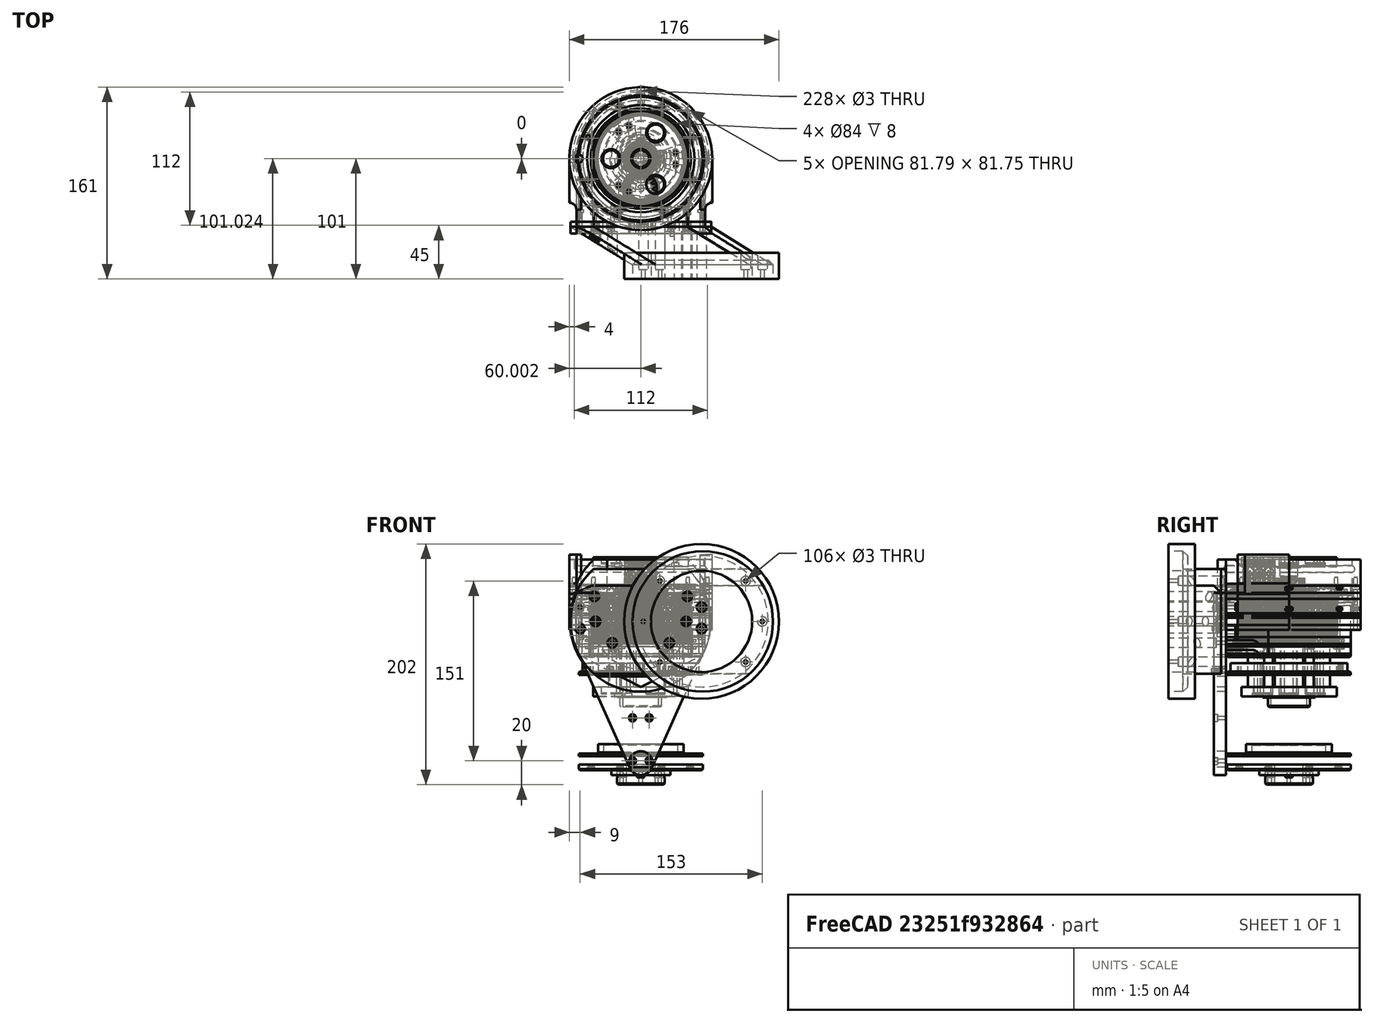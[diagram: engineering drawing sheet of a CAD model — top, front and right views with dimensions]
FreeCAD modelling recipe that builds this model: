
FCSTD DOCUMENT  (FreeCAD 0.19R24276 (Git))
Label: J-max-deep_053
License: All rights reserved
LicenseURL: http://en.wikipedia.org/wiki/All_rights_reserved
objects: Part::Cylinder×715, Part::Cut×269, Part::Compound×252, Part::Box×221, Part::FeaturePython×74, Part::Fillet×14, Part::Chamfer×11, Mesh::Feature×8, Part::Common×7, Part::Torus×4, Part::Wedge×4, Sketcher::SketchObject×3, Part::Extrusion×2, PartDesign::Pad×1, PartDesign::Body×1
note: 1579 computed .brp shape members not serialized (recipe doc carries the construction recipe); baked Part::Feature solids carry a one-line shape summary decoded from their .brp

FEATURE [Part::Cylinder] Cylinder862  label="Válec862"
  Angle = 360
  AttacherType = Attacher::AttachEngine3D
  Height = 20
  Placement = pos=(-51,-40,7) rot=(1,0,0;1.5708rad)
  Radius = 1.5
FEATURE [Part::Cylinder] Cylinder863  label="Válec863"
  Angle = 360
  AttacherType = Attacher::AttachEngine3D
  Height = 40
  Placement = pos=(-59,-17,0) rot=(0,0,1;0rad)
  Radius = 10
FEATURE [Part::Cylinder] Cylinder864  label="Válec864"
  Angle = 360
  AttacherType = Attacher::AttachEngine3D
  Height = 10
  Placement = pos=(0,0,20) rot=(0,0,1;0rad)
  Radius = 52
FEATURE [Part::Cylinder] Cylinder865  label="Válec865"
  Angle = 360
  AttacherType = Attacher::AttachEngine3D
  Height = 20
  Placement = pos=(51,-40,7) rot=(1,0,0;1.5708rad)
  Radius = 1.5
FEATURE [Part::Cylinder] Cylinder866  label="Válec866"
  Angle = 360
  AttacherType = Attacher::AttachEngine3D
  Height = 20
  Placement = pos=(56,0,2) rot=(0,0,1;1.5708rad)
  Radius = 1.5
FEATURE [Part::Box] Box134  label="Krychle134"
  AttacherType = Attacher::AttachEngine3D
  Height = 10
  Length = 108
  Placement = pos=(-54,-53,20) rot=(0,0,1;0rad)
  Width = 36
FEATURE [Part::Cylinder] Cylinder867  label="Válec867"
  Angle = 360
  AttacherType = Attacher::AttachEngine3D
  Height = 10
  Placement = pos=(0,0,20) rot=(0,0,1;0rad)
  Radius = 52
FEATURE [Part::Box] Box132  label="Krychle132"
  AttacherType = Attacher::AttachEngine3D
  Height = 6
  Length = 6
  Placement = pos=(-23,-47,-8) rot=(0,0,1;0rad)
  Width = 2
FEATURE [Part::Box] Box133  label="Krychle133"
  AttacherType = Attacher::AttachEngine3D
  Height = 6
  Length = 6
  Placement = pos=(-54,-45,4) rot=(0,0,1;0rad)
  Width = 2
FEATURE [Part::Box] Box131  label="Krychle131"
  AttacherType = Attacher::AttachEngine3D
  Height = 6
  Length = 6
  Placement = pos=(17,-47,-8) rot=(0,0,1;0rad)
  Width = 2
FEATURE [Part::Cylinder] Cylinder868  label="Válec868"
  Angle = 360
  AttacherType = Attacher::AttachEngine3D
  Height = 20
  Placement = pos=(-20,-40,-5) rot=(1,0,0;1.5708rad)
  Radius = 1.5
FEATURE [Part::Cylinder] Cylinder869  label="Válec869"
  Angle = 360
  AttacherType = Attacher::AttachEngine3D
  Height = 20
  Placement = pos=(39.598,39.598,2) rot=(0,0,1;2.35619rad)
  Radius = 1.5
FEATURE [Part::Cylinder] Cylinder870  label="Válec870"
  Angle = 360
  AttacherType = Attacher::AttachEngine3D
  Height = 20
  Placement = pos=(20,-40,-5) rot=(1,0,0;1.5708rad)
  Radius = 1.5
FEATURE [Part::Compound] Compound261
  Links = -> [Cylinder868,Cylinder870,Cylinder865,Cylinder862]
FEATURE [Part::Cylinder] Cylinder871  label="Válec871"
  Angle = 360
  AttacherType = Attacher::AttachEngine3D
  Height = 20
  Placement = pos=(-39.6,-39.6,-10) rot=(0,0,-1;0.785398rad)
  Radius = 4
FEATURE [Part::Cylinder] Cylinder872  label="Válec872"
  Angle = 360
  AttacherType = Attacher::AttachEngine3D
  Height = 20
  Placement = pos=(39.6,-39.6,-10) rot=(0,0,1;0.785398rad)
  Radius = 4
FEATURE [Part::Compound] Compound259
  Links = -> [Cylinder871,Cylinder872]
FEATURE [Part::Box] Box130  label="Krychle130"
  AttacherType = Attacher::AttachEngine3D
  Height = 6
  Length = 6
  Placement = pos=(48,-45,4) rot=(0,0,1;0rad)
  Width = 2
FEATURE [Part::Compound] Compound258
  Links = -> [Box132,Box131,Box130,Box133]
FEATURE [Part::Cylinder] Cylinder873  label="Válec873"
  Angle = 360
  AttacherType = Attacher::AttachEngine3D
  Height = 20
  Placement = pos=(-39.598,-39.598,2) rot=(0,0,-1;0.785398rad)
  Radius = 1.5
FEATURE [Part::FeaturePython] Tube087  # WARN: FeaturePython — macro-defined, semantics opaque (R4)
  AttacherType = Attacher::AttachEngine3D
  Height = 8
  InnerRadius = 42
  OuterRadius = 52
  Placement = pos=(0,0,-8) rot=(0,0,1;0rad)
FEATURE [Part::FeaturePython] wormgear045  # WARN: FeaturePython — macro-defined, semantics opaque (R4)
  AttacherType = Attacher::AttachEngine3D
  Placement = pos=(0,0,0) rot=(0,0,1;0.083427rad)
  beta = 34.422
  clearance = 0.25
  diameter = 78.8
  head = 0
  height = 20
  module = 1.2
  pressure_angle = 20
  reverse_pitch = false
  teeth = 45
  version = 0.0.3
FEATURE [Part::FeaturePython] wormgear046  # WARN: FeaturePython — macro-defined, semantics opaque (R4)
  AttacherType = Attacher::AttachEngine3D
  beta = 34.422
  clearance = 0.25
  diameter = 78.8
  head = 0
  height = 20
  module = 1.2
  pressure_angle = 20
  reverse_pitch = true
  teeth = 45
  version = 0.0.3
FEATURE [Part::Cut] Cut152
  Base = -> Box134
  Placement = pos=(0,0,-10) rot=(0,0,1;0rad)
  Tool = -> Cylinder867
FEATURE [Part::Cylinder] Cylinder372  label="Válec372"
  Angle = 360
  AttacherType = Attacher::AttachEngine3D
  Height = 20
  Placement = pos=(-1.2e-14,56,2) rot=(0,0,1;3.14159rad)
  Radius = 1.5
FEATURE [Part::Cylinder] Cylinder874  label="Válec874"
  Angle = 360
  AttacherType = Attacher::AttachEngine3D
  Height = 20
  Placement = pos=(0,-56,2) rot=(0,0,1;0rad)
  Radius = 1.5
FEATURE [Part::Cylinder] Cylinder875  label="Válec875"
  Angle = 360
  AttacherType = Attacher::AttachEngine3D
  Height = 20
  Placement = pos=(39.598,-39.598,2) rot=(0,0,1;0.785398rad)
  Radius = 1.5
FEATURE [Part::Cylinder] Cylinder377  label="Válec377"
  Angle = 360
  AttacherType = Attacher::AttachEngine3D
  Height = 20
  Placement = pos=(-39.598,39.598,2) rot=(0,0,1;3.92699rad)
  Radius = 1.5
FEATURE [Part::Cylinder] Cylinder876  label="Válec876"
  Angle = 360
  AttacherType = Attacher::AttachEngine3D
  Height = 20
  Placement = pos=(-56,-1.3e-14,2) rot=(0,0,-1;1.5708rad)
  Radius = 1.5
FEATURE [Part::Compound] Compound262
  Links = -> [Cylinder874,Cylinder875,Cylinder866,Cylinder869,Cylinder372,Cylinder377,Cylinder876,Cylinder873]
FEATURE [Part::Cut] Cut151
  Base = -> Cut152
  Tool = -> Compound262
FEATURE [Part::Box] Box398  label="Krychle398"
  AttacherType = Attacher::AttachEngine3D
  Height = 6
  Length = 6
  Placement = pos=(-54,-45,4) rot=(0,0,1;0rad)
  Width = 2
FEATURE [Part::Cylinder] Cylinder877  label="Válec877"
  Angle = 360
  AttacherType = Attacher::AttachEngine3D
  Height = 20
  Placement = pos=(-39.6,-39.6,-10) rot=(0,0,-1;0.785398rad)
  Radius = 4
FEATURE [Part::Cylinder] Cylinder878  label="Válec878"
  Angle = 360
  AttacherType = Attacher::AttachEngine3D
  Height = 40
  Placement = pos=(59,-17,0) rot=(0,0,1;0rad)
  Radius = 10
FEATURE [Part::Box] Box399  label="Krychle399"
  AttacherType = Attacher::AttachEngine3D
  Height = 6
  Length = 6
  Placement = pos=(21,-47,-8) rot=(0,0,1;0rad)
  Width = 2
FEATURE [Part::Box] Box400  label="Krychle400"
  AttacherType = Attacher::AttachEngine3D
  Height = 10
  Length = 10
  Placement = pos=(50,-43,10) rot=(0,0,1;0rad)
  Width = 43
FEATURE [Part::Box] Box401  label="Krychle401"
  AttacherType = Attacher::AttachEngine3D
  Height = 6
  Length = 6
  Placement = pos=(48,-45,4) rot=(0,0,1;0rad)
  Width = 2
FEATURE [Part::Box] Box402  label="Krychle402"
  AttacherType = Attacher::AttachEngine3D
  Height = 6
  Length = 6
  Placement = pos=(-27,-47,-8) rot=(0,0,1;0rad)
  Width = 2
FEATURE [Part::Compound] Compound772
  Links = -> [Box402,Box399,Box401,Box398]
FEATURE [Part::Box] Box403  label="Krychle403"
  AttacherType = Attacher::AttachEngine3D
  Height = 8
  Length = 108
  Placement = pos=(-54,-53,20) rot=(0,0,1;0rad)
  Width = 36
FEATURE [Part::Cylinder] Cylinder879  label="Válec879"
  Angle = 360
  AttacherType = Attacher::AttachEngine3D
  Height = 8
  Placement = pos=(0,0,20) rot=(0,0,1;0rad)
  Radius = 52
FEATURE [Part::Cut] Cut400
  Base = -> Box403
  Placement = pos=(0,0,-20) rot=(0,0,1;0rad)
  Tool = -> Cylinder879
FEATURE [Part::Cylinder] Cylinder880  label="Válec880"
  Angle = 360
  AttacherType = Attacher::AttachEngine3D
  Height = 40
  Placement = pos=(-59,-17,0) rot=(0,0,1;0rad)
  Radius = 10
FEATURE [Part::Compound] Compound774
  Links = -> [Cylinder878,Cylinder880]
FEATURE [Part::Cylinder] Cylinder881  label="Válec881"
  Angle = 360
  AttacherType = Attacher::AttachEngine3D
  Height = 20
  Placement = pos=(-51,-40,7) rot=(1,0,0;1.5708rad)
  Radius = 1.5
FEATURE [Part::Cylinder] Cylinder882  label="Válec882"
  Angle = 360
  AttacherType = Attacher::AttachEngine3D
  Height = 20
  Placement = pos=(39.6,-39.6,-10) rot=(0,0,1;0.785398rad)
  Radius = 4
FEATURE [Part::Compound] Compound775
  Links = -> [Cylinder877,Cylinder882]
FEATURE [Part::Cylinder] Cylinder883  label="Válec883"
  Angle = 360
  AttacherType = Attacher::AttachEngine3D
  Height = 20
  Placement = pos=(24,-40,-5) rot=(1,0,0;1.5708rad)
  Radius = 1.5
FEATURE [Part::Cylinder] Cylinder884  label="Válec884"
  Angle = 360
  AttacherType = Attacher::AttachEngine3D
  Height = 20
  Placement = pos=(51,-40,7) rot=(1,0,0;1.5708rad)
  Radius = 1.5
FEATURE [Part::Cylinder] Cylinder885  label="Válec885"
  Angle = 360
  AttacherType = Attacher::AttachEngine3D
  Height = 20
  Placement = pos=(-24,-40,-5) rot=(1,0,0;1.5708rad)
  Radius = 1.5
FEATURE [Part::Compound] Compound773
  Links = -> [Cylinder885,Cylinder883,Cylinder884,Cylinder881]
FEATURE [Part::Cylinder] Cylinder886  label="Válec886"
  Angle = 360
  AttacherType = Attacher::AttachEngine3D
  Height = 20
  Placement = pos=(39.598,39.598,2) rot=(0,0,1;2.35619rad)
  Radius = 1.5
FEATURE [Part::Cylinder] Cylinder887  label="Válec887"
  Angle = 360
  AttacherType = Attacher::AttachEngine3D
  Height = 20
  Placement = pos=(0,-56,2) rot=(0,0,1;0rad)
  Radius = 1.5
FEATURE [Part::Box] Box404  label="Krychle404"
  AttacherType = Attacher::AttachEngine3D
  Height = 2
  Length = 6
  Placement = pos=(-41,-3,-4) rot=(0,0,1;1.5708rad)
  Width = 8
FEATURE [Part::Cylinder] Cylinder888  label="Válec888"
  Angle = 360
  AttacherType = Attacher::AttachEngine3D
  Height = 20
  Placement = pos=(24,-40,-5) rot=(1,0,0;1.5708rad)
  Radius = 1.5
FEATURE [Part::Cylinder] Cylinder889  label="Válec889"
  Angle = 360
  AttacherType = Attacher::AttachEngine3D
  Height = 10
  Placement = pos=(60,-43,10) rot=(0,0,1;0rad)
  Radius = 6
FEATURE [Part::Cylinder] Cylinder890  label="Válec890"
  Angle = 360
  AttacherType = Attacher::AttachEngine3D
  Height = 20
  Placement = pos=(-39.598,-39.598,2) rot=(0,0,-1;0.785398rad)
  Radius = 1.5
FEATURE [Part::Box] Box405  label="Krychle405"
  AttacherType = Attacher::AttachEngine3D
  Height = 10
  Length = 10
  Placement = pos=(-60,-43,10) rot=(0,0,1;0rad)
  Width = 43
FEATURE [Part::Compound] Compound778
  Links = -> [Box405,Box400]
FEATURE [Part::Cylinder] Cylinder891  label="Válec891"
  Angle = 360
  AttacherType = Attacher::AttachEngine3D
  Height = 20
  Placement = pos=(-39.598,39.598,2) rot=(0,0,1;3.92699rad)
  Radius = 1.5
FEATURE [Part::Cylinder] Cylinder892  label="Válec892"
  Angle = 360
  AttacherType = Attacher::AttachEngine3D
  Height = 20
  Placement = pos=(56,0,2) rot=(0,0,1;1.5708rad)
  Radius = 1.5
FEATURE [Part::Cylinder] Cylinder893  label="Válec893"
  Angle = 360
  AttacherType = Attacher::AttachEngine3D
  Height = 20
  Placement = pos=(-1.2e-14,56,2) rot=(0,0,1;3.14159rad)
  Radius = 1.5
FEATURE [Part::Cylinder] Cylinder894  label="Válec894"
  Angle = 360
  AttacherType = Attacher::AttachEngine3D
  Height = 20
  Placement = pos=(-56,-1.3e-14,2) rot=(0,0,-1;1.5708rad)
  Radius = 1.5
FEATURE [Part::Cylinder] Cylinder895  label="Válec895"
  Angle = 360
  AttacherType = Attacher::AttachEngine3D
  Height = 10
  Placement = pos=(-60,-43,10) rot=(0,0,1;0rad)
  Radius = 6
FEATURE [Part::Compound] Compound777
  Links = -> [Cylinder889,Cylinder895]
FEATURE [Part::Cylinder] Cylinder896  label="Válec896"
  Angle = 360
  AttacherType = Attacher::AttachEngine3D
  Height = 20
  Placement = pos=(-51,-40,7) rot=(1,0,0;1.5708rad)
  Radius = 1.5
FEATURE [Part::Cylinder] Cylinder897  label="Válec897"
  Angle = 360
  AttacherType = Attacher::AttachEngine3D
  Height = 20
  Placement = pos=(51,-40,7) rot=(1,0,0;1.5708rad)
  Radius = 1.5
FEATURE [Part::Box] Box406  label="Krychle406"
  AttacherType = Attacher::AttachEngine3D
  Height = 6
  Length = 6
  Placement = pos=(48,-45,4) rot=(0,0,1;0rad)
  Width = 2
FEATURE [Part::Cylinder] Cylinder898  label="Válec898"
  Angle = 360
  AttacherType = Attacher::AttachEngine3D
  Height = 20
  Placement = pos=(0,45,-18) rot=(0,0,1;0rad)
  Radius = 1.5
FEATURE [Part::Cylinder] Cylinder899  label="Válec899"
  Angle = 360
  AttacherType = Attacher::AttachEngine3D
  Height = 20
  Placement = pos=(39.598,-39.598,2) rot=(0,0,1;0.785398rad)
  Radius = 1.5
FEATURE [Part::Compound] Compound776
  Links = -> [Cylinder887,Cylinder899,Cylinder892,Cylinder886,Cylinder893,Cylinder891,Cylinder894,Cylinder890]
FEATURE [Part::Cylinder] Cylinder900  label="Válec900"
  Angle = 360
  AttacherType = Attacher::AttachEngine3D
  Height = 20
  Placement = pos=(-24,-40,-5) rot=(1,0,0;1.5708rad)
  Radius = 1.5
FEATURE [Part::Compound] Compound255
  Links = -> [Cylinder900,Cylinder888,Cylinder897,Cylinder896]
FEATURE [Part::Box] Box407  label="Krychle407"
  AttacherType = Attacher::AttachEngine3D
  Height = 2
  Length = 6
  Placement = pos=(3,-41,-4) rot=(0,0,1;3.14159rad)
  Width = 8
FEATURE [Part::Cylinder] Cylinder901  label="Válec901"
  Angle = 360
  AttacherType = Attacher::AttachEngine3D
  Height = 20
  Placement = pos=(1.4e-14,-45,-18) rot=(0,0,1;3.14159rad)
  Radius = 1.5
FEATURE [Part::Box] Box408  label="Krychle408"
  AttacherType = Attacher::AttachEngine3D
  Height = 2
  Length = 6
  Placement = pos=(-31.1127,26.8701,-4) rot=(0,0,1;0.785398rad)
  Width = 8
FEATURE [Part::Box] Box409  label="Krychle409"
  AttacherType = Attacher::AttachEngine3D
  Height = 6
  Length = 6
  Placement = pos=(21,-47,-8) rot=(0,0,1;0rad)
  Width = 2
FEATURE [Part::Box] Box410  label="Krychle410"
  AttacherType = Attacher::AttachEngine3D
  Height = 6
  Length = 6
  Placement = pos=(-27,-47,-8) rot=(0,0,1;0rad)
  Width = 2
FEATURE [Part::Box] Box411  label="Krychle411"
  AttacherType = Attacher::AttachEngine3D
  Height = 6
  Length = 6
  Placement = pos=(-54,-45,4) rot=(0,0,1;0rad)
  Width = 2
FEATURE [Part::Compound] Compound257
  Links = -> [Box410,Box409,Box406,Box411]
FEATURE [Part::Box] Box412  label="Krychle412"
  AttacherType = Attacher::AttachEngine3D
  Height = 2
  Length = 6
  Placement = pos=(31.1127,-26.8701,-4) rot=(0,0,1;3.92699rad)
  Width = 8
FEATURE [Part::Cylinder] Cylinder902  label="Válec902"
  Angle = 360
  AttacherType = Attacher::AttachEngine3D
  Height = 20
  Placement = pos=(-31.8198,-31.8198,-18) rot=(0,0,1;2.35619rad)
  Radius = 1.5
FEATURE [Part::Cylinder] Cylinder903  label="Válec903"
  Angle = 360
  AttacherType = Attacher::AttachEngine3D
  Height = 20
  Placement = pos=(31.8198,-31.8198,-18) rot=(0,0,1;3.92699rad)
  Radius = 1.5
FEATURE [Part::Cylinder] Cylinder904  label="Válec904"
  Angle = 360
  AttacherType = Attacher::AttachEngine3D
  Height = 20
  Placement = pos=(-31.8198,31.8198,-18) rot=(0,0,1;0.785398rad)
  Radius = 1.5
FEATURE [Part::Cylinder] Cylinder905  label="Válec905"
  Angle = 360
  AttacherType = Attacher::AttachEngine3D
  Height = 20
  Placement = pos=(45,1.9e-14,-18) rot=(0,0,-1;1.5708rad)
  Radius = 1.5
FEATURE [Part::Box] Box413  label="Krychle413"
  AttacherType = Attacher::AttachEngine3D
  Height = 2
  Length = 6
  Placement = pos=(-3,41,-4) rot=(0,0,1;0rad)
  Width = 8
FEATURE [Part::Box] Box414  label="Krychle414"
  AttacherType = Attacher::AttachEngine3D
  Height = 2
  Length = 6
  Placement = pos=(26.8701,31.1127,-4) rot=(0,0,-1;0.785398rad)
  Width = 8
FEATURE [Part::Cylinder] Cylinder906  label="Válec906"
  Angle = 360
  AttacherType = Attacher::AttachEngine3D
  Height = 20
  Placement = pos=(31.8198,31.8198,-18) rot=(0,0,-1;0.785398rad)
  Radius = 1.5
FEATURE [Part::Box] Box415  label="Krychle415"
  AttacherType = Attacher::AttachEngine3D
  Height = 2
  Length = 6
  Placement = pos=(-26.8701,-31.1127,-4) rot=(0,0,1;2.35619rad)
  Width = 8
FEATURE [Part::Cylinder] Cylinder907  label="Válec907"
  Angle = 360
  AttacherType = Attacher::AttachEngine3D
  Height = 20
  Placement = pos=(-45,-6e-15,-18) rot=(0,0,1;1.5708rad)
  Radius = 1.5
FEATURE [Part::Compound] Compound256
  Links = -> [Cylinder898,Cylinder904,Cylinder907,Cylinder902,Cylinder901,Cylinder903,Cylinder905,Cylinder906]
  Placement = pos=(0,0,0) rot=(0,0,1;0.392699rad)
FEATURE [Part::Box] Box128  label="Krychle128"
  AttacherType = Attacher::AttachEngine3D
  Height = 2
  Length = 6
  Placement = pos=(41,3,-4) rot=(0,0,-1;1.5708rad)
  Width = 8
FEATURE [Part::Compound] Compound780
  Links = -> [Box413,Box408,Box404,Box415,Box407,Box412,Box128,Box414]
  Placement = pos=(0,0,0) rot=(0,0,1;0.392699rad)
FEATURE [Part::Box] Box129  label="Krychle129"
  AttacherType = Attacher::AttachEngine3D
  Height = 10
  Length = 108
  Placement = pos=(-54,-53,20) rot=(0,0,1;0rad)
  Width = 36
FEATURE [Part::Cylinder] Cylinder908  label="Válec908"
  Angle = 360
  AttacherType = Attacher::AttachEngine3D
  Height = 40
  Placement = pos=(59,-17,0) rot=(0,0,1;0rad)
  Radius = 10
FEATURE [Part::Compound] Compound260
  Links = -> [Cylinder908,Cylinder863]
FEATURE [Part::Cylinder] Cylinder909  label="Válec909"
  Angle = 360
  AttacherType = Attacher::AttachEngine3D
  Height = 20
  Placement = pos=(31.8198,31.8198,-18) rot=(0,0,-1;0.785398rad)
  Radius = 1.5
FEATURE [Part::Cylinder] Cylinder910  label="Válec910"
  Angle = 360
  AttacherType = Attacher::AttachEngine3D
  Height = 20
  Placement = pos=(39.598,-39.598,2) rot=(0,0,1;0.785398rad)
  Radius = 1.5
FEATURE [Part::Cylinder] Cylinder911  label="Válec911"
  Angle = 360
  AttacherType = Attacher::AttachEngine3D
  Height = 20
  Placement = pos=(0,45,-18) rot=(0,0,1;0rad)
  Radius = 1.5
FEATURE [Part::Cylinder] Cylinder912  label="Válec912"
  Angle = 360
  AttacherType = Attacher::AttachEngine3D
  Height = 20
  Placement = pos=(1.4e-14,-45,-18) rot=(0,0,1;3.14159rad)
  Radius = 1.5
FEATURE [Part::Cylinder] Cylinder913  label="Válec913"
  Angle = 360
  AttacherType = Attacher::AttachEngine3D
  Height = 20
  Placement = pos=(31.8198,-31.8198,-18) rot=(0,0,1;3.92699rad)
  Radius = 1.5
FEATURE [Part::Cylinder] Cylinder914  label="Válec914"
  Angle = 360
  AttacherType = Attacher::AttachEngine3D
  Height = 20
  Placement = pos=(-31.8198,-31.8198,-18) rot=(0,0,1;2.35619rad)
  Radius = 1.5
FEATURE [Part::Cylinder] Cylinder915  label="Válec915"
  Angle = 360
  AttacherType = Attacher::AttachEngine3D
  Height = 20
  Placement = pos=(-31.8198,31.8198,-18) rot=(0,0,1;0.785398rad)
  Radius = 1.5
FEATURE [Part::Cylinder] Cylinder916  label="Válec916"
  Angle = 360
  AttacherType = Attacher::AttachEngine3D
  Height = 20
  Placement = pos=(-45,-6e-15,-18) rot=(0,0,1;1.5708rad)
  Radius = 1.5
FEATURE [Part::Cylinder] Cylinder917  label="Válec917"
  Angle = 360
  AttacherType = Attacher::AttachEngine3D
  Height = 20
  Placement = pos=(45,1.9e-14,-18) rot=(0,0,-1;1.5708rad)
  Radius = 1.5
FEATURE [Part::Compound] Compound771
  Links = -> [Cylinder911,Cylinder915,Cylinder916,Cylinder914,Cylinder912,Cylinder913,Cylinder917,Cylinder909]
  Placement = pos=(0,0,4) rot=(0,0,1;0.392699rad)
FEATURE [Part::Cylinder] Cylinder918  label="Válec918"
  Angle = 360
  AttacherType = Attacher::AttachEngine3D
  Height = 20
  Placement = pos=(-56,-1.3e-14,2) rot=(0,0,-1;1.5708rad)
  Radius = 1.5
FEATURE [Part::Cut] Cut403
  Base = -> Cut400
  Placement = pos=(0,0,-8) rot=(0,0,1;0rad)
  Tool = -> Compound774
FEATURE [Part::Cut] Cut401
  Base = -> Cut403
  Tool = -> Compound775
FEATURE [Part::Cut] Cut402
  Base = -> Cut401
  Tool = -> Compound772
FEATURE [Part::Cut] Cut399
  Base = -> Cut402
  Tool = -> Compound773
FEATURE [Part::Fillet] Fillet014
  Base = -> Cut399
  Edges = 2 edges r=12: [Edge2,Edge38]
FEATURE [Part::Cut] Cut405
  Base = -> Compound778
  Tool = -> Compound776
FEATURE [Part::Cut] Cut406
  Base = -> Cut405
  Tool = -> Compound777
FEATURE [Part::Fillet] Fillet015
  Base = -> Cut406
  Edges = 2 edges r=4: [Edge4,Edge43]
FEATURE [Part::Cut] Cut147
  Base = -> Box129
  Placement = pos=(0,0,-20) rot=(0,0,1;0rad)
  Tool = -> Cylinder864
FEATURE [Part::Cut] Cut407
  Base = -> Tube087
  Tool = -> Compound257
FEATURE [Part::Cut] Cut144
  Base = -> Cut407
  Tool = -> Compound255
FEATURE [Part::Cut] Cut404
  Base = -> Cut144
  Tool = -> Compound780
FEATURE [Part::Cut] Cut145
  Base = -> Cut404
  Tool = -> Compound256
FEATURE [Part::Cut] Cut146
  Base = -> Cut147
  Tool = -> Compound260
FEATURE [Part::Cut] Cut149
  Base = -> Cut146
  Tool = -> Compound259
FEATURE [Part::Cut] Cut148
  Base = -> Cut149
  Tool = -> Compound258
FEATURE [Part::Cut] Cut150
  Base = -> Cut148
  Tool = -> Compound261
FEATURE [Part::Fillet] Fillet013
  Base = -> Cut150
  Edges = 2 edges r=12: [Edge6,Edge42]
FEATURE [Part::Cylinder] Cylinder919  label="Válec919"
  Angle = 360
  AttacherType = Attacher::AttachEngine3D
  Height = 20
  Placement = pos=(-39.598,-39.598,2) rot=(0,0,-1;0.785398rad)
  Radius = 1.5
FEATURE [Part::Cylinder] Cylinder920  label="Válec920"
  Angle = 360
  AttacherType = Attacher::AttachEngine3D
  Height = 20
  Placement = pos=(39.6,-39.6,-10) rot=(0,0,1;0.785398rad)
  Radius = 4
FEATURE [Part::Cylinder] Cylinder921  label="Válec921"
  Angle = 360
  AttacherType = Attacher::AttachEngine3D
  Height = 20
  Placement = pos=(-39.598,39.598,2) rot=(0,0,1;3.92699rad)
  Radius = 1.5
FEATURE [Part::Cylinder] Cylinder922  label="Válec922"
  Angle = 360
  AttacherType = Attacher::AttachEngine3D
  Height = 20
  Placement = pos=(-39.6,-39.6,-10) rot=(0,0,-1;0.785398rad)
  Radius = 4
FEATURE [Part::Compound] Compound768
  Links = -> [Cylinder922,Cylinder920]
FEATURE [Part::Cylinder] Cylinder923  label="Válec923"
  Angle = 360
  AttacherType = Attacher::AttachEngine3D
  Height = 20
  Placement = pos=(-1.2e-14,56,2) rot=(0,0,1;3.14159rad)
  Radius = 1.5
FEATURE [Part::Cylinder] Cylinder924  label="Válec924"
  Angle = 360
  AttacherType = Attacher::AttachEngine3D
  Height = 20
  Placement = pos=(56,0,2) rot=(0,0,1;1.5708rad)
  Radius = 1.5
FEATURE [Part::Cylinder] Cylinder925  label="Válec925"
  Angle = 360
  AttacherType = Attacher::AttachEngine3D
  Height = 10
  Radius = 52
FEATURE [Part::Cut] Cut396
  Base = -> Cylinder925
  Tool = -> wormgear045
FEATURE [Part::Cylinder] Cylinder926  label="Válec926"
  Angle = 360
  AttacherType = Attacher::AttachEngine3D
  Height = 10
  Radius = 60
FEATURE [Part::Cut] Cut397
  Base = -> Cylinder926
  Placement = pos=(0,0,10) rot=(0,0,1;0.034907rad)
  Tool = -> wormgear046
FEATURE [Part::Compound] Compound770
  Links = -> [Cut397,Cut396]
FEATURE [Part::Cylinder] Cylinder927  label="Válec927"
  Angle = 360
  AttacherType = Attacher::AttachEngine3D
  Height = 20
  Placement = pos=(0,-56,2) rot=(0,0,1;0rad)
  Radius = 1.5
FEATURE [Part::Cylinder] Cylinder928  label="Válec928"
  Angle = 360
  AttacherType = Attacher::AttachEngine3D
  Height = 20
  Placement = pos=(39.598,39.598,2) rot=(0,0,1;2.35619rad)
  Radius = 1.5
FEATURE [Part::Compound] Compound769
  Links = -> [Cylinder927,Cylinder910,Cylinder924,Cylinder928,Cylinder923,Cylinder921,Cylinder918,Cylinder919]
FEATURE [Part::Cut] Cut394
  Base = -> Compound770
  Tool = -> Compound769
FEATURE [Part::Cut] Cut395
  Base = -> Cut394
  Tool = -> Compound768
FEATURE [Part::Cut] Cut398
  Base = -> Cut395
  Tool = -> Compound771
FEATURE [Part::Compound] Compound779  label="J-max_monoblok"
  Links = -> [Fillet014,Fillet013,Cut151,Cut145,Fillet015,Cut398]
FEATURE [Part::FeaturePython] wormgear052  # WARN: FeaturePython — macro-defined, semantics opaque (R4)
  AttacherType = Attacher::AttachEngine3D
  Placement = pos=(0,0,0) rot=(0,0,1;0.083427rad)
  beta = 40.5833
  clearance = 0.25
  diameter = 78.8
  head = 0
  height = 20
  module = 1.5
  pressure_angle = 20
  reverse_pitch = false
  teeth = 45
  version = 0.0.3
FEATURE [Part::FeaturePython] wormgear053  # WARN: FeaturePython — macro-defined, semantics opaque (R4)
  AttacherType = Attacher::AttachEngine3D
  Placement = pos=(0,0,0) rot=(0,0,1;0.10376rad)
  beta = 40.5833
  clearance = 0.25
  diameter = 78.8
  head = 0
  height = 20
  module = 1.5
  pressure_angle = 20
  reverse_pitch = true
  teeth = 45
  version = 0.0.3
FEATURE [Part::Cylinder] Cylinder990  label="Válec990"
  Angle = 360
  AttacherType = Attacher::AttachEngine3D
  Height = 50
  Placement = pos=(31.8198,31.8198,-18) rot=(0,0,-1;0.785398rad)
  Radius = 1.5
FEATURE [Part::Cylinder] Cylinder991  label="Válec991"
  Angle = 360
  AttacherType = Attacher::AttachEngine3D
  Height = 50
  Placement = pos=(39.598,-39.598,2) rot=(0,0,1;0.785398rad)
  Radius = 1.5
FEATURE [Part::Cylinder] Cylinder992  label="Válec992"
  Angle = 360
  AttacherType = Attacher::AttachEngine3D
  Height = 50
  Placement = pos=(0,45,-18) rot=(0,0,1;0rad)
  Radius = 1.5
FEATURE [Part::Cylinder] Cylinder993  label="Válec993"
  Angle = 360
  AttacherType = Attacher::AttachEngine3D
  Height = 50
  Placement = pos=(1.4e-14,-45,-18) rot=(0,0,1;3.14159rad)
  Radius = 1.5
FEATURE [Part::Cylinder] Cylinder994  label="Válec994"
  Angle = 360
  AttacherType = Attacher::AttachEngine3D
  Height = 50
  Placement = pos=(31.8198,-31.8198,-18) rot=(0,0,1;3.92699rad)
  Radius = 1.5
FEATURE [Part::Cylinder] Cylinder995  label="Válec995"
  Angle = 360
  AttacherType = Attacher::AttachEngine3D
  Height = 50
  Placement = pos=(-31.8198,-31.8198,-18) rot=(0,0,1;2.35619rad)
  Radius = 1.5
FEATURE [Part::Cylinder] Cylinder996  label="Válec996"
  Angle = 360
  AttacherType = Attacher::AttachEngine3D
  Height = 50
  Placement = pos=(-31.8198,31.8198,-18) rot=(0,0,1;0.785398rad)
  Radius = 1.5
FEATURE [Part::Cylinder] Cylinder997  label="Válec997"
  Angle = 360
  AttacherType = Attacher::AttachEngine3D
  Height = 50
  Placement = pos=(-45,-6e-15,-18) rot=(0,0,1;1.5708rad)
  Radius = 1.5
FEATURE [Part::Cylinder] Cylinder998  label="Válec998"
  Angle = 360
  AttacherType = Attacher::AttachEngine3D
  Height = 50
  Placement = pos=(45,1.9e-14,-18) rot=(0,0,-1;1.5708rad)
  Radius = 1.5
FEATURE [Part::Compound] Compound816
  Links = -> [Cylinder992,Cylinder996,Cylinder997,Cylinder995,Cylinder993,Cylinder994,Cylinder998,Cylinder990]
  Placement = pos=(0,0,4) rot=(0,0,1;0.392699rad)
FEATURE [Part::Cylinder] Cylinder999  label="Válec999"
  Angle = 360
  AttacherType = Attacher::AttachEngine3D
  Height = 50
  Placement = pos=(-56,-1.3e-14,2) rot=(0,0,-1;1.5708rad)
  Radius = 1.5
FEATURE [Part::Cylinder] Cylinder1000  label="Válec1000"
  Angle = 360
  AttacherType = Attacher::AttachEngine3D
  Height = 50
  Placement = pos=(-39.598,-39.598,2) rot=(0,0,-1;0.785398rad)
  Radius = 1.5
FEATURE [Part::Cylinder] Cylinder1001  label="Válec1001"
  Angle = 360
  AttacherType = Attacher::AttachEngine3D
  Height = 20
  Placement = pos=(39.6,-39.6,-10) rot=(0,0,1;0.785398rad)
  Radius = 4
FEATURE [Part::Cylinder] Cylinder1002  label="Válec1002"
  Angle = 360
  AttacherType = Attacher::AttachEngine3D
  Height = 50
  Placement = pos=(-39.598,39.598,2) rot=(0,0,1;3.92699rad)
  Radius = 1.5
FEATURE [Part::Cylinder] Cylinder1003  label="Válec1003"
  Angle = 360
  AttacherType = Attacher::AttachEngine3D
  Height = 20
  Placement = pos=(-39.6,-39.6,-10) rot=(0,0,-1;0.785398rad)
  Radius = 4
FEATURE [Part::Compound] Compound813
  Links = -> [Cylinder1003,Cylinder1001]
FEATURE [Part::Cylinder] Cylinder1004  label="Válec1004"
  Angle = 360
  AttacherType = Attacher::AttachEngine3D
  Height = 50
  Placement = pos=(-1.2e-14,56,2) rot=(0,0,1;3.14159rad)
  Radius = 1.5
FEATURE [Part::Cylinder] Cylinder1005  label="Válec1005"
  Angle = 360
  AttacherType = Attacher::AttachEngine3D
  Height = 50
  Placement = pos=(56,0,2) rot=(0,0,1;1.5708rad)
  Radius = 1.5
FEATURE [Part::Cylinder] Cylinder1006  label="Válec1006"
  Angle = 360
  AttacherType = Attacher::AttachEngine3D
  Height = 16
  Radius = 52
FEATURE [Part::Cut] Cut418
  Base = -> Cylinder1006
  Tool = -> wormgear052
FEATURE [Part::Cylinder] Cylinder1007  label="Válec1007"
  Angle = 360
  AttacherType = Attacher::AttachEngine3D
  Height = 16
  Radius = 60
FEATURE [Part::Cut] Cut422
  Base = -> Cylinder1007
  Placement = pos=(0,0,16) rot=(0,0,1;0.034907rad)
  Tool = -> wormgear053
FEATURE [Part::Compound] Compound815
  Links = -> [Cut422,Cut418]
FEATURE [Part::Cylinder] Cylinder1008  label="Válec1008"
  Angle = 360
  AttacherType = Attacher::AttachEngine3D
  Height = 50
  Placement = pos=(0,-56,2) rot=(0,0,1;0rad)
  Radius = 1.5
FEATURE [Part::Cylinder] Cylinder1009  label="Válec1009"
  Angle = 360
  AttacherType = Attacher::AttachEngine3D
  Height = 50
  Placement = pos=(39.598,39.598,2) rot=(0,0,1;2.35619rad)
  Radius = 1.5
FEATURE [Part::Compound] Compound814
  Links = -> [Cylinder1008,Cylinder991,Cylinder1005,Cylinder1009,Cylinder1004,Cylinder1002,Cylinder999,Cylinder1000]
FEATURE [Part::Cut] Cut421
  Base = -> Compound815
  Tool = -> Compound814
FEATURE [Part::Cut] Cut419
  Base = -> Cut421
  Tool = -> Compound813
FEATURE [Part::Cut] Cut420
  Base = -> Cut419
  Tool = -> Compound816
FEATURE [Part::Box] Box416  label="Krychle416"
  AttacherType = Attacher::AttachEngine3D
  Height = 16
  Length = 108
  Placement = pos=(-54,-53,20) rot=(0,0,1;0rad)
  Width = 36
FEATURE [Part::Cylinder] Cylinder1011  label="Válec1011"
  Angle = 360
  AttacherType = Attacher::AttachEngine3D
  Height = 16
  Placement = pos=(0,0,20) rot=(0,0,1;0rad)
  Radius = 52
FEATURE [Part::Cylinder] Cylinder1012  label="Válec1012"
  Angle = 360
  AttacherType = Attacher::AttachEngine3D
  Height = 50
  Placement = pos=(39.598,39.598,2) rot=(0,0,1;2.35619rad)
  Radius = 1.5
FEATURE [Part::Cylinder] Cylinder1013  label="Válec1013"
  Angle = 360
  AttacherType = Attacher::AttachEngine3D
  Height = 50
  Placement = pos=(-39.598,-39.598,2) rot=(0,0,-1;0.785398rad)
  Radius = 1.5
FEATURE [Part::Cylinder] Cylinder1014  label="Válec1014"
  Angle = 360
  AttacherType = Attacher::AttachEngine3D
  Height = 50
  Placement = pos=(-1.2e-14,56,2) rot=(0,0,1;3.14159rad)
  Radius = 1.5
FEATURE [Part::Cylinder] Cylinder1015  label="Válec1015"
  Angle = 360
  AttacherType = Attacher::AttachEngine3D
  Height = 50
  Placement = pos=(0,-56,2) rot=(0,0,1;0rad)
  Radius = 1.5
FEATURE [Part::Cylinder] Cylinder1016  label="Válec1016"
  Angle = 360
  AttacherType = Attacher::AttachEngine3D
  Height = 50
  Placement = pos=(39.598,-39.598,2) rot=(0,0,1;0.785398rad)
  Radius = 1.5
FEATURE [Part::Cylinder] Cylinder1017  label="Válec1017"
  Angle = 360
  AttacherType = Attacher::AttachEngine3D
  Height = 50
  Placement = pos=(-39.598,39.598,2) rot=(0,0,1;3.92699rad)
  Radius = 1.5
FEATURE [Part::Cylinder] Cylinder1018  label="Válec1018"
  Angle = 360
  AttacherType = Attacher::AttachEngine3D
  Height = 50
  Placement = pos=(-56,-1.3e-14,2) rot=(0,0,-1;1.5708rad)
  Radius = 1.5
FEATURE [Part::Cut] Cut424
  Base = -> Box416
  Placement = pos=(0,0,-10) rot=(0,0,1;0rad)
  Tool = -> Cylinder1011
FEATURE [Part::Compound] Compound817
  Links = -> [Cylinder1015,Cylinder1016,Cylinder1012,Cylinder1014,Cylinder1017,Cylinder1018,Cylinder1013]
FEATURE [Part::Cut] Cut423
  Base = -> Cut424
  Placement = pos=(0,0,6) rot=(0,0,1;0rad)
  Tool = -> Compound817
FEATURE [Part::Box] Box417  label="Krychle417"
  AttacherType = Attacher::AttachEngine3D
  Height = 2
  Length = 6
  Placement = pos=(-41,-3,-4) rot=(0,0,1;1.5708rad)
  Width = 8
FEATURE [Part::Cylinder] Cylinder1019  label="Válec1019"
  Angle = 360
  AttacherType = Attacher::AttachEngine3D
  Height = 20
  Placement = pos=(24,-40,-5) rot=(1,0,0;1.5708rad)
  Radius = 1.5
FEATURE [Part::FeaturePython] Tube088  # WARN: FeaturePython — macro-defined, semantics opaque (R4)
  AttacherType = Attacher::AttachEngine3D
  Height = 8
  InnerRadius = 42
  OuterRadius = 52
  Placement = pos=(0,0,-8) rot=(0,0,1;0rad)
FEATURE [Part::Cylinder] Cylinder1020  label="Válec1020"
  Angle = 360
  AttacherType = Attacher::AttachEngine3D
  Height = 20
  Placement = pos=(-51,-40,7) rot=(1,0,0;1.5708rad)
  Radius = 1.5
FEATURE [Part::Cylinder] Cylinder1021  label="Válec1021"
  Angle = 360
  AttacherType = Attacher::AttachEngine3D
  Height = 20
  Placement = pos=(51,-40,7) rot=(1,0,0;1.5708rad)
  Radius = 1.5
FEATURE [Part::Box] Box418  label="Krychle418"
  AttacherType = Attacher::AttachEngine3D
  Height = 6
  Length = 6
  Placement = pos=(48,-45,4) rot=(0,0,1;0rad)
  Width = 2
FEATURE [Part::Cylinder] Cylinder1022  label="Válec1022"
  Angle = 360
  AttacherType = Attacher::AttachEngine3D
  Height = 20
  Placement = pos=(0,45,-18) rot=(0,0,1;0rad)
  Radius = 1.5
FEATURE [Part::Cylinder] Cylinder1023  label="Válec1023"
  Angle = 360
  AttacherType = Attacher::AttachEngine3D
  Height = 20
  Placement = pos=(-24,-40,-5) rot=(1,0,0;1.5708rad)
  Radius = 1.5
FEATURE [Part::Compound] Compound818
  Links = -> [Cylinder1023,Cylinder1019,Cylinder1021,Cylinder1020]
FEATURE [Part::Box] Box419  label="Krychle419"
  AttacherType = Attacher::AttachEngine3D
  Height = 2
  Length = 6
  Placement = pos=(3,-41,-4) rot=(0,0,1;3.14159rad)
  Width = 8
FEATURE [Part::Cylinder] Cylinder1024  label="Válec1024"
  Angle = 360
  AttacherType = Attacher::AttachEngine3D
  Height = 20
  Placement = pos=(1.4e-14,-45,-18) rot=(0,0,1;3.14159rad)
  Radius = 1.5
FEATURE [Part::Box] Box420  label="Krychle420"
  AttacherType = Attacher::AttachEngine3D
  Height = 2
  Length = 6
  Placement = pos=(-31.1127,26.8701,-4) rot=(0,0,1;0.785398rad)
  Width = 8
FEATURE [Part::Box] Box421  label="Krychle421"
  AttacherType = Attacher::AttachEngine3D
  Height = 6
  Length = 6
  Placement = pos=(21,-47,-8) rot=(0,0,1;0rad)
  Width = 2
FEATURE [Part::Box] Box422  label="Krychle422"
  AttacherType = Attacher::AttachEngine3D
  Height = 6
  Length = 6
  Placement = pos=(-27,-47,-8) rot=(0,0,1;0rad)
  Width = 2
FEATURE [Part::Box] Box423  label="Krychle423"
  AttacherType = Attacher::AttachEngine3D
  Height = 6
  Length = 6
  Placement = pos=(-54,-45,4) rot=(0,0,1;0rad)
  Width = 2
FEATURE [Part::Compound] Compound820
  Links = -> [Box422,Box421,Box418,Box423]
FEATURE [Part::Box] Box424  label="Krychle424"
  AttacherType = Attacher::AttachEngine3D
  Height = 2
  Length = 6
  Placement = pos=(31.1127,-26.8701,-4) rot=(0,0,1;3.92699rad)
  Width = 8
FEATURE [Part::Cylinder] Cylinder1025  label="Válec1025"
  Angle = 360
  AttacherType = Attacher::AttachEngine3D
  Height = 20
  Placement = pos=(-31.8198,-31.8198,-18) rot=(0,0,1;2.35619rad)
  Radius = 1.5
FEATURE [Part::Cylinder] Cylinder1026  label="Válec1026"
  Angle = 360
  AttacherType = Attacher::AttachEngine3D
  Height = 20
  Placement = pos=(31.8198,-31.8198,-18) rot=(0,0,1;3.92699rad)
  Radius = 1.5
FEATURE [Part::Cylinder] Cylinder1027  label="Válec1027"
  Angle = 360
  AttacherType = Attacher::AttachEngine3D
  Height = 20
  Placement = pos=(-31.8198,31.8198,-18) rot=(0,0,1;0.785398rad)
  Radius = 1.5
FEATURE [Part::Cylinder] Cylinder1028  label="Válec1028"
  Angle = 360
  AttacherType = Attacher::AttachEngine3D
  Height = 20
  Placement = pos=(45,1.9e-14,-18) rot=(0,0,-1;1.5708rad)
  Radius = 1.5
FEATURE [Part::Box] Box425  label="Krychle425"
  AttacherType = Attacher::AttachEngine3D
  Height = 2
  Length = 6
  Placement = pos=(-3,41,-4) rot=(0,0,1;0rad)
  Width = 8
FEATURE [Part::Box] Box426  label="Krychle426"
  AttacherType = Attacher::AttachEngine3D
  Height = 2
  Length = 6
  Placement = pos=(26.8701,31.1127,-4) rot=(0,0,-1;0.785398rad)
  Width = 8
FEATURE [Part::Cylinder] Cylinder1029  label="Válec1029"
  Angle = 360
  AttacherType = Attacher::AttachEngine3D
  Height = 20
  Placement = pos=(31.8198,31.8198,-18) rot=(0,0,-1;0.785398rad)
  Radius = 1.5
FEATURE [Part::Box] Box427  label="Krychle427"
  AttacherType = Attacher::AttachEngine3D
  Height = 2
  Length = 6
  Placement = pos=(-26.8701,-31.1127,-4) rot=(0,0,1;2.35619rad)
  Width = 8
FEATURE [Part::Cylinder] Cylinder1030  label="Válec1030"
  Angle = 360
  AttacherType = Attacher::AttachEngine3D
  Height = 20
  Placement = pos=(-45,-6e-15,-18) rot=(0,0,1;1.5708rad)
  Radius = 1.5
FEATURE [Part::Compound] Compound819
  Links = -> [Cylinder1022,Cylinder1027,Cylinder1030,Cylinder1025,Cylinder1024,Cylinder1026,Cylinder1028,Cylinder1029]
  Placement = pos=(0,0,0) rot=(0,0,1;0.392699rad)
FEATURE [Part::Box] Box428  label="Krychle428"
  AttacherType = Attacher::AttachEngine3D
  Height = 2
  Length = 6
  Placement = pos=(41,3,-4) rot=(0,0,-1;1.5708rad)
  Width = 8
FEATURE [Part::Compound] Compound821
  Links = -> [Box425,Box420,Box417,Box427,Box419,Box424,Box428,Box426]
  Placement = pos=(0,0,0) rot=(0,0,1;0.392699rad)
FEATURE [Part::Cut] Cut426
  Base = -> Tube088
  Tool = -> Compound820
FEATURE [Part::Cut] Cut427
  Base = -> Cut426
  Tool = -> Compound818
FEATURE [Part::Cut] Cut425
  Base = -> Cut427
  Tool = -> Compound821
FEATURE [Part::Cut] Cut428
  Base = -> Cut425
  Tool = -> Compound819
FEATURE [Part::Cylinder] Cylinder1031  label="Válec1031"
  Angle = 360
  AttacherType = Attacher::AttachEngine3D
  Height = 20
  Placement = pos=(-51,-40,7) rot=(1,0,0;1.5708rad)
  Radius = 1.5
FEATURE [Part::Cylinder] Cylinder1032  label="Válec1032"
  Angle = 360
  AttacherType = Attacher::AttachEngine3D
  Height = 40
  Placement = pos=(-59,-17,0) rot=(0,0,1;0rad)
  Radius = 10
FEATURE [Part::Cylinder] Cylinder1033  label="Válec1033"
  Angle = 360
  AttacherType = Attacher::AttachEngine3D
  Height = 20
  Placement = pos=(0,0,20) rot=(0,0,1;0rad)
  Radius = 52
FEATURE [Part::Cylinder] Cylinder1034  label="Válec1034"
  Angle = 360
  AttacherType = Attacher::AttachEngine3D
  Height = 20
  Placement = pos=(51,-40,7) rot=(1,0,0;1.5708rad)
  Radius = 1.5
FEATURE [Part::Box] Box429  label="Krychle429"
  AttacherType = Attacher::AttachEngine3D
  Height = 6
  Length = 6
  Placement = pos=(-23,-47,-8) rot=(0,0,1;0rad)
  Width = 2
FEATURE [Part::Box] Box430  label="Krychle430"
  AttacherType = Attacher::AttachEngine3D
  Height = 6
  Length = 6
  Placement = pos=(-54,-45,4) rot=(0,0,1;0rad)
  Width = 2
FEATURE [Part::Box] Box431  label="Krychle431"
  AttacherType = Attacher::AttachEngine3D
  Height = 6
  Length = 6
  Placement = pos=(17,-47,-8) rot=(0,0,1;0rad)
  Width = 2
FEATURE [Part::Cylinder] Cylinder1035  label="Válec1035"
  Angle = 360
  AttacherType = Attacher::AttachEngine3D
  Height = 20
  Placement = pos=(-20,-40,-5) rot=(1,0,0;1.5708rad)
  Radius = 1.5
FEATURE [Part::Cylinder] Cylinder1036  label="Válec1036"
  Angle = 360
  AttacherType = Attacher::AttachEngine3D
  Height = 20
  Placement = pos=(20,-40,-5) rot=(1,0,0;1.5708rad)
  Radius = 1.5
FEATURE [Part::Cylinder] Cylinder1037  label="Válec1037"
  Angle = 360
  AttacherType = Attacher::AttachEngine3D
  Height = 20
  Placement = pos=(-39.6,-39.6,-10) rot=(0,0,-1;0.785398rad)
  Radius = 4
FEATURE [Part::Cylinder] Cylinder1038  label="Válec1038"
  Angle = 360
  AttacherType = Attacher::AttachEngine3D
  Height = 20
  Placement = pos=(39.6,-39.6,-10) rot=(0,0,1;0.785398rad)
  Radius = 4
FEATURE [Part::Box] Box432  label="Krychle432"
  AttacherType = Attacher::AttachEngine3D
  Height = 6
  Length = 6
  Placement = pos=(48,-45,4) rot=(0,0,1;0rad)
  Width = 2
FEATURE [Part::Compound] Compound822
  Links = -> [Cylinder1037,Cylinder1038]
FEATURE [Part::Compound] Compound823
  Links = -> [Cylinder1035,Cylinder1036,Cylinder1034,Cylinder1031]
FEATURE [Part::Compound] Compound824
  Links = -> [Box429,Box431,Box432,Box430]
FEATURE [Part::Box] Box433  label="Krychle433"
  AttacherType = Attacher::AttachEngine3D
  Height = 16
  Length = 108
  Placement = pos=(-54,-53,20) rot=(0,0,1;0rad)
  Width = 36
FEATURE [Part::Cylinder] Cylinder1039  label="Válec1039"
  Angle = 360
  AttacherType = Attacher::AttachEngine3D
  Height = 40
  Placement = pos=(59,-17,0) rot=(0,0,1;0rad)
  Radius = 10
FEATURE [Part::Compound] Compound825
  Links = -> [Cylinder1039,Cylinder1032]
FEATURE [Part::Cut] Cut432
  Base = -> Box433
  Placement = pos=(0,0,-20) rot=(0,0,1;0rad)
  Tool = -> Cylinder1033
FEATURE [Part::Cut] Cut433
  Base = -> Cut432
  Tool = -> Compound825
FEATURE [Part::Cut] Cut431
  Base = -> Cut433
  Tool = -> Compound822
FEATURE [Part::Cut] Cut430
  Base = -> Cut431
  Tool = -> Compound824
FEATURE [Part::Cut] Cut429
  Base = -> Cut430
  Tool = -> Compound823
FEATURE [Part::Box] Box434  label="Krychle434"
  AttacherType = Attacher::AttachEngine3D
  Height = 6
  Length = 6
  Placement = pos=(-54,-45,4) rot=(0,0,1;0rad)
  Width = 2
FEATURE [Part::Cylinder] Cylinder1040  label="Válec1040"
  Angle = 360
  AttacherType = Attacher::AttachEngine3D
  Height = 20
  Placement = pos=(-39.6,-39.6,-10) rot=(0,0,-1;0.785398rad)
  Radius = 4
FEATURE [Part::Cylinder] Cylinder1041  label="Válec1041"
  Angle = 360
  AttacherType = Attacher::AttachEngine3D
  Height = 40
  Placement = pos=(59,-17,0) rot=(0,0,1;0rad)
  Radius = 10
FEATURE [Part::Box] Box435  label="Krychle435"
  AttacherType = Attacher::AttachEngine3D
  Height = 6
  Length = 6
  Placement = pos=(21,-47,-8) rot=(0,0,1;0rad)
  Width = 2
FEATURE [Part::Box] Box436  label="Krychle436"
  AttacherType = Attacher::AttachEngine3D
  Height = 6
  Length = 6
  Placement = pos=(48,-45,4) rot=(0,0,1;0rad)
  Width = 2
FEATURE [Part::Box] Box437  label="Krychle437"
  AttacherType = Attacher::AttachEngine3D
  Height = 6
  Length = 6
  Placement = pos=(-27,-47,-8) rot=(0,0,1;0rad)
  Width = 2
FEATURE [Part::Box] Box438  label="Krychle438"
  AttacherType = Attacher::AttachEngine3D
  Height = 8
  Length = 108
  Placement = pos=(-54,-53,20) rot=(0,0,1;0rad)
  Width = 36
FEATURE [Part::Cylinder] Cylinder1042  label="Válec1042"
  Angle = 360
  AttacherType = Attacher::AttachEngine3D
  Height = 8
  Placement = pos=(0,0,20) rot=(0,0,1;0rad)
  Radius = 52
FEATURE [Part::Cylinder] Cylinder1043  label="Válec1043"
  Angle = 360
  AttacherType = Attacher::AttachEngine3D
  Height = 40
  Placement = pos=(-59,-17,0) rot=(0,0,1;0rad)
  Radius = 10
FEATURE [Part::Cylinder] Cylinder1044  label="Válec1044"
  Angle = 360
  AttacherType = Attacher::AttachEngine3D
  Height = 20
  Placement = pos=(-51,-40,7) rot=(1,0,0;1.5708rad)
  Radius = 1.5
FEATURE [Part::Cylinder] Cylinder1045  label="Válec1045"
  Angle = 360
  AttacherType = Attacher::AttachEngine3D
  Height = 20
  Placement = pos=(39.6,-39.6,-10) rot=(0,0,1;0.785398rad)
  Radius = 4
FEATURE [Part::Cylinder] Cylinder1046  label="Válec1046"
  Angle = 360
  AttacherType = Attacher::AttachEngine3D
  Height = 20
  Placement = pos=(24,-40,-5) rot=(1,0,0;1.5708rad)
  Radius = 1.5
FEATURE [Part::Cylinder] Cylinder1047  label="Válec1047"
  Angle = 360
  AttacherType = Attacher::AttachEngine3D
  Height = 20
  Placement = pos=(51,-40,7) rot=(1,0,0;1.5708rad)
  Radius = 1.5
FEATURE [Part::Cylinder] Cylinder1048  label="Válec1048"
  Angle = 360
  AttacherType = Attacher::AttachEngine3D
  Height = 20
  Placement = pos=(-24,-40,-5) rot=(1,0,0;1.5708rad)
  Radius = 1.5
FEATURE [Part::Cut] Cut435
  Base = -> Box438
  Placement = pos=(0,0,-20) rot=(0,0,1;0rad)
  Tool = -> Cylinder1042
FEATURE [Part::Compound] Compound826
  Links = -> [Box437,Box435,Box436,Box434]
FEATURE [Part::Compound] Compound827
  Links = -> [Cylinder1048,Cylinder1046,Cylinder1047,Cylinder1044]
FEATURE [Part::Compound] Compound828
  Links = -> [Cylinder1041,Cylinder1043]
FEATURE [Part::Compound] Compound829
  Links = -> [Cylinder1040,Cylinder1045]
FEATURE [Part::Cut] Cut438
  Base = -> Cut435
  Placement = pos=(0,0,-8) rot=(0,0,1;0rad)
  Tool = -> Compound828
FEATURE [Part::Cut] Cut436
  Base = -> Cut438
  Tool = -> Compound829
FEATURE [Part::Cut] Cut437
  Base = -> Cut436
  Tool = -> Compound826
FEATURE [Part::Cut] Cut434
  Base = -> Cut437
  Tool = -> Compound827
FEATURE [Part::Fillet] Fillet016
  Base = -> Cut434
  Edges = 2 edges r=12: [Edge2,Edge38]
FEATURE [Part::Fillet] Fillet
  Base = -> Cut429
  Edges = 2 edges r=12: [Edge3,Edge36]
FEATURE [Part::Cylinder] Cylinder1049  label="Válec1049"
  Angle = 360
  AttacherType = Attacher::AttachEngine3D
  Height = 50
  Placement = pos=(-39.598,39.598,2) rot=(0,0,1;3.92699rad)
  Radius = 1.5
FEATURE [Part::Box] Box439  label="Krychle439"
  AttacherType = Attacher::AttachEngine3D
  Height = 16
  Length = 10
  Placement = pos=(50,-43,10) rot=(0,0,1;0rad)
  Width = 43
FEATURE [Part::Cylinder] Cylinder1050  label="Válec1050"
  Angle = 360
  AttacherType = Attacher::AttachEngine3D
  Height = 50
  Placement = pos=(39.598,39.598,2) rot=(0,0,1;2.35619rad)
  Radius = 1.5
FEATURE [Part::Cylinder] Cylinder1051  label="Válec1051"
  Angle = 360
  AttacherType = Attacher::AttachEngine3D
  Height = 50
  Placement = pos=(0,-56,2) rot=(0,0,1;0rad)
  Radius = 1.5
FEATURE [Part::Cylinder] Cylinder1052  label="Válec1052"
  Angle = 360
  AttacherType = Attacher::AttachEngine3D
  Height = 16
  Placement = pos=(60,-43,10) rot=(0,0,1;0rad)
  Radius = 6
FEATURE [Part::Cylinder] Cylinder1053  label="Válec1053"
  Angle = 360
  AttacherType = Attacher::AttachEngine3D
  Height = 50
  Placement = pos=(-39.598,-39.598,2) rot=(0,0,-1;0.785398rad)
  Radius = 1.5
FEATURE [Part::Box] Box440  label="Krychle440"
  AttacherType = Attacher::AttachEngine3D
  Height = 16
  Length = 10
  Placement = pos=(-60,-43,10) rot=(0,0,1;0rad)
  Width = 43
FEATURE [Part::Compound] Compound832
  Links = -> [Box440,Box439]
FEATURE [Part::Cylinder] Cylinder1054  label="Válec1054"
  Angle = 360
  AttacherType = Attacher::AttachEngine3D
  Height = 50
  Placement = pos=(56,0,2) rot=(0,0,1;1.5708rad)
  Radius = 1.5
FEATURE [Part::Cylinder] Cylinder1055  label="Válec1055"
  Angle = 360
  AttacherType = Attacher::AttachEngine3D
  Height = 50
  Placement = pos=(-1.2e-14,56,2) rot=(0,0,1;3.14159rad)
  Radius = 1.5
FEATURE [Part::Cylinder] Cylinder1056  label="Válec1056"
  Angle = 360
  AttacherType = Attacher::AttachEngine3D
  Height = 50
  Placement = pos=(-56,-1.3e-14,2) rot=(0,0,-1;1.5708rad)
  Radius = 1.5
FEATURE [Part::Cylinder] Cylinder1057  label="Válec1057"
  Angle = 360
  AttacherType = Attacher::AttachEngine3D
  Height = 16
  Placement = pos=(-60,-43,10) rot=(0,0,1;0rad)
  Radius = 6
FEATURE [Part::Compound] Compound831
  Links = -> [Cylinder1052,Cylinder1057]
FEATURE [Part::Cylinder] Cylinder1058  label="Válec1058"
  Angle = 360
  AttacherType = Attacher::AttachEngine3D
  Height = 50
  Placement = pos=(39.598,-39.598,2) rot=(0,0,1;0.785398rad)
  Radius = 1.5
FEATURE [Part::Compound] Compound830
  Links = -> [Cylinder1051,Cylinder1058,Cylinder1054,Cylinder1050,Cylinder1055,Cylinder1049,Cylinder1056,Cylinder1053]
FEATURE [Part::Cut] Cut439
  Base = -> Compound832
  Tool = -> Compound830
FEATURE [Part::Cut] Cut440
  Base = -> Cut439
  Tool = -> Compound831
FEATURE [Part::Fillet] Fillet017
  Base = -> Cut440
  Edges = 2 edges r=8: [Edge4,Edge43]
  Placement = pos=(0,0,6) rot=(0,0,1;0rad)
FEATURE [Part::Torus] Torus002  label="Anuloid002"
  Angle1 = -180
  Angle2 = 180
  Angle3 = 360
  AttacherType = Attacher::AttachEngine3D
  Placement = pos=(0,0,29) rot=(0,0,1;0rad)
  Radius1 = 51.9
  Radius2 = 3.1
FEATURE [Part::FeaturePython] Tube009  # WARN: FeaturePython — macro-defined, semantics opaque (R4)
  AttacherType = Attacher::AttachEngine3D
  Height = 17
  InnerRadius = 53
  OuterRadius = 60
  Placement = pos=(0,0,20) rot=(0,0,1;0rad)
FEATURE [Part::Cylinder] Cylinder119  label="Válec119"
  Angle = 360
  AttacherType = Attacher::AttachEngine3D
  Height = 10
  Placement = pos=(-47,0,30) rot=(0,0,1;0rad)
  Radius = 3.5
FEATURE [Part::Cut] Cut054
  Base = -> Tube009
  Tool = -> Torus002
FEATURE [Part::Cut] Cut055
  Base = -> Cut054
  Tool = -> Cylinder119
FEATURE [Part::Cylinder] Cylinder187  label="Válec187"
  Angle = 360
  AttacherType = Attacher::AttachEngine3D
  Height = 20
  Placement = pos=(-52.3,0,29) rot=(0,0,1;0rad)
  Radius = 3.5
FEATURE [Part::Cut] Cut084  label="J-max_lozo-harmo1"
  Base = -> Cut055
  Tool = -> Cylinder187
FEATURE [Part::Cylinder] Cylinder196  label="Válec196"
  Angle = 360
  AttacherType = Attacher::AttachEngine3D
  Height = 20
  Placement = pos=(0,-56,2) rot=(0,0,1;0rad)
  Radius = 1.5
FEATURE [Part::Cylinder] Cylinder197  label="Válec197"
  Angle = 360
  AttacherType = Attacher::AttachEngine3D
  Height = 20
  Placement = pos=(39.598,-39.598,2) rot=(0,0,1;0.785398rad)
  Radius = 1.5
FEATURE [Part::Cylinder] Cylinder198  label="Válec198"
  Angle = 360
  AttacherType = Attacher::AttachEngine3D
  Height = 20
  Placement = pos=(56,0,2) rot=(0,0,1;1.5708rad)
  Radius = 1.5
FEATURE [Part::Cylinder] Cylinder199  label="Válec199"
  Angle = 360
  AttacherType = Attacher::AttachEngine3D
  Height = 20
  Placement = pos=(39.598,39.598,2) rot=(0,0,1;2.35619rad)
  Radius = 1.5
FEATURE [Part::Cylinder] Cylinder200  label="Válec200"
  Angle = 360
  AttacherType = Attacher::AttachEngine3D
  Height = 20
  Placement = pos=(-1.2e-14,56,2) rot=(0,0,1;3.14159rad)
  Radius = 1.5
FEATURE [Part::Cylinder] Cylinder201  label="Válec201"
  Angle = 360
  AttacherType = Attacher::AttachEngine3D
  Height = 20
  Placement = pos=(-39.598,39.598,2) rot=(0,0,1;3.92699rad)
  Radius = 1.5
FEATURE [Part::Cylinder] Cylinder202  label="Válec202"
  Angle = 360
  AttacherType = Attacher::AttachEngine3D
  Height = 20
  Placement = pos=(-56,-1.3e-14,2) rot=(0,0,-1;1.5708rad)
  Radius = 1.5
FEATURE [Part::Cylinder] Cylinder203  label="Válec203"
  Angle = 360
  AttacherType = Attacher::AttachEngine3D
  Height = 20
  Placement = pos=(-39.598,-39.598,2) rot=(0,0,-1;0.785398rad)
  Radius = 1.5
FEATURE [Part::Compound] Compound186
  Links = -> [Cylinder196,Cylinder197,Cylinder198,Cylinder199,Cylinder200,Cylinder201,Cylinder202,Cylinder203]
  Placement = pos=(0,0,5) rot=(0,0,1;0rad)
FEATURE [Part::Cut] Cut087
  Base = -> Cut084
  Tool = -> Compound186
FEATURE [Part::Box] Box077  label="Krychle077"
  AttacherType = Attacher::AttachEngine3D
  Height = 2
  Length = 6
  Placement = pos=(-3,-60,23) rot=(0,0,1;0rad)
  Width = 8
FEATURE [Part::Box] Box078  label="Krychle078"
  AttacherType = Attacher::AttachEngine3D
  Height = 2
  Length = 6
  Placement = pos=(40.3051,-44.5477,23) rot=(0,0,1;0.785398rad)
  Width = 8
FEATURE [Part::Box] Box079  label="Krychle079"
  AttacherType = Attacher::AttachEngine3D
  Height = 2
  Length = 6
  Placement = pos=(60,-3,23) rot=(0,0,1;1.5708rad)
  Width = 8
FEATURE [Part::Box] Box080  label="Krychle080"
  AttacherType = Attacher::AttachEngine3D
  Height = 2
  Length = 6
  Placement = pos=(44.5477,40.3051,23) rot=(0,0,1;2.35619rad)
  Width = 8
FEATURE [Part::Box] Box081  label="Krychle081"
  AttacherType = Attacher::AttachEngine3D
  Height = 2
  Length = 6
  Placement = pos=(3,60,23) rot=(0,0,1;3.14159rad)
  Width = 8
FEATURE [Part::Box] Box082  label="Krychle082"
  AttacherType = Attacher::AttachEngine3D
  Height = 2
  Length = 6
  Placement = pos=(-40.3051,44.5477,23) rot=(0,0,1;3.92699rad)
  Width = 8
FEATURE [Part::Box] Box083  label="Krychle083"
  AttacherType = Attacher::AttachEngine3D
  Height = 2
  Length = 6
  Placement = pos=(-60,3,23) rot=(0,0,-1;1.5708rad)
  Width = 8
FEATURE [Part::Box] Box084  label="Krychle084"
  AttacherType = Attacher::AttachEngine3D
  Height = 2
  Length = 6
  Placement = pos=(-44.5477,-40.3051,23) rot=(0,0,-1;0.785398rad)
  Width = 8
FEATURE [Part::Compound] Compound187
  Links = -> [Box077,Box078,Box079,Box080,Box081,Box082,Box083,Box084]
FEATURE [Part::Cut] Cut088  label="J-max_lozo-harmo2"
  Base = -> Cut087
  Tool = -> Compound187
FEATURE [Part::Cylinder] Cylinder204  label="Válec204"
  Angle = 360
  AttacherType = Attacher::AttachEngine3D
  Height = 17
  Placement = pos=(0,0,20) rot=(0,0,1;0rad)
  Radius = 60
FEATURE [Part::Box] Box085  label="Krychle085"
  AttacherType = Attacher::AttachEngine3D
  Height = 17
  Length = 108
  Placement = pos=(-54,-53,20) rot=(0,0,1;0rad)
  Width = 46
FEATURE [Part::Box] Box086  label="Krychle086"
  AttacherType = Attacher::AttachEngine3D
  Height = 6
  Length = 6
  Placement = pos=(48,-45,22) rot=(0,0,1;0rad)
  Width = 2
FEATURE [Part::Box] Box087  label="Krychle087"
  AttacherType = Attacher::AttachEngine3D
  Height = 6
  Length = 6
  Placement = pos=(-54,-45,22) rot=(0,0,1;0rad)
  Width = 2
FEATURE [Part::Compound] Compound189
  Links = -> [Box086,Box087]
FEATURE [Part::Cut] Cut089
  Base = -> Box085
  Tool = -> Cylinder204
FEATURE [Part::Cut] Cut090
  Base = -> Cut089
  Tool = -> Compound189
FEATURE [Part::Cylinder] Cylinder205  label="Válec205"
  Angle = 360
  AttacherType = Attacher::AttachEngine3D
  Height = 20
  Placement = pos=(-51,-40,25) rot=(1,0,0;1.5708rad)
  Radius = 1.5
FEATURE [Part::Cylinder] Cylinder206  label="Válec206"
  Angle = 360
  AttacherType = Attacher::AttachEngine3D
  Height = 20
  Placement = pos=(51,-40,25) rot=(1,0,0;1.5708rad)
  Radius = 1.5
FEATURE [Part::Compound] Compound190
  Links = -> [Cylinder205,Cylinder206]
  Placement = pos=(0,2,0) rot=(0,0,1;0rad)
FEATURE [Part::Cut] Cut091
  Base = -> Cut090
  Tool = -> Compound190
FEATURE [Part::Box] Box088  label="Krychle088"
  AttacherType = Attacher::AttachEngine3D
  Height = 6
  Length = 6
  Placement = pos=(36,-45,31) rot=(0,0,1;0rad)
  Width = 2
FEATURE [Part::Box] Box089  label="Krychle089"
  AttacherType = Attacher::AttachEngine3D
  Height = 6
  Length = 6
  Placement = pos=(-42,-45,31) rot=(0,0,1;0rad)
  Width = 2
FEATURE [Part::Compound] Compound191
  Links = -> [Box088,Box089]
FEATURE [Part::Box] Box090  label="Krychle090"
  AttacherType = Attacher::AttachEngine3D
  Height = 6
  Length = 6
  Placement = pos=(36,-45,31) rot=(0,0,1;0rad)
  Width = 2
FEATURE [Part::Box] Box091  label="Krychle091"
  AttacherType = Attacher::AttachEngine3D
  Height = 6
  Length = 6
  Placement = pos=(-42,-45,31) rot=(0,0,1;0rad)
  Width = 2
FEATURE [Part::Compound] Compound192
  Links = -> [Box090,Box091]
FEATURE [Part::Cylinder] Cylinder207  label="Válec207"
  Angle = 360
  AttacherType = Attacher::AttachEngine3D
  Height = 20
  Placement = pos=(-39,-40,34) rot=(1,0,0;1.5708rad)
  Radius = 1.5
FEATURE [Part::Cylinder] Cylinder208  label="Válec208"
  Angle = 360
  AttacherType = Attacher::AttachEngine3D
  Height = 20
  Placement = pos=(39,-40,34) rot=(1,0,0;1.5708rad)
  Radius = 1.5
FEATURE [Part::Cylinder] Cylinder209  label="Válec209"
  Angle = 360
  AttacherType = Attacher::AttachEngine3D
  Height = 20
  Placement = pos=(-39,-40,34) rot=(1,0,0;1.5708rad)
  Radius = 1.5
FEATURE [Part::Cylinder] Cylinder210  label="Válec210"
  Angle = 360
  AttacherType = Attacher::AttachEngine3D
  Height = 20
  Placement = pos=(39,-40,34) rot=(1,0,0;1.5708rad)
  Radius = 1.5
FEATURE [Part::Compound] Compound193
  Links = -> [Cylinder207,Cylinder208]
FEATURE [Part::Cut] Cut092
  Base = -> Cut088
  Tool = -> Compound193
FEATURE [Part::Cut] Cut093
  Base = -> Cut092
  Tool = -> Compound191
FEATURE [Part::Compound] Compound194
  Links = -> [Cylinder209,Cylinder210]
FEATURE [Part::Cut] Cut094
  Base = -> Cut091
  Tool = -> Compound192
FEATURE [Part::Cut] Cut095
  Base = -> Cut094
  Tool = -> Compound194
FEATURE [Part::Compound] Compound195  label="J-max_lozo-harmo4"
  Links = -> [Cut093,Cut095]
FEATURE [Part::Box] Box110  label="Krychle110"
  AttacherType = Attacher::AttachEngine3D
  Height = 2
  Length = 6
  Placement = pos=(3,62,23) rot=(0,0,1;3.14159rad)
  Width = 10
FEATURE [Part::Box] Box111  label="Krychle111"
  AttacherType = Attacher::AttachEngine3D
  Height = 2
  Length = 6
  Placement = pos=(-41.7193,45.9619,23) rot=(0,0,1;3.92699rad)
  Width = 10
FEATURE [Part::Box] Box112  label="Krychle112"
  AttacherType = Attacher::AttachEngine3D
  Height = 2
  Length = 6
  Placement = pos=(-62,3,23) rot=(0,0,-1;1.5708rad)
  Width = 10
FEATURE [Part::Box] Box113  label="Krychle113"
  AttacherType = Attacher::AttachEngine3D
  Height = 2
  Length = 6
  Placement = pos=(-45.9619,-41.7193,23) rot=(0,0,-1;0.785398rad)
  Width = 10
FEATURE [Part::Box] Box114  label="Krychle114"
  AttacherType = Attacher::AttachEngine3D
  Height = 2
  Length = 6
  Placement = pos=(-3,-62,23) rot=(0,0,1;0rad)
  Width = 10
FEATURE [Part::Box] Box115  label="Krychle115"
  AttacherType = Attacher::AttachEngine3D
  Height = 2
  Length = 6
  Placement = pos=(41.7193,-45.9619,23) rot=(0,0,1;0.785398rad)
  Width = 10
FEATURE [Part::Box] Box116  label="Krychle116"
  AttacherType = Attacher::AttachEngine3D
  Height = 2
  Length = 6
  Placement = pos=(62,-3,23) rot=(0,0,1;1.5708rad)
  Width = 10
FEATURE [Part::Box] Box117  label="Krychle117"
  AttacherType = Attacher::AttachEngine3D
  Height = 2
  Length = 6
  Placement = pos=(45.9619,41.7193,23) rot=(0,0,1;2.35619rad)
  Width = 10
FEATURE [Part::Cylinder] Cylinder310  label="Válec310"
  Angle = 360
  AttacherType = Attacher::AttachEngine3D
  Height = 33
  Placement = pos=(60,-43,10) rot=(0,0,1;0rad)
  Radius = 6
FEATURE [Part::Box] Box118  label="Krychle118"
  AttacherType = Attacher::AttachEngine3D
  Height = 33
  Length = 10
  Placement = pos=(50,-43,10) rot=(0,0,1;0rad)
  Width = 43
FEATURE [Part::Box] Box119  label="Krychle119"
  AttacherType = Attacher::AttachEngine3D
  Height = 33
  Length = 10
  Placement = pos=(-60,-43,10) rot=(0,0,1;0rad)
  Width = 43
FEATURE [Part::Cylinder] Cylinder311  label="Válec311"
  Angle = 360
  AttacherType = Attacher::AttachEngine3D
  Height = 50
  Placement = pos=(39.598,39.598,2) rot=(0,0,1;2.35619rad)
  Radius = 1.5
FEATURE [Part::Cylinder] Cylinder312  label="Válec312"
  Angle = 360
  AttacherType = Attacher::AttachEngine3D
  Height = 33
  Placement = pos=(-60,-43,10) rot=(0,0,1;0rad)
  Radius = 6
FEATURE [Part::Cylinder] Cylinder313  label="Válec313"
  Angle = 360
  AttacherType = Attacher::AttachEngine3D
  Height = 50
  Placement = pos=(-39.598,39.598,2) rot=(0,0,1;3.92699rad)
  Radius = 1.5
FEATURE [Part::Cylinder] Cylinder314  label="Válec314"
  Angle = 360
  AttacherType = Attacher::AttachEngine3D
  Height = 50
  Placement = pos=(56,0,2) rot=(0,0,1;1.5708rad)
  Radius = 1.5
FEATURE [Part::Cylinder] Cylinder315  label="Válec315"
  Angle = 360
  AttacherType = Attacher::AttachEngine3D
  Height = 50
  Placement = pos=(-1.2e-14,56,2) rot=(0,0,1;3.14159rad)
  Radius = 1.5
FEATURE [Part::Cylinder] Cylinder316  label="Válec316"
  Angle = 360
  AttacherType = Attacher::AttachEngine3D
  Height = 50
  Placement = pos=(-56,-1.3e-14,2) rot=(0,0,-1;1.5708rad)
  Radius = 1.5
FEATURE [Part::Cylinder] Cylinder317  label="Válec317"
  Angle = 360
  AttacherType = Attacher::AttachEngine3D
  Height = 50
  Placement = pos=(0,-56,2) rot=(0,0,1;0rad)
  Radius = 1.5
FEATURE [Part::Cylinder] Cylinder318  label="Válec318"
  Angle = 360
  AttacherType = Attacher::AttachEngine3D
  Height = 50
  Placement = pos=(39.598,-39.598,2) rot=(0,0,1;0.785398rad)
  Radius = 1.5
FEATURE [Part::Cylinder] Cylinder319  label="Válec319"
  Angle = 360
  AttacherType = Attacher::AttachEngine3D
  Height = 50
  Placement = pos=(-39.598,-39.598,2) rot=(0,0,-1;0.785398rad)
  Radius = 1.5
FEATURE [Part::Cylinder] Cylinder320  label="Válec320"
  Angle = 360
  AttacherType = Attacher::AttachEngine3D
  Height = 33
  Placement = pos=(0,0,20) rot=(0,0,1;0rad)
  Radius = 60
FEATURE [Part::Cylinder] Cylinder321  label="Válec321"
  Angle = 360
  AttacherType = Attacher::AttachEngine3D
  Height = 22
  Placement = pos=(-51,-40,25) rot=(1,0,0;1.5708rad)
  Radius = 1.5
FEATURE [Part::Cylinder] Cylinder322  label="Válec322"
  Angle = 360
  AttacherType = Attacher::AttachEngine3D
  Height = 20
  Placement = pos=(51,-40,25) rot=(1,0,0;1.5708rad)
  Radius = 1.5
FEATURE [Part::Compound] Compound243
  Links = -> [Box110,Box111,Box112,Box113,Box114,Box115,Box116,Box117]
FEATURE [Part::Compound] Compound244
  Links = -> [Box119,Box118]
FEATURE [Part::Compound] Compound245
  Links = -> [Cylinder317,Cylinder318,Cylinder314,Cylinder311,Cylinder315,Cylinder313,Cylinder316,Cylinder319]
FEATURE [Part::Cut] Cut132
  Base = -> Compound244
  Tool = -> Compound245
FEATURE [Part::Compound] Compound246
  Links = -> [Cylinder310,Cylinder312]
FEATURE [Part::Cut] Cut131
  Base = -> Cut132
  Placement = pos=(0,0,10) rot=(0,0,1;0rad)
  Tool = -> Compound246
FEATURE [Part::Compound] Compound247
  Links = -> [Cylinder321,Cylinder322]
  Placement = pos=(0,2,0) rot=(0,0,1;0rad)
FEATURE [Part::Cut] Cut133
  Base = -> Cut131
  Tool = -> Cylinder320
FEATURE [Part::Cut] Cut134
  Base = -> Cut133
  Tool = -> Compound243
FEATURE [Part::Cut] Cut135
  Base = -> Cut134
  Placement = pos=(0,0,16) rot=(0,0,1;0rad)
  Tool = -> Compound247
FEATURE [Sketcher::SketchObject] Sketch001
  FullyConstrained = false
  MapMode = 5
  Support = -> [XY_Plane001]
  sketch-geometry (5):
    g0: LineSegment StartX=-51.8839 StartY=28.0157 StartZ=0 EndX=-9.41248 EndY=122.349 EndZ=0
    g1: LineSegment StartX=-9.41248 StartY=122.349 StartZ=0 EndX=9.41746 EndY=122.349 EndZ=0
    g2: LineSegment StartX=9.41746 StartY=122.349 StartZ=0 EndX=51.7746 EndY=28.1985 EndZ=0
    g3: LineSegment StartX=51.7746 StartY=28.1985 StartZ=0 EndX=0 EndY=55.1408 EndZ=0
    g4: LineSegment StartX=0 StartY=55.1408 StartZ=0 EndX=-51.8839 EndY=28.0157 EndZ=0
  constraints (7):
    c: Coincident(g0,g1)
    c: Horizontal(g1)
    c: Coincident(g1,g2)
    c: Coincident(g2,g3)
    c: PointOnObject(g3,g-2)
    c: Coincident(g3,g4)
    c: Coincident(g4,g0)
FEATURE [PartDesign::Pad] Pad001
  Direction = (1,1,1)
  Length = 10
  Length2 = 100
  Profile = -> Sketch001
  Type = 0
FEATURE [PartDesign::Body] Body001
  Group = -> [Sketch001,Pad001]
  Origin = -> Origin001
  Tip = -> Pad001
FEATURE [Part::FeaturePython] Tube001  # WARN: FeaturePython — macro-defined, semantics opaque (R4)
  AttacherType = Attacher::AttachEngine3D
  Height = 10
  InnerRadius = 40
  OuterRadius = 59
FEATURE [Part::Cylinder] Cylinder534  label="Válec534"
  Angle = 360
  AttacherType = Attacher::AttachEngine3D
  Height = 10
  Placement = pos=(0,106,0) rot=(0,0,1;0rad)
  Radius = 10
FEATURE [Part::Box] Box139  label="Krychle139"
  AttacherType = Attacher::AttachEngine3D
  Height = 32
  Length = 200
  Placement = pos=(-100,-124,0) rot=(0,0,1;0rad)
  Width = 100
FEATURE [Part::Box] Box140  label="Krychle140"
  AttacherType = Attacher::AttachEngine3D
  Height = 10
  Length = 10
  Placement = pos=(32,-24,0) rot=(0,0,1;0rad)
  Width = 52
FEATURE [Part::Cylinder] Cylinder535  label="Válec535"
  Angle = 360
  AttacherType = Attacher::AttachEngine3D
  Height = 100
  Placement = pos=(51,-12,0) rot=(0,0,1;0rad)
  Radius = 1.5
FEATURE [Part::Box] Box141  label="Krychle141"
  AttacherType = Attacher::AttachEngine3D
  Height = 10
  Length = 10
  Placement = pos=(-42,-24,0) rot=(0,0,1;0rad)
  Width = 52
FEATURE [Part::Box] Box142  label="Krychle142"
  AttacherType = Attacher::AttachEngine3D
  Height = 10
  Length = 72
  Placement = pos=(-36,-24,0) rot=(0,0,1;0rad)
  Width = 70
FEATURE [Part::Cylinder] Cylinder538  label="Válec538"
  Angle = 360
  AttacherType = Attacher::AttachEngine3D
  Height = 100
  Placement = pos=(-51,-12,0) rot=(0,0,1;0rad)
  Radius = 1.5
FEATURE [Part::Compound] Compound323
  Links = -> [Cylinder538,Cylinder535]
FEATURE [Part::Cylinder] Cylinder544  label="Válec544"
  Angle = 360
  AttacherType = Attacher::AttachEngine3D
  Height = 50
  Placement = pos=(-51,6,0) rot=(0,0,1;0rad)
  Radius = 1.5
FEATURE [Part::Cylinder] Cylinder549  label="Válec549"
  Angle = 360
  AttacherType = Attacher::AttachEngine3D
  Height = 50
  Placement = pos=(51,6,0) rot=(0,0,1;0rad)
  Radius = 1.5
FEATURE [Part::Cylinder] Cylinder550  label="Válec550"
  Angle = 360
  AttacherType = Attacher::AttachEngine3D
  Height = 50
  Placement = pos=(-24,18,0) rot=(0,0,1;0rad)
  Radius = 1.5
FEATURE [Part::Cylinder] Cylinder556  label="Válec556"
  Angle = 360
  AttacherType = Attacher::AttachEngine3D
  Height = 50
  Placement = pos=(24,18,0) rot=(0,0,1;0rad)
  Radius = 1.5
FEATURE [Part::Compound] Compound324
  Links = -> [Cylinder549,Cylinder544,Cylinder550,Cylinder556]
FEATURE [Part::Cylinder] Cylinder563  label="Válec563"
  Angle = 360
  AttacherType = Attacher::AttachEngine3D
  Height = 4
  Placement = pos=(-7,-34,73) rot=(1,0,0;1.5708rad)
  Radius = 3
FEATURE [Part::Cylinder] Cylinder564  label="Válec564"
  Angle = 360
  AttacherType = Attacher::AttachEngine3D
  Height = 20
  Placement = pos=(7,-34,37) rot=(1,0,0;1.5708rad)
  Radius = 1.5
FEATURE [Part::Cylinder] Cylinder565  label="Válec565"
  Angle = 360
  AttacherType = Attacher::AttachEngine3D
  Height = 20
  Placement = pos=(7,-34,73) rot=(1,0,0;1.5708rad)
  Radius = 1.5
FEATURE [Part::Cylinder] Cylinder566  label="Válec566"
  Angle = 360
  AttacherType = Attacher::AttachEngine3D
  Height = 20
  Placement = pos=(-7,-34,37) rot=(1,0,0;1.5708rad)
  Radius = 1.5
FEATURE [Part::Cylinder] Cylinder567  label="Válec567"
  Angle = 360
  AttacherType = Attacher::AttachEngine3D
  Height = 20
  Placement = pos=(-7,-34,73) rot=(1,0,0;1.5708rad)
  Radius = 1.5
FEATURE [Part::Compound] Compound333
  Links = -> [Cylinder564,Cylinder566,Cylinder565,Cylinder567]
  Placement = pos=(0,141,45) rot=(1,0,0;1.5708rad)
FEATURE [Part::Cut] Cut189
  Base = -> Cylinder534
  Tool = -> Compound333
FEATURE [Part::Cylinder] Cylinder568  label="Válec568"
  Angle = 360
  AttacherType = Attacher::AttachEngine3D
  Height = 4
  Placement = pos=(-7,-34,37) rot=(1,0,0;1.5708rad)
  Radius = 3
FEATURE [Part::Cylinder] Cylinder569  label="Válec569"
  Angle = 360
  AttacherType = Attacher::AttachEngine3D
  Height = 4
  Placement = pos=(7,-34,73) rot=(1,0,0;1.5708rad)
  Radius = 3
FEATURE [Part::Cylinder] Cylinder570  label="Válec570"
  Angle = 360
  AttacherType = Attacher::AttachEngine3D
  Height = 4
  Placement = pos=(7,-34,37) rot=(1,0,0;1.5708rad)
  Radius = 3
FEATURE [Part::Compound] Compound332
  Links = -> [Cylinder570,Cylinder568,Cylinder569,Cylinder563]
  Placement = pos=(0,141,45) rot=(1,0,0;1.5708rad)
FEATURE [Part::Cut] Cut190
  Base = -> Cut189
  Placement = pos=(0,13,0) rot=(0,0,1;0rad)
  Tool = -> Compound332
FEATURE [Part::Cylinder] Cylinder575  label="Válec575"
  Angle = 360
  AttacherType = Attacher::AttachEngine3D
  Height = 4
  Placement = pos=(7,-34,37) rot=(1,0,0;1.5708rad)
  Radius = 3
FEATURE [Part::Cylinder] Cylinder576  label="Válec576"
  Angle = 360
  AttacherType = Attacher::AttachEngine3D
  Height = 20
  Placement = pos=(-7,-34,37) rot=(1,0,0;1.5708rad)
  Radius = 1.5
FEATURE [Part::Cylinder] Cylinder577  label="Válec577"
  Angle = 360
  AttacherType = Attacher::AttachEngine3D
  Height = 20
  Placement = pos=(7,-34,37) rot=(1,0,0;1.5708rad)
  Radius = 1.5
FEATURE [Part::Compound] Compound341
  Links = -> [Box140,Box141]
FEATURE [Part::Cylinder] Cylinder578  label="Válec578"
  Angle = 360
  AttacherType = Attacher::AttachEngine3D
  Height = 20
  Placement = pos=(7,-34,73) rot=(1,0,0;1.5708rad)
  Radius = 1.5
FEATURE [Part::Cylinder] Cylinder579  label="Válec579"
  Angle = 360
  AttacherType = Attacher::AttachEngine3D
  Height = 20
  Placement = pos=(-7,-34,73) rot=(1,0,0;1.5708rad)
  Radius = 1.5
FEATURE [Part::Compound] Compound337
  Links = -> [Cylinder577,Cylinder576,Cylinder578,Cylinder579]
  Placement = pos=(0,154,45) rot=(1,0,0;1.5708rad)
FEATURE [Part::Cylinder] Cylinder580  label="Válec580"
  Angle = 360
  AttacherType = Attacher::AttachEngine3D
  Height = 4
  Placement = pos=(-7,-34,73) rot=(1,0,0;1.5708rad)
  Radius = 3
FEATURE [Part::Cylinder] Cylinder581  label="Válec581"
  Angle = 360
  AttacherType = Attacher::AttachEngine3D
  Height = 4
  Placement = pos=(-7,-34,37) rot=(1,0,0;1.5708rad)
  Radius = 3
FEATURE [Part::Cylinder] Cylinder582  label="Válec582"
  Angle = 360
  AttacherType = Attacher::AttachEngine3D
  Height = 4
  Placement = pos=(7,-34,73) rot=(1,0,0;1.5708rad)
  Radius = 3
FEATURE [Part::Compound] Compound338
  Links = -> [Cylinder575,Cylinder581,Cylinder582,Cylinder580]
  Placement = pos=(0,154,45) rot=(1,0,0;1.5708rad)
FEATURE [Part::Cylinder] Cylinder583  label="Válec583"
  Angle = 360
  AttacherType = Attacher::AttachEngine3D
  Height = 100
  Placement = pos=(39,-21,0) rot=(0,0,1;0rad)
  Radius = 1.5
FEATURE [Part::Cylinder] Cylinder584  label="Válec584"
  Angle = 360
  AttacherType = Attacher::AttachEngine3D
  Height = 100
  Placement = pos=(-39,-21,0) rot=(0,0,1;0rad)
  Radius = 1.5
FEATURE [Part::Compound] Compound339
  Links = -> [Cylinder584,Cylinder583]
FEATURE [Part::Cylinder] Cylinder585  label="Válec585"
  Angle = 360
  AttacherType = Attacher::AttachEngine3D
  Height = 100
  Placement = pos=(-39,-21,0) rot=(0,0,1;0rad)
  Radius = 1.5
FEATURE [Part::Cylinder] Cylinder586  label="Válec586"
  Angle = 360
  AttacherType = Attacher::AttachEngine3D
  Height = 100
  Placement = pos=(39,-21,0) rot=(0,0,1;0rad)
  Radius = 1.5
FEATURE [Part::Compound] Compound340
  Links = -> [Cylinder585,Cylinder586]
FEATURE [Part::Cut] Cut173
  Base = -> Compound341
  Tool = -> Compound340
FEATURE [Part::Box] Box236  label="Krychle236"
  AttacherType = Attacher::AttachEngine3D
  Height = 64
  Length = 6
  Placement = pos=(11,-3,-93) rot=(0,0,1;0rad)
  Width = 6
FEATURE [Part::Box] Box237  label="Krychle237"
  AttacherType = Attacher::AttachEngine3D
  Height = 64
  Length = 6
  Placement = pos=(87,-3,-93) rot=(0,0,1;0rad)
  Width = 6
FEATURE [Part::Compound] Compound627
  Links = -> [Box236,Box237]
  Placement = pos=(-52,0,36) rot=(0,0,1;0rad)
FEATURE [Part::Cylinder] Cylinder1238  label="Válec1238"
  Angle = 360
  AttacherType = Attacher::AttachEngine3D
  Height = 100
  Placement = pos=(90,0,-60) rot=(0,0,1;0rad)
  Radius = 1.5
FEATURE [Part::Compound] Compound628
  Links = -> [Compound339,Compound324,Compound323]
  Placement = pos=(0,0,-10) rot=(0,0,1;0rad)
FEATURE [Part::Cylinder] Cylinder1239  label="Válec1239"
  Angle = 360
  AttacherType = Attacher::AttachEngine3D
  Height = 100
  Placement = pos=(14,0,-60) rot=(0,0,1;0rad)
  Radius = 1.5
FEATURE [Part::Compound] Compound625  label="srouby_troj001"
  Links = -> [Cylinder1238,Cylinder1239]
  Placement = pos=(-52,0,0) rot=(0,0,1;0rad)
FEATURE [Part::Cylinder] Cylinder1232  label="Válec1232"
  Angle = 360
  AttacherType = Attacher::AttachEngine3D
  Height = 32
  Placement = pos=(26,41,-42) rot=(0,0,1;0rad)
  Radius = 1.5
FEATURE [Part::Cylinder] Cylinder1233  label="Válec1233"
  Angle = 360
  AttacherType = Attacher::AttachEngine3D
  Height = 32
  Placement = pos=(78,41,-42) rot=(0,0,1;0rad)
  Radius = 1.5
FEATURE [Part::Compound] Compound620
  Links = -> [Cylinder1232,Cylinder1233]
  Placement = pos=(-52,0,36) rot=(0,0,1;0rad)
FEATURE [Part::Compound] Compound630
  Links = -> [Compound625,Compound620]
FEATURE [Part::Cylinder] Cylinder1242  label="Válec1242"
  Angle = 360
  AttacherType = Attacher::AttachEngine3D
  Height = 3
  Placement = pos=(26,41,-42) rot=(0,0,1;0rad)
  Radius = 3
FEATURE [Part::Cut] Cut191
  Base = -> Tube001
  Tool = -> Box139
FEATURE [Part::Cut] Cut192
  Base = -> Body001
  Tool = -> Compound337
FEATURE [Part::Cut] Cut193
  Base = -> Cut192
  Tool = -> Compound338
FEATURE [Part::Cylinder] Cylinder1243  label="Válec1243"
  Angle = 360
  AttacherType = Attacher::AttachEngine3D
  Height = 3
  Placement = pos=(78,41,-42) rot=(0,0,1;0rad)
  Radius = 3
FEATURE [Part::Compound] Compound633
  Links = -> [Cylinder1242,Cylinder1243]
  Placement = pos=(-52,0,42) rot=(0,0,1;0rad)
FEATURE [Part::Cylinder] Cylinder1244  label="Válec1244"
  Angle = 360
  AttacherType = Attacher::AttachEngine3D
  Height = 3
  Placement = pos=(26,41,-42) rot=(0,0,1;0rad)
  Radius = 3
FEATURE [Part::Cylinder] Cylinder1245  label="Válec1245"
  Angle = 360
  AttacherType = Attacher::AttachEngine3D
  Height = 3
  Placement = pos=(78,41,-42) rot=(0,0,1;0rad)
  Radius = 3
FEATURE [Part::Cylinder] Cylinder1246  label="Válec1246"
  Angle = 360
  AttacherType = Attacher::AttachEngine3D
  Height = 100
  Placement = pos=(51,-12,0) rot=(0,0,1;0rad)
  Radius = 1.5
FEATURE [Part::Compound] Compound634
  Links = -> [Cylinder1244,Cylinder1245]
  Placement = pos=(-52,0,42) rot=(0,0,1;0rad)
FEATURE [Part::Cylinder] Cylinder1247  label="Válec1247"
  Angle = 360
  AttacherType = Attacher::AttachEngine3D
  Height = 100
  Placement = pos=(-51,-12,0) rot=(0,0,1;0rad)
  Radius = 1.5
FEATURE [Part::Compound] Compound636
  Links = -> [Cylinder1247,Cylinder1246]
FEATURE [Part::Cylinder] Cylinder1248  label="Válec1248"
  Angle = 360
  AttacherType = Attacher::AttachEngine3D
  Height = 50
  Placement = pos=(-51,6,0) rot=(0,0,1;0rad)
  Radius = 1.5
FEATURE [Part::Cylinder] Cylinder1249  label="Válec1249"
  Angle = 360
  AttacherType = Attacher::AttachEngine3D
  Height = 50
  Placement = pos=(51,6,0) rot=(0,0,1;0rad)
  Radius = 1.5
FEATURE [Part::Cylinder] Cylinder1250  label="Válec1250"
  Angle = 360
  AttacherType = Attacher::AttachEngine3D
  Height = 50
  Placement = pos=(-24,18,0) rot=(0,0,1;0rad)
  Radius = 1.5
FEATURE [Part::Cylinder] Cylinder1251  label="Válec1251"
  Angle = 360
  AttacherType = Attacher::AttachEngine3D
  Height = 50
  Placement = pos=(24,18,0) rot=(0,0,1;0rad)
  Radius = 1.5
FEATURE [Part::Compound] Compound637
  Links = -> [Cylinder1249,Cylinder1248,Cylinder1250,Cylinder1251]
FEATURE [Part::Cylinder] Cylinder1252  label="Válec1252"
  Angle = 360
  AttacherType = Attacher::AttachEngine3D
  Height = 100
  Placement = pos=(39,-21,0) rot=(0,0,1;0rad)
  Radius = 1.5
FEATURE [Part::Cylinder] Cylinder1253  label="Válec1253"
  Angle = 360
  AttacherType = Attacher::AttachEngine3D
  Height = 100
  Placement = pos=(-39,-21,0) rot=(0,0,1;0rad)
  Radius = 1.5
FEATURE [Part::Compound] Compound638
  Links = -> [Cylinder1253,Cylinder1252]
FEATURE [Part::Compound] Compound635
  Links = -> [Compound638,Compound637,Compound636]
  Placement = pos=(0,0,-10) rot=(0,0,1;0rad)
FEATURE [Part::Cut] Cut194
  Base = -> Cut191
  Tool = -> Compound635
FEATURE [Part::Cylinder] Cylinder1254  label="Válec1254"
  Angle = 360
  AttacherType = Attacher::AttachEngine3D
  Height = 100
  Placement = pos=(90,0,-60) rot=(0,0,1;0rad)
  Radius = 1.5
FEATURE [Part::Cylinder] Cylinder1255  label="Válec1255"
  Angle = 360
  AttacherType = Attacher::AttachEngine3D
  Height = 100
  Placement = pos=(14,0,-60) rot=(0,0,1;0rad)
  Radius = 1.5
FEATURE [Part::Cylinder] Cylinder1256  label="Válec1256"
  Angle = 360
  AttacherType = Attacher::AttachEngine3D
  Height = 32
  Placement = pos=(26,41,-42) rot=(0,0,1;0rad)
  Radius = 1.5
FEATURE [Part::Cylinder] Cylinder1257  label="Válec1257"
  Angle = 360
  AttacherType = Attacher::AttachEngine3D
  Height = 32
  Placement = pos=(78,41,-42) rot=(0,0,1;0rad)
  Radius = 1.5
FEATURE [Part::Cylinder] Cylinder1258  label="Válec1258"
  Angle = 360
  AttacherType = Attacher::AttachEngine3D
  Height = 3
  Placement = pos=(26,41,-42) rot=(0,0,1;0rad)
  Radius = 3
FEATURE [Part::Compound] Compound640  label="srouby_troj002"
  Links = -> [Cylinder1254,Cylinder1255]
  Placement = pos=(-52,0,0) rot=(0,0,1;0rad)
FEATURE [Part::Compound] Compound641
  Links = -> [Cylinder1256,Cylinder1257]
  Placement = pos=(-52,0,36) rot=(0,0,1;0rad)
FEATURE [Part::Compound] Compound639
  Links = -> [Compound640,Compound641]
FEATURE [Part::Cut] Cut195
  Base = -> Cut194
  Tool = -> Compound639
FEATURE [Part::Cut] Cut196
  Base = -> Cut195
  Tool = -> Compound633
FEATURE [Part::Cut] Cut198
  Base = -> Cut196
  Tool = -> Compound627
FEATURE [Part::Cylinder] Cylinder1259  label="Válec1259"
  Angle = 360
  AttacherType = Attacher::AttachEngine3D
  Height = 3
  Placement = pos=(78,41,-42) rot=(0,0,1;0rad)
  Radius = 3
FEATURE [Part::Compound] Compound642
  Links = -> [Cylinder1258,Cylinder1259]
  Placement = pos=(-52,0,42) rot=(0,0,1;0rad)
FEATURE [Part::Cut] Cut197
  Base = -> Cut193
  Tool = -> Compound642
FEATURE [Part::Cylinder] Cylinder1260  label="Válec1260"
  Angle = 360
  AttacherType = Attacher::AttachEngine3D
  Height = 100
  Placement = pos=(90,0,-60) rot=(0,0,1;0rad)
  Radius = 1.5
FEATURE [Part::Cylinder] Cylinder1261  label="Válec1261"
  Angle = 360
  AttacherType = Attacher::AttachEngine3D
  Height = 100
  Placement = pos=(14,0,-60) rot=(0,0,1;0rad)
  Radius = 1.5
FEATURE [Part::Cylinder] Cylinder1262  label="Válec1262"
  Angle = 360
  AttacherType = Attacher::AttachEngine3D
  Height = 32
  Placement = pos=(26,41,-42) rot=(0,0,1;0rad)
  Radius = 1.5
FEATURE [Part::Compound] Compound644  label="srouby_troj003"
  Links = -> [Cylinder1260,Cylinder1261]
  Placement = pos=(-52,0,0) rot=(0,0,1;0rad)
FEATURE [Part::Cylinder] Cylinder1263  label="Válec1263"
  Angle = 360
  AttacherType = Attacher::AttachEngine3D
  Height = 32
  Placement = pos=(78,41,-42) rot=(0,0,1;0rad)
  Radius = 1.5
FEATURE [Part::Compound] Compound645
  Links = -> [Cylinder1262,Cylinder1263]
  Placement = pos=(-52,0,36) rot=(0,0,1;0rad)
FEATURE [Part::Compound] Compound643
  Links = -> [Compound644,Compound645]
FEATURE [Part::Cut] Cut199
  Base = -> Cut173
  Tool = -> Compound643
FEATURE [Part::Box] Box238  label="Krychle238"
  AttacherType = Attacher::AttachEngine3D
  Height = 64
  Length = 6
  Placement = pos=(11,-3,-93) rot=(0,0,1;0rad)
  Width = 6
FEATURE [Part::Box] Box239  label="Krychle239"
  AttacherType = Attacher::AttachEngine3D
  Height = 64
  Length = 6
  Placement = pos=(87,-3,-93) rot=(0,0,1;0rad)
  Width = 6
FEATURE [Part::Compound] Compound646
  Links = -> [Box238,Box239]
  Placement = pos=(-52,0,36) rot=(0,0,1;0rad)
FEATURE [Part::Cut] Cut200
  Base = -> Cut199
  Tool = -> Compound646
FEATURE [Part::Cylinder] Cylinder1264  label="Válec1264"
  Angle = 360
  AttacherType = Attacher::AttachEngine3D
  Height = 100
  Placement = pos=(90,0,-60) rot=(0,0,1;0rad)
  Radius = 1.5
FEATURE [Part::Cut] Cut201
  Base = -> Box142
  Tool = -> Compound628
FEATURE [Part::Cut] Cut202
  Base = -> Cut201
  Tool = -> Compound634
FEATURE [Part::Cut] Cut203
  Base = -> Cut202
  Tool = -> Compound630
FEATURE [Part::Cylinder] Cylinder1265  label="Válec1265"
  Angle = 360
  AttacherType = Attacher::AttachEngine3D
  Height = 100
  Placement = pos=(14,0,-60) rot=(0,0,1;0rad)
  Radius = 1.5
FEATURE [Part::Compound] Compound648  label="srouby_troj004"
  Links = -> [Cylinder1264,Cylinder1265]
  Placement = pos=(-52,0,0) rot=(0,0,1;0rad)
FEATURE [Part::Cylinder] Cylinder1266  label="Válec1266"
  Angle = 360
  AttacherType = Attacher::AttachEngine3D
  Height = 32
  Placement = pos=(26,41,-42) rot=(0,0,1;0rad)
  Radius = 1.5
FEATURE [Part::Cylinder] Cylinder1267  label="Válec1267"
  Angle = 360
  AttacherType = Attacher::AttachEngine3D
  Height = 32
  Placement = pos=(78,41,-42) rot=(0,0,1;0rad)
  Radius = 1.5
FEATURE [Part::Compound] Compound649
  Links = -> [Cylinder1266,Cylinder1267]
  Placement = pos=(-52,0,36) rot=(0,0,1;0rad)
FEATURE [Part::Compound] Compound647
  Links = -> [Compound648,Compound649]
FEATURE [Part::Cut] Cut204
  Base = -> Cut197
  Tool = -> Compound647
FEATURE [Part::Cylinder] Cylinder  label="Válec"
  Angle = 360
  AttacherType = Attacher::AttachEngine3D
  Height = 52
  Placement = pos=(0,13,-53) rot=(1,0,0;1.5708rad)
  Radius = 60.2
FEATURE [Part::Cut] Cut208
  Base = -> Cut203
  Tool = -> Cylinder
FEATURE [Part::Box] Box240  label="Krychle240"
  AttacherType = Attacher::AttachEngine3D
  Height = 64
  Length = 6
  Placement = pos=(11,-3,-93) rot=(0,0,1;0rad)
  Width = 6
FEATURE [Part::Box] Box241  label="Krychle241"
  AttacherType = Attacher::AttachEngine3D
  Height = 64
  Length = 6
  Placement = pos=(87,-3,-93) rot=(0,0,1;0rad)
  Width = 6
FEATURE [Part::Compound] Compound653
  Links = -> [Box240,Box241]
  Placement = pos=(-52,0,36) rot=(0,0,1;0rad)
FEATURE [Part::Cut] Cut209
  Base = -> Cut208
  Tool = -> Compound653
FEATURE [Part::Compound] Compound654  label="Base-part-A_triangle-support"
  Links = -> [Cut209,Cut190,Cut198,Cut200,Cut204]
  Placement = pos=(0,-53,13) rot=(0,0.707107,-0.707107;3.14159rad)
FEATURE [Part::Cylinder] Cylinder1076  label="Válec1076"
  Angle = 360
  AttacherType = Attacher::AttachEngine3D
  Height = 100
  Placement = pos=(103,-12,-60) rot=(0,0,1;0rad)
  Radius = 1.5
FEATURE [Part::Cylinder] Cylinder1077  label="Válec1077"
  Angle = 360
  AttacherType = Attacher::AttachEngine3D
  Height = 100
  Placement = pos=(103,6,-60) rot=(0,0,1;0rad)
  Radius = 1.5
FEATURE [Part::Cylinder] Cylinder1078  label="Válec1078"
  Angle = 360
  AttacherType = Attacher::AttachEngine3D
  Height = 100
  Placement = pos=(76,18,-60) rot=(0,0,1;0rad)
  Radius = 1.5
FEATURE [Part::Cylinder] Cylinder1079  label="Válec1079"
  Angle = 360
  AttacherType = Attacher::AttachEngine3D
  Height = 100
  Placement = pos=(91,-21,-60) rot=(0,0,1;0rad)
  Radius = 1.5
FEATURE [Part::Cylinder] Cylinder1080  label="Válec1080"
  Angle = 360
  AttacherType = Attacher::AttachEngine3D
  Height = 100
  Placement = pos=(13,-21,-60) rot=(0,0,1;0rad)
  Radius = 1.5
FEATURE [Part::Cylinder] Cylinder1081  label="Válec1081"
  Angle = 360
  AttacherType = Attacher::AttachEngine3D
  Height = 100
  Placement = pos=(28,18,-60) rot=(0,0,1;0rad)
  Radius = 1.5
FEATURE [Part::Cylinder] Cylinder1083  label="Válec1083"
  Angle = 360
  AttacherType = Attacher::AttachEngine3D
  Height = 100
  Placement = pos=(1,-12,-60) rot=(0,0,1;0rad)
  Radius = 1.5
FEATURE [Part::Cylinder] Cylinder1084  label="Válec1084"
  Angle = 360
  AttacherType = Attacher::AttachEngine3D
  Height = 100
  Placement = pos=(1,6,-60) rot=(0,0,1;0rad)
  Radius = 1.5
FEATURE [Part::Cylinder] Cylinder1085  label="Válec1085"
  Angle = 360
  AttacherType = Attacher::AttachEngine3D
  Height = 100
  Placement = pos=(-50,0,-60) rot=(0,0,1;0rad)
  Radius = 1.5
FEATURE [Part::Cylinder] Cylinder1086  label="Válec1086"
  Angle = 360
  AttacherType = Attacher::AttachEngine3D
  Height = 100
  Placement = pos=(-36,34,-60) rot=(0,0,1;0rad)
  Radius = 1.5
FEATURE [Part::Cylinder] Cylinder1087  label="Válec1087"
  Angle = 360
  AttacherType = Attacher::AttachEngine3D
  Height = 100
  Placement = pos=(-36,-34,-60) rot=(0,0,1;0rad)
  Radius = 1.5
FEATURE [Part::Cylinder] Cylinder1088  label="Válec1088"
  Angle = 360
  AttacherType = Attacher::AttachEngine3D
  Height = 100
  Placement = pos=(50,0,-60) rot=(0,0,1;0rad)
  Radius = 1.5
FEATURE [Part::Cylinder] Cylinder1089  label="Válec1089"
  Angle = 360
  AttacherType = Attacher::AttachEngine3D
  Height = 100
  Placement = pos=(36,34,-60) rot=(0,0,1;0rad)
  Radius = 1.5
FEATURE [Part::Cylinder] Cylinder1090  label="Válec1090"
  Angle = 360
  AttacherType = Attacher::AttachEngine3D
  Height = 100
  Placement = pos=(36,-34,-60) rot=(0,0,1;0rad)
  Radius = 1.5
FEATURE [Part::Cylinder] Cylinder1091  label="Válec1091"
  Angle = 360
  AttacherType = Attacher::AttachEngine3D
  Height = 16
  Placement = pos=(0,0,2) rot=(0,0,1;0rad)
  Radius = 59
FEATURE [Part::Cylinder] Cylinder1092  label="Válec1092"
  Angle = 360
  AttacherType = Attacher::AttachEngine3D
  Height = 4
  Placement = pos=(52,0,-26) rot=(0,0,1;0rad)
  Radius = 59
FEATURE [Part::Cylinder] Cylinder1101  label="Válec1101"
  Angle = 360
  AttacherType = Attacher::AttachEngine3D
  Height = 100
  Placement = pos=(103,-12,-60) rot=(0,0,1;0rad)
  Radius = 1.5
FEATURE [Part::Cylinder] Cylinder1102  label="Válec1102"
  Angle = 360
  AttacherType = Attacher::AttachEngine3D
  Height = 100
  Placement = pos=(103,6,-60) rot=(0,0,1;0rad)
  Radius = 1.5
FEATURE [Part::Cylinder] Cylinder1103  label="Válec1103"
  Angle = 360
  AttacherType = Attacher::AttachEngine3D
  Height = 100
  Placement = pos=(76,18,-60) rot=(0,0,1;0rad)
  Radius = 1.5
FEATURE [Part::Cylinder] Cylinder1104  label="Válec1104"
  Angle = 360
  AttacherType = Attacher::AttachEngine3D
  Height = 100
  Placement = pos=(91,-21,-60) rot=(0,0,1;0rad)
  Radius = 1.5
FEATURE [Part::Cylinder] Cylinder1105  label="Válec1105"
  Angle = 360
  AttacherType = Attacher::AttachEngine3D
  Height = 100
  Placement = pos=(13,-21,-60) rot=(0,0,1;0rad)
  Radius = 1.5
FEATURE [Part::Cylinder] Cylinder1106  label="Válec1106"
  Angle = 360
  AttacherType = Attacher::AttachEngine3D
  Height = 100
  Placement = pos=(28,18,-60) rot=(0,0,1;0rad)
  Radius = 1.5
FEATURE [Part::Cylinder] Cylinder1107  label="Válec1107"
  Angle = 360
  AttacherType = Attacher::AttachEngine3D
  Height = 100
  Placement = pos=(1,-12,-60) rot=(0,0,1;0rad)
  Radius = 1.5
FEATURE [Part::Cylinder] Cylinder1108  label="Válec1108"
  Angle = 360
  AttacherType = Attacher::AttachEngine3D
  Height = 100
  Placement = pos=(1,6,-60) rot=(0,0,1;0rad)
  Radius = 1.5
FEATURE [Part::Cylinder] Cylinder1109  label="Válec1109"
  Angle = 360
  AttacherType = Attacher::AttachEngine3D
  Height = 20
  Placement = pos=(103,-12,-20) rot=(0,0,1;0rad)
  Radius = 4
FEATURE [Part::Cylinder] Cylinder1110  label="Válec1110"
  Angle = 360
  AttacherType = Attacher::AttachEngine3D
  Height = 20
  Placement = pos=(103,6,-20) rot=(0,0,1;0rad)
  Radius = 4
FEATURE [Part::Cylinder] Cylinder1111  label="Válec1111"
  Angle = 360
  AttacherType = Attacher::AttachEngine3D
  Height = 20
  Placement = pos=(76,18,-18) rot=(0,0,1;0rad)
  Radius = 4
FEATURE [Part::Cylinder] Cylinder1112  label="Válec1112"
  Angle = 360
  AttacherType = Attacher::AttachEngine3D
  Height = 20
  Placement = pos=(91,-21,-18) rot=(0,0,1;0rad)
  Radius = 4
FEATURE [Part::Cylinder] Cylinder1113  label="Válec1113"
  Angle = 360
  AttacherType = Attacher::AttachEngine3D
  Height = 40
  Placement = pos=(13,-21,-18) rot=(0,0,1;0rad)
  Radius = 4
FEATURE [Part::Cylinder] Cylinder1114  label="Válec1114"
  Angle = 360
  AttacherType = Attacher::AttachEngine3D
  Height = 40
  Placement = pos=(28,18,-18) rot=(0,0,1;0rad)
  Radius = 4
FEATURE [Part::Cylinder] Cylinder1115  label="Válec1115"
  Angle = 360
  AttacherType = Attacher::AttachEngine3D
  Height = 40
  Placement = pos=(1,-12,-18) rot=(0,0,1;0rad)
  Radius = 4
FEATURE [Part::Cylinder] Cylinder1116  label="Válec1116"
  Angle = 360
  AttacherType = Attacher::AttachEngine3D
  Height = 40
  Placement = pos=(1,6,-18) rot=(0,0,1;0rad)
  Radius = 4
FEATURE [Part::Cylinder] Cylinder1117  label="Válec1117"
  Angle = 360
  AttacherType = Attacher::AttachEngine3D
  Height = 20
  Placement = pos=(103,-12,-20) rot=(0,0,1;0rad)
  Radius = 4
FEATURE [Part::Cylinder] Cylinder1118  label="Válec1118"
  Angle = 360
  AttacherType = Attacher::AttachEngine3D
  Height = 20
  Placement = pos=(103,6,-20) rot=(0,0,1;0rad)
  Radius = 4
FEATURE [Part::Cylinder] Cylinder1119  label="Válec1119"
  Angle = 360
  AttacherType = Attacher::AttachEngine3D
  Height = 20
  Placement = pos=(76,18,-18) rot=(0,0,1;0rad)
  Radius = 4
FEATURE [Part::Cylinder] Cylinder1120  label="Válec1120"
  Angle = 360
  AttacherType = Attacher::AttachEngine3D
  Height = 20
  Placement = pos=(91,-21,-18) rot=(0,0,1;0rad)
  Radius = 4
FEATURE [Part::Cylinder] Cylinder1121  label="Válec1121"
  Angle = 360
  AttacherType = Attacher::AttachEngine3D
  Height = 40
  Placement = pos=(13,-21,-18) rot=(0,0,1;0rad)
  Radius = 4
FEATURE [Part::Cylinder] Cylinder1122  label="Válec1122"
  Angle = 360
  AttacherType = Attacher::AttachEngine3D
  Height = 40
  Placement = pos=(28,18,-18) rot=(0,0,1;0rad)
  Radius = 4
FEATURE [Part::Cylinder] Cylinder1123  label="Válec1123"
  Angle = 360
  AttacherType = Attacher::AttachEngine3D
  Height = 40
  Placement = pos=(1,-12,-18) rot=(0,0,1;0rad)
  Radius = 4
FEATURE [Part::Cylinder] Cylinder1124  label="Válec1124"
  Angle = 360
  AttacherType = Attacher::AttachEngine3D
  Height = 40
  Placement = pos=(1,6,-18) rot=(0,0,1;0rad)
  Radius = 4
FEATURE [Part::Cylinder] Cylinder1125  label="Válec1125"
  Angle = 360
  AttacherType = Attacher::AttachEngine3D
  Height = 100
  Placement = pos=(36,34,-90) rot=(0,0,1;0rad)
  Radius = 4
FEATURE [Part::Cylinder] Cylinder1126  label="Válec1126"
  Angle = 360
  AttacherType = Attacher::AttachEngine3D
  Height = 100
  Placement = pos=(-50,0,-90) rot=(0,0,1;0rad)
  Radius = 4
FEATURE [Part::Cylinder] Cylinder1127  label="Válec1127"
  Angle = 360
  AttacherType = Attacher::AttachEngine3D
  Height = 100
  Placement = pos=(-36,34,-90) rot=(0,0,1;0rad)
  Radius = 4
FEATURE [Part::Cylinder] Cylinder1128  label="Válec1128"
  Angle = 360
  AttacherType = Attacher::AttachEngine3D
  Height = 100
  Placement = pos=(-36,-34,-90) rot=(0,0,1;0rad)
  Radius = 4
FEATURE [Part::Cylinder] Cylinder1129  label="Válec1129"
  Angle = 360
  AttacherType = Attacher::AttachEngine3D
  Height = 100
  Placement = pos=(50,0,-90) rot=(0,0,1;0rad)
  Radius = 4
FEATURE [Part::Cylinder] Cylinder1130  label="Válec1130"
  Angle = 360
  AttacherType = Attacher::AttachEngine3D
  Height = 100
  Placement = pos=(36,-34,-90) rot=(0,0,1;0rad)
  Radius = 4
FEATURE [Part::Cylinder] Cylinder1131  label="Válec1131"
  Angle = 360
  AttacherType = Attacher::AttachEngine3D
  Height = 100
  Placement = pos=(36,34,-90) rot=(0,0,1;0rad)
  Radius = 4
FEATURE [Part::Cylinder] Cylinder1132  label="Válec1132"
  Angle = 360
  AttacherType = Attacher::AttachEngine3D
  Height = 100
  Placement = pos=(-50,0,-90) rot=(0,0,1;0rad)
  Radius = 4
FEATURE [Part::Cylinder] Cylinder1133  label="Válec1133"
  Angle = 360
  AttacherType = Attacher::AttachEngine3D
  Height = 100
  Placement = pos=(-36,34,-90) rot=(0,0,1;0rad)
  Radius = 4
FEATURE [Part::Cylinder] Cylinder1134  label="Válec1134"
  Angle = 360
  AttacherType = Attacher::AttachEngine3D
  Height = 100
  Placement = pos=(-36,-34,-90) rot=(0,0,1;0rad)
  Radius = 4
FEATURE [Part::Cylinder] Cylinder1135  label="Válec1135"
  Angle = 360
  AttacherType = Attacher::AttachEngine3D
  Height = 100
  Placement = pos=(50,0,-90) rot=(0,0,1;0rad)
  Radius = 4
FEATURE [Part::Cylinder] Cylinder1136  label="Válec1136"
  Angle = 360
  AttacherType = Attacher::AttachEngine3D
  Height = 100
  Placement = pos=(36,-34,-90) rot=(0,0,1;0rad)
  Radius = 4
FEATURE [Part::Cylinder] Cylinder1137  label="Válec1137"
  Angle = 360
  AttacherType = Attacher::AttachEngine3D
  Height = 100
  Placement = pos=(36,34,-90) rot=(0,0,1;0rad)
  Radius = 4
FEATURE [Part::Cylinder] Cylinder1138  label="Válec1138"
  Angle = 360
  AttacherType = Attacher::AttachEngine3D
  Height = 100
  Placement = pos=(-50,0,-90) rot=(0,0,1;0rad)
  Radius = 4
FEATURE [Part::Cylinder] Cylinder1139  label="Válec1139"
  Angle = 360
  AttacherType = Attacher::AttachEngine3D
  Height = 100
  Placement = pos=(-36,34,-90) rot=(0,0,1;0rad)
  Radius = 4
FEATURE [Part::Cylinder] Cylinder1140  label="Válec1140"
  Angle = 360
  AttacherType = Attacher::AttachEngine3D
  Height = 100
  Placement = pos=(-36,-34,-90) rot=(0,0,1;0rad)
  Radius = 4
FEATURE [Part::Cylinder] Cylinder1141  label="Válec1141"
  Angle = 360
  AttacherType = Attacher::AttachEngine3D
  Height = 100
  Placement = pos=(50,0,-90) rot=(0,0,1;0rad)
  Radius = 4
FEATURE [Part::Cylinder] Cylinder1142  label="Válec1142"
  Angle = 360
  AttacherType = Attacher::AttachEngine3D
  Height = 100
  Placement = pos=(36,-34,-90) rot=(0,0,1;0rad)
  Radius = 4
FEATURE [Part::Cylinder] Cylinder1143  label="Válec1143"
  Angle = 360
  AttacherType = Attacher::AttachEngine3D
  Height = 100
  Placement = pos=(36,34,-60) rot=(0,0,1;0rad)
  Radius = 1.5
FEATURE [Part::Cylinder] Cylinder1144  label="Válec1144"
  Angle = 360
  AttacherType = Attacher::AttachEngine3D
  Height = 100
  Placement = pos=(-50,0,-60) rot=(0,0,1;0rad)
  Radius = 1.5
FEATURE [Part::Cylinder] Cylinder1145  label="Válec1145"
  Angle = 360
  AttacherType = Attacher::AttachEngine3D
  Height = 100
  Placement = pos=(-36,34,-60) rot=(0,0,1;0rad)
  Radius = 1.5
FEATURE [Part::Cylinder] Cylinder1146  label="Válec1146"
  Angle = 360
  AttacherType = Attacher::AttachEngine3D
  Height = 100
  Placement = pos=(-36,-34,-60) rot=(0,0,1;0rad)
  Radius = 1.5
FEATURE [Part::Cylinder] Cylinder1147  label="Válec1147"
  Angle = 360
  AttacherType = Attacher::AttachEngine3D
  Height = 100
  Placement = pos=(50,0,-60) rot=(0,0,1;0rad)
  Radius = 1.5
FEATURE [Part::Cylinder] Cylinder1148  label="Válec1148"
  Angle = 360
  AttacherType = Attacher::AttachEngine3D
  Height = 100
  Placement = pos=(36,-34,-60) rot=(0,0,1;0rad)
  Radius = 1.5
FEATURE [Part::Box] Box214  label="Krychle214"
  AttacherType = Attacher::AttachEngine3D
  Height = 100
  Length = 200
  Placement = pos=(-60,-144,-90) rot=(0,0,1;0rad)
  Width = 100
FEATURE [Part::Box] Box233  label="Krychle233"
  AttacherType = Attacher::AttachEngine3D
  Height = 100
  Length = 200
  Placement = pos=(-60,-144,-90) rot=(0,0,1;0rad)
  Width = 100
FEATURE [Part::Box] Box234  label="Krychle234"
  AttacherType = Attacher::AttachEngine3D
  Height = 100
  Length = 200
  Placement = pos=(-76,44,-90) rot=(0,0,1;0rad)
  Width = 100
FEATURE [Part::Box] Box235  label="Krychle235"
  AttacherType = Attacher::AttachEngine3D
  Height = 100
  Length = 200
  Placement = pos=(-60,44,-90) rot=(0,0,1;0rad)
  Width = 100
FEATURE [Part::Cylinder] Cylinder1228  label="Válec1228"
  Angle = 360
  AttacherType = Attacher::AttachEngine3D
  Height = 100
  Placement = pos=(90,0,-60) rot=(0,0,1;0rad)
  Radius = 1.5
FEATURE [Part::Cylinder] Cylinder1229  label="Válec1229"
  Angle = 360
  AttacherType = Attacher::AttachEngine3D
  Height = 100
  Placement = pos=(14,0,-60) rot=(0,0,1;0rad)
  Radius = 1.5
FEATURE [Part::Cylinder] Cylinder1230  label="Válec1230"
  Angle = 360
  AttacherType = Attacher::AttachEngine3D
  Height = 100
  Placement = pos=(90,0,-18) rot=(0,0,1;0rad)
  Radius = 4
FEATURE [Part::Cylinder] Cylinder1231  label="Válec1231"
  Angle = 360
  AttacherType = Attacher::AttachEngine3D
  Height = 100
  Placement = pos=(14,0,-18) rot=(0,0,1;0rad)
  Radius = 4
FEATURE [Part::Box] Box441  label="Krychle441"
  AttacherType = Attacher::AttachEngine3D
  Height = 2
  Length = 6
  Placement = pos=(75,38,-22) rot=(0,0,1;0rad)
  Width = 6
FEATURE [Part::Box] Box442  label="Krychle442"
  AttacherType = Attacher::AttachEngine3D
  Height = 2
  Length = 6
  Placement = pos=(23,38,-22) rot=(0,0,1;0rad)
  Width = 6
FEATURE [Part::Cylinder] Cylinder1268  label="Válec1268"
  Angle = 360
  AttacherType = Attacher::AttachEngine3D
  Height = 32
  Placement = pos=(26,41,-42) rot=(0,0,1;0rad)
  Radius = 1.5
FEATURE [Part::Cylinder] Cylinder1269  label="Válec1269"
  Angle = 360
  AttacherType = Attacher::AttachEngine3D
  Height = 32
  Placement = pos=(78,41,-42) rot=(0,0,1;0rad)
  Radius = 1.5
FEATURE [Part::Cylinder] Cylinder1234  label="Válec1234"
  Angle = 360
  AttacherType = Attacher::AttachEngine3D
  Height = 32
  Placement = pos=(26,41,-46) rot=(0,0,1;0rad)
  Radius = 1.5
FEATURE [Part::Cylinder] Cylinder1235  label="Válec1235"
  Angle = 360
  AttacherType = Attacher::AttachEngine3D
  Height = 32
  Placement = pos=(78,41,-46) rot=(0,0,1;0rad)
  Radius = 1.5
FEATURE [Part::Cylinder] Cylinder1236  label="Válec1236"
  Angle = 360
  AttacherType = Attacher::AttachEngine3D
  Height = 100
  Placement = pos=(90,0,-18) rot=(0,0,1;0rad)
  Radius = 4
FEATURE [Part::Cylinder] Cylinder1237  label="Válec1237"
  Angle = 360
  AttacherType = Attacher::AttachEngine3D
  Height = 100
  Placement = pos=(14,0,-18) rot=(0,0,1;0rad)
  Radius = 4
FEATURE [Part::Cylinder] Cylinder1270  label="Válec1270"
  Angle = 360
  AttacherType = Attacher::AttachEngine3D
  Height = 100
  Placement = pos=(90,0,-60) rot=(0,0,1;0rad)
  Radius = 1.5
FEATURE [Part::Cylinder] Cylinder1271  label="Válec1271"
  Angle = 360
  AttacherType = Attacher::AttachEngine3D
  Height = 100
  Placement = pos=(14,0,-60) rot=(0,0,1;0rad)
  Radius = 1.5
FEATURE [Sketcher::SketchObject] Sketch003
  FullyConstrained = false
  sketch-geometry (1):
    g0: Circle CenterX=-186.411 CenterY=73.9277 CenterZ=0 NormalX=0 NormalY=0 NormalZ=1 AngleXU=0 Radius=59
FEATURE [Part::Extrusion] Extrude001
  Base = -> Sketch003
  Dir = (52,0,32)
  DirMode = 0
  FaceMakerClass = Part::FaceMakerBullseye
  LengthFwd = 61
  LengthRev = 0
  Placement = pos=(-134,74,-22) rot=(0,0,1;3.14159rad)
  Solid = true
  Symmetric = false
FEATURE [Part::Compound] Compound559  label="srouby_monoblok"
  Links = -> [Cylinder1076,Cylinder1077,Cylinder1078,Cylinder1079,Cylinder1080,Cylinder1081,Cylinder1083,Cylinder1084]
FEATURE [Part::Compound] Compound560  label="sbouby_baze"
  Links = -> [Cylinder1085,Cylinder1086,Cylinder1087,Cylinder1088,Cylinder1089,Cylinder1090]
FEATURE [Part::Compound] Compound562  label="srouby_monoblok001"
  Links = -> [Cylinder1101,Cylinder1102,Cylinder1103,Cylinder1104,Cylinder1105,Cylinder1106,Cylinder1107,Cylinder1108]
FEATURE [Part::Compound] Compound563  label="srouby_monoblok_silne001"
  Links = -> [Cylinder1109,Cylinder1110,Cylinder1111,Cylinder1112,Cylinder1113,Cylinder1114,Cylinder1115,Cylinder1116]
FEATURE [Part::Compound] Compound564  label="srouby_monoblok_silne002"
  Links = -> [Cylinder1117,Cylinder1118,Cylinder1119,Cylinder1120,Cylinder1121,Cylinder1122,Cylinder1123,Cylinder1124]
FEATURE [Part::Compound] Compound565  label="sbouby_baze_silne"
  Links = -> [Cylinder1126,Cylinder1127,Cylinder1128,Cylinder1129,Cylinder1125,Cylinder1130]
FEATURE [Part::Compound] Compound566  label="sbouby_baze_silne001"
  Links = -> [Cylinder1132,Cylinder1133,Cylinder1134,Cylinder1135,Cylinder1131,Cylinder1136]
FEATURE [Part::Cut] Cut247
  Base = -> Extrude001
  Tool = -> Compound559
FEATURE [Part::Cut] Cut248
  Base = -> Cut247
  Tool = -> Compound563
FEATURE [Part::Cut] Cut249
  Base = -> Cylinder1091
  Tool = -> Compound564
FEATURE [Part::Cut] Cut250
  Base = -> Cylinder1092
  Tool = -> Compound562
FEATURE [Part::Cut] Cut251
  Base = -> Cut250
  Tool = -> Compound565
FEATURE [Part::Cut] Cut253
  Base = -> Cut249
  Tool = -> Compound566
FEATURE [Part::Cut] Cut255
  Base = -> Cut253
  Tool = -> Compound560
FEATURE [Part::Cut] Cut285
  Base = -> Cut251
  Tool = -> Box233
FEATURE [Part::Cut] Cut287
  Base = -> Cut285
  Tool = -> Box235
FEATURE [Part::Compound] Compound567  label="sbouby_baze_silne002"
  Links = -> [Cylinder1138,Cylinder1139,Cylinder1140,Cylinder1141,Cylinder1137,Cylinder1142]
FEATURE [Part::Cut] Cut252
  Base = -> Cut248
  Tool = -> Compound567
FEATURE [Part::Compound] Compound568  label="sbouby_baze001"
  Links = -> [Cylinder1144,Cylinder1145,Cylinder1146,Cylinder1147,Cylinder1143,Cylinder1148]
FEATURE [Part::Cut] Cut254
  Base = -> Cut252
  Tool = -> Compound568
FEATURE [Part::Cut] Cut256
  Base = -> Cut254
  Tool = -> Box214
FEATURE [Part::Cut] Cut286
  Base = -> Cut256
  Tool = -> Box234
FEATURE [Part::Chamfer] Chamfer036
  Base = -> Cut255
  Edges = 1 edges r=4: [Edge3]
FEATURE [Part::Compound] Compound619
  Links = -> [Box441,Box442]
FEATURE [Part::Cut] Cut289
  Base = -> Cut286
  Tool = -> Compound619
FEATURE [Part::Compound] Compound833
  Links = -> [Cylinder1268,Cylinder1269]
FEATURE [Part::Cut] Cut288
  Base = -> Cut287
  Tool = -> Compound833
FEATURE [Part::Compound] Compound621
  Links = -> [Cylinder1234,Cylinder1235]
FEATURE [Part::Cut] Cut290
  Base = -> Cut289
  Tool = -> Compound621
FEATURE [Part::Compound] Compound622  label="srouby_troj_silne"
  Links = -> [Cylinder1230,Cylinder1231]
FEATURE [Part::Compound] Compound623  label="srouby_troj"
  Links = -> [Cylinder1228,Cylinder1229]
FEATURE [Part::Compound] Compound624  label="srouby_troj_silne001"
  Links = -> [Cylinder1236,Cylinder1237]
FEATURE [Part::Compound] Compound834  label="srouby_troj005"
  Links = -> [Cylinder1270,Cylinder1271]
FEATURE [Part::Cut] Cut291
  Base = -> Cut288
  Tool = -> Compound834
FEATURE [Part::Cut] Cut292
  Base = -> Cut290
  Tool = -> Compound623
FEATURE [Part::Cut] Cut293
  Base = -> Cut292
  Tool = -> Compound622
FEATURE [Part::Cut] Cut294
  Base = -> Chamfer036
  Placement = pos=(0,0,4) rot=(0,0,1;0rad)
  Tool = -> Compound624
FEATURE [Part::Box] Box443  label="Krychle443"
  AttacherType = Attacher::AttachEngine3D
  Height = 13
  Length = 10
  Placement = pos=(-60,-43,10) rot=(0,0,1;0rad)
  Width = 43
FEATURE [Part::Box] Box444  label="Krychle444"
  AttacherType = Attacher::AttachEngine3D
  Height = 13
  Length = 10
  Placement = pos=(50,-43,10) rot=(0,0,1;0rad)
  Width = 43
FEATURE [Part::Cylinder] Cylinder1272  label="Válec1272"
  Angle = 360
  AttacherType = Attacher::AttachEngine3D
  Height = 33
  Placement = pos=(60,-43,10) rot=(0,0,1;0rad)
  Radius = 6
FEATURE [Part::Box] Box445  label="Krychle445"
  AttacherType = Attacher::AttachEngine3D
  Height = 2
  Length = 6
  Placement = pos=(45.9619,41.7193,23) rot=(0,0,1;2.35619rad)
  Width = 10
FEATURE [Part::Box] Box446  label="Krychle446"
  AttacherType = Attacher::AttachEngine3D
  Height = 2
  Length = 6
  Placement = pos=(62,-3,23) rot=(0,0,1;1.5708rad)
  Width = 10
FEATURE [Part::Box] Box447  label="Krychle447"
  AttacherType = Attacher::AttachEngine3D
  Height = 2
  Length = 6
  Placement = pos=(41.7193,-45.9619,23) rot=(0,0,1;0.785398rad)
  Width = 10
FEATURE [Part::Box] Box448  label="Krychle448"
  AttacherType = Attacher::AttachEngine3D
  Height = 2
  Length = 6
  Placement = pos=(-3,-62,23) rot=(0,0,1;0rad)
  Width = 10
FEATURE [Part::Box] Box449  label="Krychle449"
  AttacherType = Attacher::AttachEngine3D
  Height = 2
  Length = 6
  Placement = pos=(-45.9619,-41.7193,23) rot=(0,0,-1;0.785398rad)
  Width = 10
FEATURE [Part::Box] Box450  label="Krychle450"
  AttacherType = Attacher::AttachEngine3D
  Height = 2
  Length = 6
  Placement = pos=(-62,3,23) rot=(0,0,-1;1.5708rad)
  Width = 10
FEATURE [Part::Cylinder] Cylinder1273  label="Válec1273"
  Angle = 360
  AttacherType = Attacher::AttachEngine3D
  Height = 50
  Placement = pos=(39.598,39.598,2) rot=(0,0,1;2.35619rad)
  Radius = 1.5
FEATURE [Part::Cylinder] Cylinder1274  label="Válec1274"
  Angle = 360
  AttacherType = Attacher::AttachEngine3D
  Height = 33
  Placement = pos=(-60,-43,10) rot=(0,0,1;0rad)
  Radius = 6
FEATURE [Part::Cylinder] Cylinder1275  label="Válec1275"
  Angle = 360
  AttacherType = Attacher::AttachEngine3D
  Height = 50
  Placement = pos=(-39.598,39.598,2) rot=(0,0,1;3.92699rad)
  Radius = 1.5
FEATURE [Part::Cylinder] Cylinder1276  label="Válec1276"
  Angle = 360
  AttacherType = Attacher::AttachEngine3D
  Height = 50
  Placement = pos=(56,0,2) rot=(0,0,1;1.5708rad)
  Radius = 1.5
FEATURE [Part::Cylinder] Cylinder1277  label="Válec1277"
  Angle = 360
  AttacherType = Attacher::AttachEngine3D
  Height = 50
  Placement = pos=(-1.2e-14,56,2) rot=(0,0,1;3.14159rad)
  Radius = 1.5
FEATURE [Part::Cylinder] Cylinder1278  label="Válec1278"
  Angle = 360
  AttacherType = Attacher::AttachEngine3D
  Height = 50
  Placement = pos=(-56,-1.3e-14,2) rot=(0,0,-1;1.5708rad)
  Radius = 1.5
FEATURE [Part::Cylinder] Cylinder1279  label="Válec1279"
  Angle = 360
  AttacherType = Attacher::AttachEngine3D
  Height = 50
  Placement = pos=(0,-56,2) rot=(0,0,1;0rad)
  Radius = 1.5
FEATURE [Part::Cylinder] Cylinder1280  label="Válec1280"
  Angle = 360
  AttacherType = Attacher::AttachEngine3D
  Height = 50
  Placement = pos=(39.598,-39.598,2) rot=(0,0,1;0.785398rad)
  Radius = 1.5
FEATURE [Part::Cylinder] Cylinder1281  label="Válec1281"
  Angle = 360
  AttacherType = Attacher::AttachEngine3D
  Height = 50
  Placement = pos=(-39.598,-39.598,2) rot=(0,0,-1;0.785398rad)
  Radius = 1.5
FEATURE [Part::Cylinder] Cylinder1282  label="Válec1282"
  Angle = 360
  AttacherType = Attacher::AttachEngine3D
  Height = 33
  Placement = pos=(0,0,20) rot=(0,0,1;0rad)
  Radius = 60
FEATURE [Part::Cylinder] Cylinder1283  label="Válec1283"
  Angle = 360
  AttacherType = Attacher::AttachEngine3D
  Height = 22
  Placement = pos=(-51,-40,25) rot=(1,0,0;1.5708rad)
  Radius = 1.5
FEATURE [Part::Cylinder] Cylinder1284  label="Válec1284"
  Angle = 360
  AttacherType = Attacher::AttachEngine3D
  Height = 20
  Placement = pos=(51,-40,25) rot=(1,0,0;1.5708rad)
  Radius = 1.5
FEATURE [Part::Box] Box451  label="Krychle451"
  AttacherType = Attacher::AttachEngine3D
  Height = 2
  Length = 6
  Placement = pos=(3,62,23) rot=(0,0,1;3.14159rad)
  Width = 10
FEATURE [Part::Box] Box452  label="Krychle452"
  AttacherType = Attacher::AttachEngine3D
  Height = 2
  Length = 6
  Placement = pos=(-41.7193,45.9619,23) rot=(0,0,1;3.92699rad)
  Width = 10
FEATURE [Part::Box] Box453  label="Krychle453"
  AttacherType = Attacher::AttachEngine3D
  Height = 6
  Length = 6
  Placement = pos=(36,-45,31) rot=(0,0,1;0rad)
  Width = 2
FEATURE [Part::FeaturePython] Tube089  # WARN: FeaturePython — macro-defined, semantics opaque (R4)
  AttacherType = Attacher::AttachEngine3D
  Height = 33
  InnerRadius = 53
  OuterRadius = 60
  Placement = pos=(0,0,20) rot=(0,0,1;0rad)
FEATURE [Part::Box] Box454  label="Krychle454"
  AttacherType = Attacher::AttachEngine3D
  Height = 6
  Length = 6
  Placement = pos=(-42,-45,31) rot=(0,0,1;0rad)
  Width = 2
FEATURE [Part::Cylinder] Cylinder213  label="Válec213"
  Angle = 360
  AttacherType = Attacher::AttachEngine3D
  Height = 20
  Placement = pos=(-39,-40,34) rot=(1,0,0;1.5708rad)
  Radius = 1.5
FEATURE [Part::Cylinder] Cylinder211  label="Válec211"
  Angle = 360
  AttacherType = Attacher::AttachEngine3D
  Height = 20
  Placement = pos=(-39,-40,34) rot=(1,0,0;1.5708rad)
  Radius = 1.5
FEATURE [Part::Box] Box093  label="Krychle093"
  AttacherType = Attacher::AttachEngine3D
  Height = 6
  Length = 6
  Placement = pos=(-42,-45,31) rot=(0,0,1;0rad)
  Width = 2
FEATURE [Part::Cylinder] Cylinder214  label="Válec214"
  Angle = 360
  AttacherType = Attacher::AttachEngine3D
  Height = 20
  Placement = pos=(39,-40,34) rot=(1,0,0;1.5708rad)
  Radius = 1.5
FEATURE [Part::Compound] Compound196
  Links = -> [Cylinder213,Cylinder214]
  Placement = pos=(0,0,-11) rot=(0,0,1;0rad)
FEATURE [Part::Box] Box092  label="Krychle092"
  AttacherType = Attacher::AttachEngine3D
  Height = 6
  Length = 6
  Placement = pos=(36,-45,31) rot=(0,0,1;0rad)
  Width = 2
FEATURE [Part::Compound] Compound197
  Links = -> [Box092,Box093]
  Placement = pos=(0,-2,-11) rot=(0,0,1;0rad)
FEATURE [Part::Cylinder] Cylinder212  label="Válec212"
  Angle = 360
  AttacherType = Attacher::AttachEngine3D
  Height = 20
  Placement = pos=(39,-40,34) rot=(1,0,0;1.5708rad)
  Radius = 1.5
FEATURE [Part::Compound] Compound836
  Links = -> [Cylinder211,Cylinder212]
  Placement = pos=(0,0,-11) rot=(0,0,1;0rad)
FEATURE [Part::Torus] Torus003  label="Anuloid003"
  Angle1 = -180
  Angle2 = 180
  Angle3 = 360
  AttacherType = Attacher::AttachEngine3D
  Placement = pos=(0,0,45) rot=(0,0,1;0rad)
  Radius1 = 51.9
  Radius2 = 3.1
FEATURE [Part::Cut] Cut450
  Base = -> Tube089
  Tool = -> Torus003
FEATURE [Part::Compound] Compound838
  Links = -> [Cylinder1283,Cylinder1284]
  Placement = pos=(0,2,0) rot=(0,0,1;0rad)
FEATURE [Part::Compound] Compound840
  Links = -> [Box453,Box454]
  Placement = pos=(0,-2,-11) rot=(0,0,1;0rad)
FEATURE [Part::Compound] Compound841
  Links = -> [Cylinder1279,Cylinder1280,Cylinder1276,Cylinder1273,Cylinder1277,Cylinder1275,Cylinder1278,Cylinder1281]
FEATURE [Part::Compound] Compound842
  Links = -> [Box451,Box452,Box450,Box449,Box448,Box447,Box446,Box445]
  Placement = pos=(0,0,5) rot=(0,0,1;0rad)
FEATURE [Part::Compound] Compound843
  Links = -> [Cylinder1272,Cylinder1274]
FEATURE [Part::Compound] Compound844
  Links = -> [Box443,Box444]
FEATURE [Part::Cut] Cut441
  Base = -> Compound844
  Tool = -> Compound841
FEATURE [Part::Cut] Cut442
  Base = -> Cut441
  Placement = pos=(0,0,10) rot=(0,0,1;0rad)
  Tool = -> Compound843
FEATURE [Part::Cut] Cut451
  Base = -> Cut442
  Tool = -> Cylinder1282
FEATURE [Part::Cut] Cut452
  Base = -> Cut451
  Tool = -> Compound842
FEATURE [Part::Cut] Cut453
  Base = -> Cut452
  Placement = pos=(0,0,12) rot=(0,0,1;0rad)
  Tool = -> Compound838
FEATURE [Part::Cylinder] Cylinder1285  label="Válec1285"
  Angle = 360
  AttacherType = Attacher::AttachEngine3D
  Height = 10
  Placement = pos=(-47,0,30) rot=(0,0,1;0rad)
  Radius = 3.5
FEATURE [Part::Cut] Cut449
  Base = -> Cut450
  Tool = -> Cylinder1285
FEATURE [Part::Cylinder] Cylinder1286  label="Válec1286"
  Angle = 360
  AttacherType = Attacher::AttachEngine3D
  Height = 20
  Placement = pos=(39.598,-39.598,2) rot=(0,0,1;0.785398rad)
  Radius = 1.5
FEATURE [Part::Cylinder] Cylinder1287  label="Válec1287"
  Angle = 360
  AttacherType = Attacher::AttachEngine3D
  Height = 50
  Placement = pos=(-52,0,45) rot=(0,0,1;0rad)
  Radius = 3.5
FEATURE [Part::Cut] Cut444  label="J-max_lozo-harmo005"
  Base = -> Cut449
  Tool = -> Cylinder1287
FEATURE [Part::Cylinder] Cylinder1288  label="Válec1288"
  Angle = 360
  AttacherType = Attacher::AttachEngine3D
  Height = 20
  Placement = pos=(0,-56,2) rot=(0,0,1;0rad)
  Radius = 1.5
FEATURE [Part::Cylinder] Cylinder1289  label="Válec1289"
  Angle = 360
  AttacherType = Attacher::AttachEngine3D
  Height = 20
  Placement = pos=(56,0,2) rot=(0,0,1;1.5708rad)
  Radius = 1.5
FEATURE [Part::Cylinder] Cylinder1290  label="Válec1290"
  Angle = 360
  AttacherType = Attacher::AttachEngine3D
  Height = 20
  Placement = pos=(39.598,39.598,2) rot=(0,0,1;2.35619rad)
  Radius = 1.5
FEATURE [Part::Cylinder] Cylinder1291  label="Válec1291"
  Angle = 360
  AttacherType = Attacher::AttachEngine3D
  Height = 20
  Placement = pos=(-1.2e-14,56,2) rot=(0,0,1;3.14159rad)
  Radius = 1.5
FEATURE [Part::Cylinder] Cylinder1292  label="Válec1292"
  Angle = 360
  AttacherType = Attacher::AttachEngine3D
  Height = 20
  Placement = pos=(-39.598,39.598,2) rot=(0,0,1;3.92699rad)
  Radius = 1.5
FEATURE [Part::Cylinder] Cylinder1293  label="Válec1293"
  Angle = 360
  AttacherType = Attacher::AttachEngine3D
  Height = 20
  Placement = pos=(-56,-1.3e-14,2) rot=(0,0,-1;1.5708rad)
  Radius = 1.5
FEATURE [Part::Cylinder] Cylinder1294  label="Válec1294"
  Angle = 360
  AttacherType = Attacher::AttachEngine3D
  Height = 20
  Placement = pos=(-39.598,-39.598,2) rot=(0,0,-1;0.785398rad)
  Radius = 1.5
FEATURE [Part::Compound] Compound837
  Links = -> [Cylinder1288,Cylinder1286,Cylinder1289,Cylinder1290,Cylinder1291,Cylinder1292,Cylinder1293,Cylinder1294]
  Placement = pos=(0,0,16) rot=(0,0,1;0rad)
FEATURE [Part::Cut] Cut445
  Base = -> Cut444
  Tool = -> Compound837
FEATURE [Part::Box] Box455  label="Krychle455"
  AttacherType = Attacher::AttachEngine3D
  Height = 2
  Length = 6
  Placement = pos=(-3,-60,23) rot=(0,0,1;0rad)
  Width = 8
FEATURE [Part::Box] Box456  label="Krychle456"
  AttacherType = Attacher::AttachEngine3D
  Height = 2
  Length = 6
  Placement = pos=(40.3051,-44.5477,23) rot=(0,0,1;0.785398rad)
  Width = 8
FEATURE [Part::Box] Box457  label="Krychle457"
  AttacherType = Attacher::AttachEngine3D
  Height = 2
  Length = 6
  Placement = pos=(60,-3,23) rot=(0,0,1;1.5708rad)
  Width = 8
FEATURE [Part::Box] Box458  label="Krychle458"
  AttacherType = Attacher::AttachEngine3D
  Height = 2
  Length = 6
  Placement = pos=(44.5477,40.3051,23) rot=(0,0,1;2.35619rad)
  Width = 8
FEATURE [Part::Box] Box459  label="Krychle459"
  AttacherType = Attacher::AttachEngine3D
  Height = 2
  Length = 6
  Placement = pos=(3,60,23) rot=(0,0,1;3.14159rad)
  Width = 8
FEATURE [Part::Box] Box460  label="Krychle460"
  AttacherType = Attacher::AttachEngine3D
  Height = 2
  Length = 6
  Placement = pos=(-40.3051,44.5477,23) rot=(0,0,1;3.92699rad)
  Width = 8
FEATURE [Part::Box] Box461  label="Krychle461"
  AttacherType = Attacher::AttachEngine3D
  Height = 2
  Length = 6
  Placement = pos=(-60,3,23) rot=(0,0,-1;1.5708rad)
  Width = 8
FEATURE [Part::Box] Box462  label="Krychle462"
  AttacherType = Attacher::AttachEngine3D
  Height = 2
  Length = 6
  Placement = pos=(-44.5477,-40.3051,23) rot=(0,0,-1;0.785398rad)
  Width = 8
FEATURE [Part::Compound] Compound839
  Links = -> [Box455,Box456,Box457,Box458,Box459,Box460,Box461,Box462]
  Placement = pos=(0,0,5) rot=(0,0,1;0rad)
FEATURE [Part::Cut] Cut
  Base = -> Cut445
  Tool = -> Compound839
FEATURE [Part::Cut] Cut448
  Base = -> Cut
  Tool = -> Compound197
FEATURE [Part::Cut] Cut446
  Base = -> Cut448
  Placement = pos=(0,0,12) rot=(0,0,1;0rad)
  Tool = -> Compound196
FEATURE [Part::Cylinder] Cylinder1295  label="Válec1295"
  Angle = 360
  AttacherType = Attacher::AttachEngine3D
  Height = 33
  Placement = pos=(0,0,20) rot=(0,0,1;0rad)
  Radius = 60
FEATURE [Part::Box] Box463  label="Krychle463"
  AttacherType = Attacher::AttachEngine3D
  Height = 33
  Length = 108
  Placement = pos=(-54,-53,20) rot=(0,0,1;0rad)
  Width = 46
FEATURE [Part::Cut] Cut447
  Base = -> Box463
  Tool = -> Cylinder1295
FEATURE [Part::Cut] Cut454
  Base = -> Cut447
  Tool = -> Compound836
FEATURE [Part::Cut] Cut443
  Base = -> Cut454
  Placement = pos=(0,0,12) rot=(0,0,1;0rad)
  Tool = -> Compound840
FEATURE [Part::Compound] Compound845
  Links = -> [Cut291,Cut293,Cut294]
  Placement = pos=(52,-79,13) rot=(0,0.707107,-0.707107;3.14159rad)
FEATURE [Part::Cylinder] Cylinder987  label="Válec987"
  Angle = 360
  AttacherType = Attacher::AttachEngine3D
  Height = 50
  Placement = pos=(0,0,-10) rot=(0,0,1;0rad)
  Radius = 2.65
FEATURE [Part::Cylinder] Cylinder986  label="Válec986"
  Angle = 360
  AttacherType = Attacher::AttachEngine3D
  Height = 100
  Placement = pos=(0,0,-10) rot=(0,0,1;0rad)
  Radius = 2.65
FEATURE [Part::Cylinder] Cylinder988  label="Válec988"
  Angle = 360
  AttacherType = Attacher::AttachEngine3D
  Height = 100
  Placement = pos=(0,0,-10) rot=(0,0,1;0rad)
  Radius = 2.65
FEATURE [Part::Cylinder] Cylinder989  label="Válec989"
  Angle = 360
  AttacherType = Attacher::AttachEngine3D
  Height = 100
  Placement = pos=(0,0,-10) rot=(0,0,1;0rad)
  Radius = 2.65
FEATURE [Part::FeaturePython] wormgear048  # WARN: FeaturePython — macro-defined, semantics opaque (R4)
  AttacherType = Attacher::AttachEngine3D
  Placement = pos=(0,0,32) rot=(0,0,1;0.261799rad)
  beta = 41.1859
  clearance = 0.25
  diameter = 24
  head = 0
  height = 17
  module = 1.5
  pressure_angle = 20
  reverse_pitch = false
  teeth = 14
  version = 0.0.3
FEATURE [Part::FeaturePython] wormgear049  # WARN: FeaturePython — macro-defined, semantics opaque (R4)
  AttacherType = Attacher::AttachEngine3D
  Placement = pos=(0,0,16) rot=(0,0,1;0.490438rad)
  beta = 40.6013
  clearance = 0.2
  diameter = 28
  head = 0
  height = 16
  module = 1.5
  pressure_angle = 25
  reverse_pitch = true
  teeth = 16
  version = 0.0.3
FEATURE [Part::FeaturePython] wormgear051  # WARN: FeaturePython — macro-defined, semantics opaque (R4)
  AttacherType = Attacher::AttachEngine3D
  Placement = pos=(0,0,0) rot=(0,0,1;0.336849rad)
  beta = 40.6013
  clearance = 0.2
  diameter = 28
  head = 0
  height = 16
  module = 1.5
  pressure_angle = 25
  reverse_pitch = false
  teeth = 16
  version = 0.0.3
FEATURE [Part::Cut] Cut417
  Base = -> wormgear051
  Tool = -> Cylinder988
FEATURE [Part::FeaturePython] wormgear050  # WARN: FeaturePython — macro-defined, semantics opaque (R4)
  AttacherType = Attacher::AttachEngine3D
  Placement = pos=(0,0,49) rot=(0,0,1;0.534943rad)
  beta = 41.1859
  clearance = 0.25
  diameter = 24
  head = 0
  height = 16
  module = 1.5
  pressure_angle = 20
  reverse_pitch = true
  teeth = 14
  version = 0.0.3
FEATURE [Part::Cut] Cut416
  Base = -> wormgear050
  Tool = -> Cylinder989
FEATURE [Part::Cut] Cut414
  Base = -> wormgear049
  Tool = -> Cylinder986
FEATURE [Part::Cut] Cut415
  Base = -> wormgear048
  Tool = -> Cylinder987
FEATURE [Part::Compound] Compound812  label="J-max-super-deep_outer-planeo"
  Links = -> [Cut417,Cut416,Cut414,Cut415]
  Placement = pos=(0,-25,0) rot=(0,0,1;0rad)
FEATURE [Part::Cylinder] Cylinder1296  label="Válec1296"
  Angle = 360
  AttacherType = Attacher::AttachEngine3D
  Height = 40
  Placement = pos=(0,-17,21) rot=(1,0,0;1.5708rad)
  Radius = 59
FEATURE [Part::Common] Common
  Base = -> Cut443
  Tool = -> Cylinder1296
FEATURE [Part::Common] Common001
  Base = -> Cut443
  Tool = -> Cylinder1296
FEATURE [Part::Fillet] Fillet018
  Base = -> Cut453
  Edges = 2 edges r=8: [Edge8,Edge61]
FEATURE [Part::Compound] Compound846
  Links = -> [Common,Fillet018,Cut446]
FEATURE [Part::Torus] Torus004  label="Anuloid004"
  Angle1 = -180
  Angle2 = 180
  Angle3 = 360
  AttacherType = Attacher::AttachEngine3D
  Placement = pos=(0,0,34) rot=(0,0,1;0rad)
  Radius1 = 51.9
  Radius2 = 3.1
FEATURE [Part::Box] Box464  label="Krychle464"
  AttacherType = Attacher::AttachEngine3D
  Height = 19
  Length = 10
  Placement = pos=(-60,-43,10) rot=(0,0,1;0rad)
  Width = 43
FEATURE [Part::Box] Box465  label="Krychle465"
  AttacherType = Attacher::AttachEngine3D
  Height = 19
  Length = 10
  Placement = pos=(50,-43,10) rot=(0,0,1;0rad)
  Width = 43
FEATURE [Part::Cylinder] Cylinder1297  label="Válec1297"
  Angle = 360
  AttacherType = Attacher::AttachEngine3D
  Height = 33
  Placement = pos=(60,-43,10) rot=(0,0,1;0rad)
  Radius = 6
FEATURE [Part::Box] Box466  label="Krychle466"
  AttacherType = Attacher::AttachEngine3D
  Height = 2
  Length = 6
  Placement = pos=(45.9619,41.7193,23) rot=(0,0,1;2.35619rad)
  Width = 10
FEATURE [Part::Box] Box467  label="Krychle467"
  AttacherType = Attacher::AttachEngine3D
  Height = 2
  Length = 6
  Placement = pos=(62,-3,23) rot=(0,0,1;1.5708rad)
  Width = 10
FEATURE [Part::Box] Box468  label="Krychle468"
  AttacherType = Attacher::AttachEngine3D
  Height = 2
  Length = 6
  Placement = pos=(41.7193,-45.9619,23) rot=(0,0,1;0.785398rad)
  Width = 10
FEATURE [Part::Box] Box469  label="Krychle469"
  AttacherType = Attacher::AttachEngine3D
  Height = 2
  Length = 6
  Placement = pos=(-3,-62,23) rot=(0,0,1;0rad)
  Width = 10
FEATURE [Part::Box] Box470  label="Krychle470"
  AttacherType = Attacher::AttachEngine3D
  Height = 2
  Length = 6
  Placement = pos=(-45.9619,-41.7193,23) rot=(0,0,-1;0.785398rad)
  Width = 10
FEATURE [Part::Box] Box471  label="Krychle471"
  AttacherType = Attacher::AttachEngine3D
  Height = 2
  Length = 6
  Placement = pos=(-62,3,23) rot=(0,0,-1;1.5708rad)
  Width = 10
FEATURE [Part::Cylinder] Cylinder1298  label="Válec1298"
  Angle = 360
  AttacherType = Attacher::AttachEngine3D
  Height = 50
  Placement = pos=(39.598,39.598,2) rot=(0,0,1;2.35619rad)
  Radius = 1.5
FEATURE [Part::Cylinder] Cylinder1299  label="Válec1299"
  Angle = 360
  AttacherType = Attacher::AttachEngine3D
  Height = 33
  Placement = pos=(-60,-43,10) rot=(0,0,1;0rad)
  Radius = 6
FEATURE [Part::Cylinder] Cylinder1300  label="Válec1300"
  Angle = 360
  AttacherType = Attacher::AttachEngine3D
  Height = 50
  Placement = pos=(-39.598,39.598,2) rot=(0,0,1;3.92699rad)
  Radius = 1.5
FEATURE [Part::Cylinder] Cylinder1301  label="Válec1301"
  Angle = 360
  AttacherType = Attacher::AttachEngine3D
  Height = 50
  Placement = pos=(56,0,2) rot=(0,0,1;1.5708rad)
  Radius = 1.5
FEATURE [Part::Cylinder] Cylinder1302  label="Válec1302"
  Angle = 360
  AttacherType = Attacher::AttachEngine3D
  Height = 50
  Placement = pos=(-1.2e-14,56,2) rot=(0,0,1;3.14159rad)
  Radius = 1.5
FEATURE [Part::Cylinder] Cylinder1303  label="Válec1303"
  Angle = 360
  AttacherType = Attacher::AttachEngine3D
  Height = 50
  Placement = pos=(-56,-1.3e-14,2) rot=(0,0,-1;1.5708rad)
  Radius = 1.5
FEATURE [Part::Cylinder] Cylinder1304  label="Válec1304"
  Angle = 360
  AttacherType = Attacher::AttachEngine3D
  Height = 50
  Placement = pos=(0,-56,2) rot=(0,0,1;0rad)
  Radius = 1.5
FEATURE [Part::Cylinder] Cylinder1305  label="Válec1305"
  Angle = 360
  AttacherType = Attacher::AttachEngine3D
  Height = 50
  Placement = pos=(39.598,-39.598,2) rot=(0,0,1;0.785398rad)
  Radius = 1.5
FEATURE [Part::Cylinder] Cylinder1306  label="Válec1306"
  Angle = 360
  AttacherType = Attacher::AttachEngine3D
  Height = 50
  Placement = pos=(-39.598,-39.598,2) rot=(0,0,-1;0.785398rad)
  Radius = 1.5
FEATURE [Part::Cylinder] Cylinder1307  label="Válec1307"
  Angle = 360
  AttacherType = Attacher::AttachEngine3D
  Height = 33
  Placement = pos=(0,0,20) rot=(0,0,1;0rad)
  Radius = 60
FEATURE [Part::Cylinder] Cylinder1308  label="Válec1308"
  Angle = 360
  AttacherType = Attacher::AttachEngine3D
  Height = 40
  Placement = pos=(-51,-40,25) rot=(1,0,0;1.5708rad)
  Radius = 1.5
FEATURE [Part::Cylinder] Cylinder1309  label="Válec1309"
  Angle = 360
  AttacherType = Attacher::AttachEngine3D
  Height = 40
  Placement = pos=(51,-40,25) rot=(1,0,0;1.5708rad)
  Radius = 1.5
FEATURE [Part::Box] Box472  label="Krychle472"
  AttacherType = Attacher::AttachEngine3D
  Height = 2
  Length = 6
  Placement = pos=(3,62,23) rot=(0,0,1;3.14159rad)
  Width = 10
FEATURE [Part::Box] Box473  label="Krychle473"
  AttacherType = Attacher::AttachEngine3D
  Height = 2
  Length = 6
  Placement = pos=(-41.7193,45.9619,23) rot=(0,0,1;3.92699rad)
  Width = 10
FEATURE [Part::Box] Box474  label="Krychle474"
  AttacherType = Attacher::AttachEngine3D
  Height = 6
  Length = 6
  Placement = pos=(48,-45,35) rot=(0,0,1;0rad)
  Width = 2
FEATURE [Part::Box] Box475  label="Krychle475"
  AttacherType = Attacher::AttachEngine3D
  Height = 6
  Length = 6
  Placement = pos=(-54,-45,35) rot=(0,0,1;0rad)
  Width = 2
FEATURE [Part::Compound] Compound853
  Links = -> [Box474,Box475]
  Placement = pos=(0,0,-11) rot=(0,0,1;0rad)
FEATURE [Part::Compound] Compound854
  Links = -> [Cylinder1304,Cylinder1305,Cylinder1301,Cylinder1298,Cylinder1302,Cylinder1300,Cylinder1303,Cylinder1306]
FEATURE [Part::Compound] Compound856
  Links = -> [Cylinder1308,Cylinder1309]
  Placement = pos=(0,8,2) rot=(0,0,1;0rad)
FEATURE [Part::Compound] Compound857
  Links = -> [Box472,Box473,Box471,Box470,Box469,Box468,Box467,Box466]
  Placement = pos=(0,0,1) rot=(0,0,1;0rad)
FEATURE [Part::Compound] Compound858
  Links = -> [Cylinder1297,Cylinder1299]
FEATURE [Part::Compound] Compound859
  Links = -> [Box464,Box465]
FEATURE [Part::Cut] Cut460
  Base = -> Compound859
  Tool = -> Compound854
FEATURE [Part::Cut] Cut461
  Base = -> Cut460
  Placement = pos=(0,0,10) rot=(0,0,1;0rad)
  Tool = -> Compound858
FEATURE [Part::Cut] Cut465
  Base = -> Cut461
  Tool = -> Cylinder1307
FEATURE [Part::FeaturePython] Tube090  # WARN: FeaturePython — macro-defined, semantics opaque (R4)
  AttacherType = Attacher::AttachEngine3D
  Height = 25
  InnerRadius = 53
  OuterRadius = 60
  Placement = pos=(0,0,20) rot=(0,0,1;0rad)
FEATURE [Part::Cut] Cut463
  Base = -> Tube090
  Tool = -> Torus004
FEATURE [Part::Cylinder] Cylinder1310  label="Válec1310"
  Angle = 360
  AttacherType = Attacher::AttachEngine3D
  Height = 40
  Placement = pos=(-51,-40,38) rot=(1,0,0;1.5708rad)
  Radius = 1.5
FEATURE [Part::Cylinder] Cylinder1311  label="Válec1311"
  Angle = 360
  AttacherType = Attacher::AttachEngine3D
  Height = 40
  Placement = pos=(51,-40,38) rot=(1,0,0;1.5708rad)
  Radius = 1.5
FEATURE [Part::Compound] Compound851
  Links = -> [Cylinder1310,Cylinder1311]
  Placement = pos=(0,8,-11) rot=(0,0,1;0rad)
FEATURE [Part::Cylinder] Cylinder1312  label="Válec1312"
  Angle = 360
  AttacherType = Attacher::AttachEngine3D
  Height = 10
  Placement = pos=(-40,0,36) rot=(0,0,1;0rad)
  Radius = 3.5
FEATURE [Part::Cut] Cut462
  Base = -> Cut463
  Tool = -> Cylinder1312
FEATURE [Part::Cylinder] Cylinder1313  label="Válec1313"
  Angle = 360
  AttacherType = Attacher::AttachEngine3D
  Height = 20
  Placement = pos=(39.598,-39.598,2) rot=(0,0,1;0.785398rad)
  Radius = 1.5
FEATURE [Part::Cylinder] Cylinder1314  label="Válec1314"
  Angle = 360
  AttacherType = Attacher::AttachEngine3D
  Height = 50
  Placement = pos=(-51.5,0,34) rot=(0,0,1;0rad)
  Radius = 3.5
FEATURE [Part::Cut] Cut456  label="J-max_lozo-harmo006"
  Base = -> Cut462
  Tool = -> Cylinder1314
FEATURE [Part::Cylinder] Cylinder1315  label="Válec1315"
  Angle = 360
  AttacherType = Attacher::AttachEngine3D
  Height = 20
  Placement = pos=(0,-56,2) rot=(0,0,1;0rad)
  Radius = 1.5
FEATURE [Part::Cylinder] Cylinder1316  label="Válec1316"
  Angle = 360
  AttacherType = Attacher::AttachEngine3D
  Height = 20
  Placement = pos=(56,0,2) rot=(0,0,1;1.5708rad)
  Radius = 1.5
FEATURE [Part::Cylinder] Cylinder1317  label="Válec1317"
  Angle = 360
  AttacherType = Attacher::AttachEngine3D
  Height = 20
  Placement = pos=(39.598,39.598,2) rot=(0,0,1;2.35619rad)
  Radius = 1.5
FEATURE [Part::Cylinder] Cylinder1318  label="Válec1318"
  Angle = 360
  AttacherType = Attacher::AttachEngine3D
  Height = 20
  Placement = pos=(-1.2e-14,56,2) rot=(0,0,1;3.14159rad)
  Radius = 1.5
FEATURE [Part::Cylinder] Cylinder1319  label="Válec1319"
  Angle = 360
  AttacherType = Attacher::AttachEngine3D
  Height = 20
  Placement = pos=(-39.598,39.598,2) rot=(0,0,1;3.92699rad)
  Radius = 1.5
FEATURE [Part::Cylinder] Cylinder1320  label="Válec1320"
  Angle = 360
  AttacherType = Attacher::AttachEngine3D
  Height = 20
  Placement = pos=(-56,-1.3e-14,2) rot=(0,0,-1;1.5708rad)
  Radius = 1.5
FEATURE [Part::Cylinder] Cylinder1321  label="Válec1321"
  Angle = 360
  AttacherType = Attacher::AttachEngine3D
  Height = 20
  Placement = pos=(-39.598,-39.598,2) rot=(0,0,-1;0.785398rad)
  Radius = 1.5
FEATURE [Part::Compound] Compound852
  Links = -> [Cylinder1315,Cylinder1313,Cylinder1316,Cylinder1317,Cylinder1318,Cylinder1319,Cylinder1320,Cylinder1321]
  Placement = pos=(0,0,10) rot=(0,0,1;0rad)
FEATURE [Part::Cut] Cut457
  Base = -> Cut456
  Tool = -> Compound852
FEATURE [Part::Box] Box476  label="Krychle476"
  AttacherType = Attacher::AttachEngine3D
  Height = 2
  Length = 6
  Placement = pos=(-3,-60,23) rot=(0,0,1;0rad)
  Width = 8
FEATURE [Part::Box] Box477  label="Krychle477"
  AttacherType = Attacher::AttachEngine3D
  Height = 2
  Length = 6
  Placement = pos=(40.3051,-44.5477,23) rot=(0,0,1;0.785398rad)
  Width = 8
FEATURE [Part::Box] Box478  label="Krychle478"
  AttacherType = Attacher::AttachEngine3D
  Height = 2
  Length = 6
  Placement = pos=(60,-3,23) rot=(0,0,1;1.5708rad)
  Width = 8
FEATURE [Part::Box] Box479  label="Krychle479"
  AttacherType = Attacher::AttachEngine3D
  Height = 2
  Length = 6
  Placement = pos=(44.5477,40.3051,23) rot=(0,0,1;2.35619rad)
  Width = 8
FEATURE [Part::Box] Box480  label="Krychle480"
  AttacherType = Attacher::AttachEngine3D
  Height = 2
  Length = 6
  Placement = pos=(3,60,23) rot=(0,0,1;3.14159rad)
  Width = 8
FEATURE [Part::Box] Box481  label="Krychle481"
  AttacherType = Attacher::AttachEngine3D
  Height = 2
  Length = 6
  Placement = pos=(-40.3051,44.5477,23) rot=(0,0,1;3.92699rad)
  Width = 8
FEATURE [Part::Box] Box482  label="Krychle482"
  AttacherType = Attacher::AttachEngine3D
  Height = 2
  Length = 6
  Placement = pos=(-60,3,23) rot=(0,0,-1;1.5708rad)
  Width = 8
FEATURE [Part::Box] Box483  label="Krychle483"
  AttacherType = Attacher::AttachEngine3D
  Height = 2
  Length = 6
  Placement = pos=(-44.5477,-40.3051,23) rot=(0,0,-1;0.785398rad)
  Width = 8
FEATURE [Part::Compound] Compound855
  Links = -> [Box476,Box477,Box478,Box479,Box480,Box481,Box482,Box483]
  Placement = pos=(0,0,1) rot=(0,0,1;0rad)
FEATURE [Part::Cut] Cut464
  Base = -> Cut457
  Placement = pos=(0,0,12) rot=(0,0,1;0rad)
  Tool = -> Compound855
FEATURE [Part::Cylinder] Cylinder1322  label="Válec1322"
  Angle = 360
  AttacherType = Attacher::AttachEngine3D
  Height = 25
  Placement = pos=(0,0,20) rot=(0,0,1;0rad)
  Radius = 60
FEATURE [Part::Box] Box484  label="Krychle484"
  AttacherType = Attacher::AttachEngine3D
  Height = 25
  Length = 108
  Placement = pos=(-54,-53,20) rot=(0,0,1;0rad)
  Width = 46
FEATURE [Part::Cut] Cut458
  Base = -> Box484
  Tool = -> Cylinder1322
FEATURE [Part::Cylinder] Cylinder1323  label="Válec1323"
  Angle = 360
  AttacherType = Attacher::AttachEngine3D
  Height = 40
  Placement = pos=(0,-17,27) rot=(1,0,0;1.5708rad)
  Radius = 59
FEATURE [Part::Box] Box485  label="Krychle485"
  AttacherType = Attacher::AttachEngine3D
  Height = 6
  Length = 6
  Placement = pos=(36,-47,56) rot=(0,0,1;0rad)
  Width = 2
FEATURE [Part::Cylinder] Cylinder1324  label="Válec1324"
  Angle = 360
  AttacherType = Attacher::AttachEngine3D
  Height = 40
  Placement = pos=(39,-40,59) rot=(1,0,0;1.5708rad)
  Radius = 1.5
FEATURE [Part::Cylinder] Cylinder1325  label="Válec1325"
  Angle = 360
  AttacherType = Attacher::AttachEngine3D
  Height = 40
  Placement = pos=(-39,-40,59) rot=(1,0,0;1.5708rad)
  Radius = 1.5
FEATURE [Part::Compound] Compound847
  Links = -> [Cylinder1324,Cylinder1325]
  Placement = pos=(0,0,-5) rot=(0,0,1;0rad)
FEATURE [Part::Box] Box486  label="Krychle486"
  AttacherType = Attacher::AttachEngine3D
  Height = 6
  Length = 6
  Placement = pos=(-42,-47,56) rot=(0,0,1;0rad)
  Width = 2
FEATURE [Part::Compound] Compound850
  Links = -> [Box486,Box485]
  Placement = pos=(0,2,-5) rot=(0,0,1;0rad)
FEATURE [Part::Box] Box487  label="Krychle487"
  AttacherType = Attacher::AttachEngine3D
  Height = 6
  Length = 6
  Placement = pos=(36,-47,56) rot=(0,0,1;0rad)
  Width = 2
FEATURE [Part::Box] Box488  label="Krychle488"
  AttacherType = Attacher::AttachEngine3D
  Height = 6
  Length = 6
  Placement = pos=(-42,-47,56) rot=(0,0,1;0rad)
  Width = 2
FEATURE [Part::Compound] Compound849
  Links = -> [Box488,Box487]
  Placement = pos=(0,2,-5) rot=(0,0,1;0rad)
FEATURE [Part::Cut] Cut459
  Base = -> Cut464
  Tool = -> Compound849
FEATURE [Part::Cut] Cut466
  Base = -> Cut465
  Tool = -> Compound857
FEATURE [Part::Cut] Cut467
  Base = -> Cut466
  Placement = pos=(0,0,12) rot=(0,0,1;0rad)
  Tool = -> Compound856
FEATURE [Part::Cut] Cut468
  Base = -> Cut458
  Tool = -> Compound851
FEATURE [Part::Cut] Cut455
  Base = -> Cut468
  Placement = pos=(0,0,12) rot=(0,0,1;0rad)
  Tool = -> Compound853
FEATURE [Part::Common] Common002
  Base = -> Cut455
  Tool = -> Cylinder1323
FEATURE [Part::Cut] Cut470
  Base = -> Common002
  Tool = -> Compound850
FEATURE [Part::Cut] Cut471
  Base = -> Cut470
  Tool = -> Compound847
FEATURE [Part::Fillet] Fillet019
  Base = -> Cut467
  Edges = 2 edges r=8: [Edge8,Edge63]
FEATURE [Part::Cylinder] Cylinder1326  label="Válec1326"
  Angle = 360
  AttacherType = Attacher::AttachEngine3D
  Height = 40
  Placement = pos=(39,-40,59) rot=(1,0,0;1.5708rad)
  Radius = 1.5
FEATURE [Part::Cylinder] Cylinder1327  label="Válec1327"
  Angle = 360
  AttacherType = Attacher::AttachEngine3D
  Height = 40
  Placement = pos=(-39,-40,59) rot=(1,0,0;1.5708rad)
  Radius = 1.5
FEATURE [Part::Compound] Compound848
  Links = -> [Cylinder1326,Cylinder1327]
  Placement = pos=(0,2,-5) rot=(0,0,1;0rad)
FEATURE [Part::Cut] Cut469
  Base = -> Cut459
  Tool = -> Compound848
FEATURE [Part::Compound] Compound860  label="J-max-deep_bearing-ring"
  Links = -> [Cut469,Fillet019,Cut471]
  Placement = pos=(0,0,-14) rot=(0,0,1;0rad)
FEATURE [Part::Cylinder] Cylinder1328  label="Válec1328"
  Angle = 360
  AttacherType = Attacher::AttachEngine3D
  Height = 40
  Placement = pos=(0,-17,21) rot=(1,0,0;1.5708rad)
  Radius = 59
FEATURE [Part::Common] Common003
  Base = -> Fillet016
  Tool = -> Cylinder1328
FEATURE [Part::Compound] Compound  label="J-max-super-deep_monoblok"
  Links = -> [Fillet017,Cut420,Cut423,Cut428,Fillet,Common003]
FEATURE [Part::Cylinder] Cylinder1333  label="Válec1333"
  Angle = 360
  AttacherType = Attacher::AttachEngine3D
  Height = 50
  Placement = pos=(0,0,-10) rot=(0,0,1;0rad)
  Radius = 2.8
FEATURE [Part::Cylinder] Cylinder1334  label="Válec1334"
  Angle = 360
  AttacherType = Attacher::AttachEngine3D
  Height = 100
  Placement = pos=(0,0,-10) rot=(0,0,1;0rad)
  Radius = 2.8
FEATURE [Part::Cylinder] Cylinder1335  label="Válec1335"
  Angle = 360
  AttacherType = Attacher::AttachEngine3D
  Height = 100
  Placement = pos=(0,0,-10) rot=(0,0,1;0rad)
  Radius = 2.8
FEATURE [Part::Cylinder] Cylinder1336  label="Válec1336"
  Angle = 360
  AttacherType = Attacher::AttachEngine3D
  Height = 100
  Placement = pos=(0,0,-10) rot=(0,0,1;0rad)
  Radius = 2.8
FEATURE [Part::FeaturePython] wormgear058  # WARN: FeaturePython — macro-defined, semantics opaque (R4)
  AttacherType = Attacher::AttachEngine3D
  Placement = pos=(0,0,37) rot=(0,0,1;0.604757rad)
  beta = 41.1859
  clearance = 0.25
  diameter = 24
  head = 0
  height = 12
  module = 1.5
  pressure_angle = 20
  reverse_pitch = true
  teeth = 14
  version = 0.0.3
FEATURE [Part::FeaturePython] wormgear059  # WARN: FeaturePython — macro-defined, semantics opaque (R4)
  AttacherType = Attacher::AttachEngine3D
  Placement = pos=(0,0,12) rot=(0,0,1;0.551524rad)
  beta = 40.6013
  clearance = 0.2
  diameter = 28
  head = 0
  height = 12
  module = 1.5
  pressure_angle = 25
  reverse_pitch = true
  teeth = 16
  version = 0.0.3
FEATURE [Part::FeaturePython] wormgear060  # WARN: FeaturePython — macro-defined, semantics opaque (R4)
  AttacherType = Attacher::AttachEngine3D
  Placement = pos=(0,0,24) rot=(0,0,1;0.261799rad)
  beta = 41.1859
  clearance = 0.25
  diameter = 24
  head = 0
  height = 13
  module = 1.5
  pressure_angle = 20
  reverse_pitch = false
  teeth = 14
  version = 0.0.3
FEATURE [Part::FeaturePython] wormgear061  # WARN: FeaturePython — macro-defined, semantics opaque (R4)
  AttacherType = Attacher::AttachEngine3D
  Placement = pos=(0,0,0) rot=(0,0,1;0.336849rad)
  beta = 40.6013
  clearance = 0.2
  diameter = 28
  head = 0
  height = 12
  module = 1.5
  pressure_angle = 25
  reverse_pitch = false
  teeth = 16
  version = 0.0.3
FEATURE [Part::Cut] Cut476
  Base = -> wormgear061
  Tool = -> Cylinder1334
FEATURE [Part::Cut] Cut477
  Base = -> wormgear060
  Tool = -> Cylinder1333
FEATURE [Part::Cut] Cut478
  Base = -> wormgear058
  Tool = -> Cylinder1336
FEATURE [Part::Cut] Cut479
  Base = -> wormgear059
  Tool = -> Cylinder1335
FEATURE [Part::Compound] Compound862  label="J-max-deep_outer-planeo_origo-version"
  Links = -> [Cut476,Cut478,Cut479,Cut477]
  Placement = pos=(0,-25,-6) rot=(0,0,1;0.122173rad)
FEATURE [Part::Box] Box489  label="Krychle489"
  AttacherType = Attacher::AttachEngine3D
  Height = 6
  Length = 6
  Placement = pos=(-54,-45,4) rot=(0,0,1;0rad)
  Width = 2
FEATURE [Part::Cylinder] Cylinder1337  label="Válec1337"
  Angle = 360
  AttacherType = Attacher::AttachEngine3D
  Height = 20
  Placement = pos=(-39.6,-39.6,-10) rot=(0,0,-1;0.785398rad)
  Radius = 4
FEATURE [Part::Cylinder] Cylinder1338  label="Válec1338"
  Angle = 360
  AttacherType = Attacher::AttachEngine3D
  Height = 40
  Placement = pos=(59,-17,0) rot=(0,0,1;0rad)
  Radius = 10
FEATURE [Part::Box] Box490  label="Krychle490"
  AttacherType = Attacher::AttachEngine3D
  Height = 6
  Length = 6
  Placement = pos=(48,-45,4) rot=(0,0,1;0rad)
  Width = 2
FEATURE [Part::Cylinder] Cylinder1339  label="Válec1339"
  Angle = 360
  AttacherType = Attacher::AttachEngine3D
  Height = 20
  Placement = pos=(51,-40,7) rot=(1,0,0;1.5708rad)
  Radius = 1.5
FEATURE [Part::Cylinder] Cylinder1340  label="Válec1340"
  Angle = 360
  AttacherType = Attacher::AttachEngine3D
  Height = 20
  Placement = pos=(-24,-40,-5) rot=(1,0,0;1.5708rad)
  Radius = 1.5
FEATURE [Part::Cylinder] Cylinder1341  label="Válec1341"
  Angle = 360
  AttacherType = Attacher::AttachEngine3D
  Height = 8
  Placement = pos=(0,0,20) rot=(0,0,1;0rad)
  Radius = 52
FEATURE [Part::Box] Box491  label="Krychle491"
  AttacherType = Attacher::AttachEngine3D
  Height = 6
  Length = 6
  Placement = pos=(-27,-47,-8) rot=(0,0,1;0rad)
  Width = 2
FEATURE [Part::Cylinder] Cylinder1342  label="Válec1342"
  Angle = 360
  AttacherType = Attacher::AttachEngine3D
  Height = 40
  Placement = pos=(-59,-17,0) rot=(0,0,1;0rad)
  Radius = 10
FEATURE [Part::Box] Box492  label="Krychle492"
  AttacherType = Attacher::AttachEngine3D
  Height = 8
  Length = 108
  Placement = pos=(-54,-53,20) rot=(0,0,1;0rad)
  Width = 36
FEATURE [Part::Cut] Cut481
  Base = -> Box492
  Placement = pos=(0,0,-20) rot=(0,0,1;0rad)
  Tool = -> Cylinder1341
FEATURE [Part::Box] Box493  label="Krychle493"
  AttacherType = Attacher::AttachEngine3D
  Height = 6
  Length = 6
  Placement = pos=(21,-47,-8) rot=(0,0,1;0rad)
  Width = 2
FEATURE [Part::Cylinder] Cylinder1343  label="Válec1343"
  Angle = 360
  AttacherType = Attacher::AttachEngine3D
  Height = 20
  Placement = pos=(24,-40,-5) rot=(1,0,0;1.5708rad)
  Radius = 1.5
FEATURE [Part::Cylinder] Cylinder1344  label="Válec1344"
  Angle = 360
  AttacherType = Attacher::AttachEngine3D
  Height = 20
  Placement = pos=(39.6,-39.6,-10) rot=(0,0,1;0.785398rad)
  Radius = 4
FEATURE [Part::Cylinder] Cylinder1345  label="Válec1345"
  Angle = 360
  AttacherType = Attacher::AttachEngine3D
  Height = 20
  Placement = pos=(-51,-40,7) rot=(1,0,0;1.5708rad)
  Radius = 1.5
FEATURE [Part::Compound] Compound863
  Links = -> [Cylinder1340,Cylinder1343,Cylinder1339,Cylinder1345]
FEATURE [Part::Compound] Compound864
  Links = -> [Box491,Box493,Box490,Box489]
FEATURE [Part::Compound] Compound865
  Links = -> [Cylinder1338,Cylinder1342]
FEATURE [Part::Cut] Cut484
  Base = -> Cut481
  Placement = pos=(0,0,-8) rot=(0,0,1;0rad)
  Tool = -> Compound865
FEATURE [Part::Compound] Compound866
  Links = -> [Cylinder1337,Cylinder1344]
FEATURE [Part::Cut] Cut482
  Base = -> Cut484
  Tool = -> Compound866
FEATURE [Part::Cut] Cut483
  Base = -> Cut482
  Tool = -> Compound864
FEATURE [Part::Cut] Cut480
  Base = -> Cut483
  Tool = -> Compound863
FEATURE [Part::Fillet] Fillet020
  Base = -> Cut480
  Edges = 2 edges r=12: [Edge2,Edge38]
  Placement = pos=(0,0,-6) rot=(0,0,1;0rad)
FEATURE [Part::Cylinder] Cylinder1346  label="Válec1346"
  Angle = 360
  AttacherType = Attacher::AttachEngine3D
  Height = 50
  Placement = pos=(0,-56,2) rot=(0,0,1;0rad)
  Radius = 1.5
FEATURE [Part::Cylinder] Cylinder1347  label="Válec1347"
  Angle = 360
  AttacherType = Attacher::AttachEngine3D
  Height = 50
  Placement = pos=(-39.598,39.598,2) rot=(0,0,1;3.92699rad)
  Radius = 1.5
FEATURE [Part::Box] Box494  label="Krychle494"
  AttacherType = Attacher::AttachEngine3D
  Height = 12
  Length = 10
  Placement = pos=(50,-43,10) rot=(0,0,1;0rad)
  Width = 43
FEATURE [Part::Cylinder] Cylinder1348  label="Válec1348"
  Angle = 360
  AttacherType = Attacher::AttachEngine3D
  Height = 16
  Placement = pos=(-60,-43,10) rot=(0,0,1;0rad)
  Radius = 6
FEATURE [Part::Cylinder] Cylinder1349  label="Válec1349"
  Angle = 360
  AttacherType = Attacher::AttachEngine3D
  Height = 50
  Placement = pos=(39.598,39.598,2) rot=(0,0,1;2.35619rad)
  Radius = 1.5
FEATURE [Part::Cylinder] Cylinder1350  label="Válec1350"
  Angle = 360
  AttacherType = Attacher::AttachEngine3D
  Height = 50
  Placement = pos=(-39.598,-39.598,2) rot=(0,0,-1;0.785398rad)
  Radius = 1.5
FEATURE [Part::Cylinder] Cylinder1351  label="Válec1351"
  Angle = 360
  AttacherType = Attacher::AttachEngine3D
  Height = 50
  Placement = pos=(56,0,2) rot=(0,0,1;1.5708rad)
  Radius = 1.5
FEATURE [Part::Box] Box495  label="Krychle495"
  AttacherType = Attacher::AttachEngine3D
  Height = 12
  Length = 10
  Placement = pos=(-60,-43,10) rot=(0,0,1;0rad)
  Width = 43
FEATURE [Part::Cylinder] Cylinder1352  label="Válec1352"
  Angle = 360
  AttacherType = Attacher::AttachEngine3D
  Height = 16
  Placement = pos=(60,-43,10) rot=(0,0,1;0rad)
  Radius = 6
FEATURE [Part::Cylinder] Cylinder1353  label="Válec1353"
  Angle = 360
  AttacherType = Attacher::AttachEngine3D
  Height = 50
  Placement = pos=(-1.2e-14,56,2) rot=(0,0,1;3.14159rad)
  Radius = 1.5
FEATURE [Part::Cylinder] Cylinder1354  label="Válec1354"
  Angle = 360
  AttacherType = Attacher::AttachEngine3D
  Height = 50
  Placement = pos=(-56,-1.3e-14,2) rot=(0,0,-1;1.5708rad)
  Radius = 1.5
FEATURE [Part::Cylinder] Cylinder1355  label="Válec1355"
  Angle = 360
  AttacherType = Attacher::AttachEngine3D
  Height = 50
  Placement = pos=(39.598,-39.598,2) rot=(0,0,1;0.785398rad)
  Radius = 1.5
FEATURE [Part::Compound] Compound867
  Links = -> [Box495,Box494]
FEATURE [Part::Compound] Compound868
  Links = -> [Cylinder1346,Cylinder1355,Cylinder1351,Cylinder1349,Cylinder1353,Cylinder1347,Cylinder1354,Cylinder1350]
FEATURE [Part::Cut] Cut485
  Base = -> Compound867
  Tool = -> Compound868
FEATURE [Part::Compound] Compound869
  Links = -> [Cylinder1352,Cylinder1348]
FEATURE [Part::Cut] Cut486
  Base = -> Cut485
  Tool = -> Compound869
FEATURE [Part::Fillet] Fillet021
  Base = -> Cut486
  Edges = 2 edges r=8: [Edge4,Edge43]
  Placement = pos=(0,0,-4) rot=(0,0,1;0rad)
FEATURE [Part::Cylinder] Cylinder1364  label="Válec1364"
  Angle = 360
  AttacherType = Attacher::AttachEngine3D
  Height = 50
  Placement = pos=(-39.598,39.598,2) rot=(0,0,1;3.92699rad)
  Radius = 1.5
FEATURE [Part::Cylinder] Cylinder1365  label="Válec1365"
  Angle = 360
  AttacherType = Attacher::AttachEngine3D
  Height = 50
  Placement = pos=(-56,-1.3e-14,2) rot=(0,0,-1;1.5708rad)
  Radius = 1.5
FEATURE [Part::Cylinder] Cylinder1366  label="Válec1366"
  Angle = 360
  AttacherType = Attacher::AttachEngine3D
  Height = 50
  Placement = pos=(39.598,39.598,2) rot=(0,0,1;2.35619rad)
  Radius = 1.5
FEATURE [Part::Cylinder] Cylinder1367  label="Válec1367"
  Angle = 360
  AttacherType = Attacher::AttachEngine3D
  Height = 50
  Placement = pos=(-39.598,-39.598,2) rot=(0,0,-1;0.785398rad)
  Radius = 1.5
FEATURE [Part::Cylinder] Cylinder1368  label="Válec1368"
  Angle = 360
  AttacherType = Attacher::AttachEngine3D
  Height = 16
  Placement = pos=(0,0,20) rot=(0,0,1;0rad)
  Radius = 52
FEATURE [Part::Cylinder] Cylinder1369  label="Válec1369"
  Angle = 360
  AttacherType = Attacher::AttachEngine3D
  Height = 50
  Placement = pos=(0,-56,2) rot=(0,0,1;0rad)
  Radius = 1.5
FEATURE [Part::Cylinder] Cylinder1370  label="Válec1370"
  Angle = 360
  AttacherType = Attacher::AttachEngine3D
  Height = 50
  Placement = pos=(-1.2e-14,56,2) rot=(0,0,1;3.14159rad)
  Radius = 1.5
FEATURE [Part::Cylinder] Cylinder1371  label="Válec1371"
  Angle = 360
  AttacherType = Attacher::AttachEngine3D
  Height = 50
  Placement = pos=(39.598,-39.598,2) rot=(0,0,1;0.785398rad)
  Radius = 1.5
FEATURE [Part::Compound] Compound871
  Links = -> [Cylinder1369,Cylinder1371,Cylinder1366,Cylinder1370,Cylinder1364,Cylinder1365,Cylinder1367]
FEATURE [Part::Box] Box497  label="Krychle497"
  AttacherType = Attacher::AttachEngine3D
  Height = 12
  Length = 108
  Placement = pos=(-54,-53,20) rot=(0,0,1;0rad)
  Width = 36
FEATURE [Part::Cut] Cut490
  Base = -> Box497
  Placement = pos=(0,0,-10) rot=(0,0,1;0rad)
  Tool = -> Cylinder1368
FEATURE [Part::Cut] Cut489
  Base = -> Cut490
  Placement = pos=(0,0,-4) rot=(0,0,1;0rad)
  Tool = -> Compound871
FEATURE [Part::FeaturePython] Tube091  # WARN: FeaturePython — macro-defined, semantics opaque (R4)
  AttacherType = Attacher::AttachEngine3D
  Height = 8
  InnerRadius = 42
  OuterRadius = 52
  Placement = pos=(0,0,-8) rot=(0,0,1;0rad)
FEATURE [Part::Cylinder] Cylinder1372  label="Válec1372"
  Angle = 360
  AttacherType = Attacher::AttachEngine3D
  Height = 20
  Placement = pos=(51,-40,7) rot=(1,0,0;1.5708rad)
  Radius = 1.5
FEATURE [Part::Cylinder] Cylinder1373  label="Válec1373"
  Angle = 360
  AttacherType = Attacher::AttachEngine3D
  Height = 20
  Placement = pos=(0,45,-18) rot=(0,0,1;0rad)
  Radius = 1.5
FEATURE [Part::Cylinder] Cylinder1374  label="Válec1374"
  Angle = 360
  AttacherType = Attacher::AttachEngine3D
  Height = 20
  Placement = pos=(-24,-40,-5) rot=(1,0,0;1.5708rad)
  Radius = 1.5
FEATURE [Part::Box] Box498  label="Krychle498"
  AttacherType = Attacher::AttachEngine3D
  Height = 2
  Length = 6
  Placement = pos=(3,-41,-4) rot=(0,0,1;3.14159rad)
  Width = 8
FEATURE [Part::Cylinder] Cylinder1375  label="Válec1375"
  Angle = 360
  AttacherType = Attacher::AttachEngine3D
  Height = 20
  Placement = pos=(-51,-40,7) rot=(1,0,0;1.5708rad)
  Radius = 1.5
FEATURE [Part::Box] Box499  label="Krychle499"
  AttacherType = Attacher::AttachEngine3D
  Height = 6
  Length = 6
  Placement = pos=(48,-45,4) rot=(0,0,1;0rad)
  Width = 2
FEATURE [Part::Box] Box500  label="Krychle500"
  AttacherType = Attacher::AttachEngine3D
  Height = 2
  Length = 6
  Placement = pos=(-41,-3,-4) rot=(0,0,1;1.5708rad)
  Width = 8
FEATURE [Part::Cylinder] Cylinder1376  label="Válec1376"
  Angle = 360
  AttacherType = Attacher::AttachEngine3D
  Height = 20
  Placement = pos=(24,-40,-5) rot=(1,0,0;1.5708rad)
  Radius = 1.5
FEATURE [Part::Compound] Compound875
  Links = -> [Cylinder1374,Cylinder1376,Cylinder1372,Cylinder1375]
FEATURE [Part::Cylinder] Cylinder1377  label="Válec1377"
  Angle = 360
  AttacherType = Attacher::AttachEngine3D
  Height = 20
  Placement = pos=(1.4e-14,-45,-18) rot=(0,0,1;3.14159rad)
  Radius = 1.5
FEATURE [Part::Box] Box501  label="Krychle501"
  AttacherType = Attacher::AttachEngine3D
  Height = 2
  Length = 6
  Placement = pos=(41,3,-4) rot=(0,0,-1;1.5708rad)
  Width = 8
FEATURE [Part::Cylinder] Cylinder1378  label="Válec1378"
  Angle = 360
  AttacherType = Attacher::AttachEngine3D
  Height = 20
  Placement = pos=(-45,-6e-15,-18) rot=(0,0,1;1.5708rad)
  Radius = 1.5
FEATURE [Part::Cylinder] Cylinder1379  label="Válec1379"
  Angle = 360
  AttacherType = Attacher::AttachEngine3D
  Height = 20
  Placement = pos=(-31.8198,-31.8198,-18) rot=(0,0,1;2.35619rad)
  Radius = 1.5
FEATURE [Part::Cylinder] Cylinder1380  label="Válec1380"
  Angle = 360
  AttacherType = Attacher::AttachEngine3D
  Height = 20
  Placement = pos=(45,1.9e-14,-18) rot=(0,0,-1;1.5708rad)
  Radius = 1.5
FEATURE [Part::Box] Box502  label="Krychle502"
  AttacherType = Attacher::AttachEngine3D
  Height = 2
  Length = 6
  Placement = pos=(-3,41,-4) rot=(0,0,1;0rad)
  Width = 8
FEATURE [Part::Box] Box503  label="Krychle503"
  AttacherType = Attacher::AttachEngine3D
  Height = 2
  Length = 6
  Placement = pos=(-31.1127,26.8701,-4) rot=(0,0,1;0.785398rad)
  Width = 8
FEATURE [Part::Box] Box504  label="Krychle504"
  AttacherType = Attacher::AttachEngine3D
  Height = 6
  Length = 6
  Placement = pos=(-27,-47,-8) rot=(0,0,1;0rad)
  Width = 2
FEATURE [Part::Box] Box505  label="Krychle505"
  AttacherType = Attacher::AttachEngine3D
  Height = 2
  Length = 6
  Placement = pos=(31.1127,-26.8701,-4) rot=(0,0,1;3.92699rad)
  Width = 8
FEATURE [Part::Cylinder] Cylinder1381  label="Válec1381"
  Angle = 360
  AttacherType = Attacher::AttachEngine3D
  Height = 20
  Placement = pos=(31.8198,31.8198,-18) rot=(0,0,-1;0.785398rad)
  Radius = 1.5
FEATURE [Part::Box] Box506  label="Krychle506"
  AttacherType = Attacher::AttachEngine3D
  Height = 6
  Length = 6
  Placement = pos=(-54,-45,4) rot=(0,0,1;0rad)
  Width = 2
FEATURE [Part::Cylinder] Cylinder1382  label="Válec1382"
  Angle = 360
  AttacherType = Attacher::AttachEngine3D
  Height = 20
  Placement = pos=(-31.8198,31.8198,-18) rot=(0,0,1;0.785398rad)
  Radius = 1.5
FEATURE [Part::Box] Box507  label="Krychle507"
  AttacherType = Attacher::AttachEngine3D
  Height = 6
  Length = 6
  Placement = pos=(21,-47,-8) rot=(0,0,1;0rad)
  Width = 2
FEATURE [Part::Compound] Compound874
  Links = -> [Box504,Box507,Box499,Box506]
FEATURE [Part::Cut] Cut494
  Base = -> Tube091
  Tool = -> Compound874
FEATURE [Part::Cut] Cut492
  Base = -> Cut494
  Tool = -> Compound875
FEATURE [Part::Cylinder] Cylinder1383  label="Válec1383"
  Angle = 360
  AttacherType = Attacher::AttachEngine3D
  Height = 20
  Placement = pos=(31.8198,-31.8198,-18) rot=(0,0,1;3.92699rad)
  Radius = 1.5
FEATURE [Part::Compound] Compound872
  Links = -> [Cylinder1373,Cylinder1382,Cylinder1378,Cylinder1379,Cylinder1377,Cylinder1383,Cylinder1380,Cylinder1381]
  Placement = pos=(0,0,0) rot=(0,0,1;0.392699rad)
FEATURE [Part::Box] Box508  label="Krychle508"
  AttacherType = Attacher::AttachEngine3D
  Height = 2
  Length = 6
  Placement = pos=(26.8701,31.1127,-4) rot=(0,0,-1;0.785398rad)
  Width = 8
FEATURE [Part::Box] Box509  label="Krychle509"
  AttacherType = Attacher::AttachEngine3D
  Height = 2
  Length = 6
  Placement = pos=(-26.8701,-31.1127,-4) rot=(0,0,1;2.35619rad)
  Width = 8
FEATURE [Part::Compound] Compound873
  Links = -> [Box502,Box503,Box500,Box509,Box498,Box505,Box501,Box508]
  Placement = pos=(0,0,0) rot=(0,0,1;0.392699rad)
FEATURE [Part::Cut] Cut493
  Base = -> Cut492
  Tool = -> Compound873
FEATURE [Part::Cut] Cut491
  Base = -> Cut493
  Placement = pos=(0,0,-6) rot=(0,0,1;0rad)
  Tool = -> Compound872
FEATURE [Part::Cylinder] Cylinder1384  label="Válec1384"
  Angle = 360
  AttacherType = Attacher::AttachEngine3D
  Height = 40
  Placement = pos=(-59,-17,0) rot=(0,0,1;0rad)
  Radius = 10
FEATURE [Part::Cylinder] Cylinder1385  label="Válec1385"
  Angle = 360
  AttacherType = Attacher::AttachEngine3D
  Height = 20
  Placement = pos=(-51,-40,7) rot=(1,0,0;1.5708rad)
  Radius = 1.5
FEATURE [Part::Box] Box510  label="Krychle510"
  AttacherType = Attacher::AttachEngine3D
  Height = 12
  Length = 108
  Placement = pos=(-54,-53,20) rot=(0,0,1;0rad)
  Width = 36
FEATURE [Part::Cylinder] Cylinder1386  label="Válec1386"
  Angle = 360
  AttacherType = Attacher::AttachEngine3D
  Height = 20
  Placement = pos=(0,0,20) rot=(0,0,1;0rad)
  Radius = 52
FEATURE [Part::Cut] Cut498
  Base = -> Box510
  Placement = pos=(0,0,-20) rot=(0,0,1;0rad)
  Tool = -> Cylinder1386
FEATURE [Part::Cylinder] Cylinder1387  label="Válec1387"
  Angle = 360
  AttacherType = Attacher::AttachEngine3D
  Height = 20
  Placement = pos=(-39.6,-39.6,-10) rot=(0,0,-1;0.785398rad)
  Radius = 4
FEATURE [Part::Box] Box511  label="Krychle511"
  AttacherType = Attacher::AttachEngine3D
  Height = 6
  Length = 6
  Placement = pos=(48,-45,4) rot=(0,0,1;0rad)
  Width = 2
FEATURE [Part::Cylinder] Cylinder1388  label="Válec1388"
  Angle = 360
  AttacherType = Attacher::AttachEngine3D
  Height = 40
  Placement = pos=(59,-17,0) rot=(0,0,1;0rad)
  Radius = 10
FEATURE [Part::Compound] Compound878
  Links = -> [Cylinder1388,Cylinder1384]
FEATURE [Part::Cut] Cut499
  Base = -> Cut498
  Tool = -> Compound878
FEATURE [Part::Cylinder] Cylinder1389  label="Válec1389"
  Angle = 360
  AttacherType = Attacher::AttachEngine3D
  Height = 20
  Placement = pos=(-20,-40,-5) rot=(1,0,0;1.5708rad)
  Radius = 1.5
FEATURE [Part::Cylinder] Cylinder1390  label="Válec1390"
  Angle = 360
  AttacherType = Attacher::AttachEngine3D
  Height = 20
  Placement = pos=(51,-40,7) rot=(1,0,0;1.5708rad)
  Radius = 1.5
FEATURE [Part::Cylinder] Cylinder1391  label="Válec1391"
  Angle = 360
  AttacherType = Attacher::AttachEngine3D
  Height = 20
  Placement = pos=(20,-40,-5) rot=(1,0,0;1.5708rad)
  Radius = 1.5
FEATURE [Part::Compound] Compound879
  Links = -> [Cylinder1389,Cylinder1391,Cylinder1390,Cylinder1385]
FEATURE [Part::Box] Box512  label="Krychle512"
  AttacherType = Attacher::AttachEngine3D
  Height = 6
  Length = 6
  Placement = pos=(-23,-47,-8) rot=(0,0,1;0rad)
  Width = 2
FEATURE [Part::Box] Box513  label="Krychle513"
  AttacherType = Attacher::AttachEngine3D
  Height = 6
  Length = 6
  Placement = pos=(-54,-45,4) rot=(0,0,1;0rad)
  Width = 2
FEATURE [Part::Cylinder] Cylinder1392  label="Válec1392"
  Angle = 360
  AttacherType = Attacher::AttachEngine3D
  Height = 20
  Placement = pos=(39.6,-39.6,-10) rot=(0,0,1;0.785398rad)
  Radius = 4
FEATURE [Part::Compound] Compound876
  Links = -> [Cylinder1387,Cylinder1392]
FEATURE [Part::Cut] Cut496
  Base = -> Cut499
  Tool = -> Compound876
FEATURE [Part::Box] Box514  label="Krychle514"
  AttacherType = Attacher::AttachEngine3D
  Height = 6
  Length = 6
  Placement = pos=(17,-47,-8) rot=(0,0,1;0rad)
  Width = 2
FEATURE [Part::Compound] Compound877
  Links = -> [Box512,Box514,Box511,Box513]
FEATURE [Part::Cut] Cut497
  Base = -> Cut496
  Tool = -> Compound877
FEATURE [Part::Cut] Cut495
  Base = -> Cut497
  Tool = -> Compound879
FEATURE [Part::Fillet] Fillet022
  Base = -> Cut495
  Edges = 2 edges r=12: [Edge3,Edge36]
  Placement = pos=(0,0,-6) rot=(0,0,1;0rad)
FEATURE [Part::Cylinder] Cylinder1393  label="Válec1393"
  Angle = 360
  AttacherType = Attacher::AttachEngine3D
  Height = 50
  Placement = pos=(31.8198,31.8198,-18) rot=(0,0,-1;0.785398rad)
  Radius = 1.5
FEATURE [Part::Cylinder] Cylinder1394  label="Válec1394"
  Angle = 360
  AttacherType = Attacher::AttachEngine3D
  Height = 50
  Placement = pos=(39.598,-39.598,2) rot=(0,0,1;0.785398rad)
  Radius = 1.5
FEATURE [Part::Cylinder] Cylinder1395  label="Válec1395"
  Angle = 360
  AttacherType = Attacher::AttachEngine3D
  Height = 50
  Placement = pos=(0,45,-18) rot=(0,0,1;0rad)
  Radius = 1.5
FEATURE [Part::Cylinder] Cylinder1396  label="Válec1396"
  Angle = 360
  AttacherType = Attacher::AttachEngine3D
  Height = 50
  Placement = pos=(1.4e-14,-45,-18) rot=(0,0,1;3.14159rad)
  Radius = 1.5
FEATURE [Part::Cylinder] Cylinder1397  label="Válec1397"
  Angle = 360
  AttacherType = Attacher::AttachEngine3D
  Height = 50
  Placement = pos=(31.8198,-31.8198,-18) rot=(0,0,1;3.92699rad)
  Radius = 1.5
FEATURE [Part::FeaturePython] wormgear062  # WARN: FeaturePython — macro-defined, semantics opaque (R4)
  AttacherType = Attacher::AttachEngine3D
  Placement = pos=(0,0,0) rot=(0,0,1;0.083427rad)
  beta = 40.5833
  clearance = 0.25
  diameter = 78.8
  head = 0
  height = 20
  module = 1.5
  pressure_angle = 20
  reverse_pitch = false
  teeth = 45
  version = 0.0.3
FEATURE [Part::FeaturePython] wormgear063  # WARN: FeaturePython — macro-defined, semantics opaque (R4)
  AttacherType = Attacher::AttachEngine3D
  Placement = pos=(0,0,0) rot=(0,0,1;0.124791rad)
  beta = 40.5833
  clearance = 0.25
  diameter = 78.8
  head = 0
  height = 20
  module = 1.5
  pressure_angle = 20
  reverse_pitch = true
  teeth = 45
  version = 0.0.3
FEATURE [Part::Cylinder] Cylinder1398  label="Válec1398"
  Angle = 360
  AttacherType = Attacher::AttachEngine3D
  Height = 20
  Placement = pos=(39.6,-39.6,-10) rot=(0,0,1;0.785398rad)
  Radius = 4
FEATURE [Part::Cylinder] Cylinder1399  label="Válec1399"
  Angle = 360
  AttacherType = Attacher::AttachEngine3D
  Height = 50
  Placement = pos=(-31.8198,31.8198,-18) rot=(0,0,1;0.785398rad)
  Radius = 1.5
FEATURE [Part::Cylinder] Cylinder1400  label="Válec1400"
  Angle = 360
  AttacherType = Attacher::AttachEngine3D
  Height = 50
  Placement = pos=(-56,-1.3e-14,2) rot=(0,0,-1;1.5708rad)
  Radius = 1.5
FEATURE [Part::Cylinder] Cylinder1401  label="Válec1401"
  Angle = 360
  AttacherType = Attacher::AttachEngine3D
  Height = 50
  Placement = pos=(45,1.9e-14,-18) rot=(0,0,-1;1.5708rad)
  Radius = 1.5
FEATURE [Part::Cylinder] Cylinder1402  label="Válec1402"
  Angle = 360
  AttacherType = Attacher::AttachEngine3D
  Height = 50
  Placement = pos=(-39.598,39.598,2) rot=(0,0,1;3.92699rad)
  Radius = 1.5
FEATURE [Part::Cylinder] Cylinder1403  label="Válec1403"
  Angle = 360
  AttacherType = Attacher::AttachEngine3D
  Height = 50
  Placement = pos=(-31.8198,-31.8198,-18) rot=(0,0,1;2.35619rad)
  Radius = 1.5
FEATURE [Part::Cylinder] Cylinder1404  label="Válec1404"
  Angle = 360
  AttacherType = Attacher::AttachEngine3D
  Height = 50
  Placement = pos=(-45,-6e-15,-18) rot=(0,0,1;1.5708rad)
  Radius = 1.5
FEATURE [Part::Compound] Compound883
  Links = -> [Cylinder1395,Cylinder1399,Cylinder1404,Cylinder1403,Cylinder1396,Cylinder1397,Cylinder1401,Cylinder1393]
  Placement = pos=(0,0,-20) rot=(0,0,1;0.392699rad)
FEATURE [Part::Cylinder] Cylinder1405  label="Válec1405"
  Angle = 360
  AttacherType = Attacher::AttachEngine3D
  Height = 50
  Placement = pos=(-39.598,-39.598,2) rot=(0,0,-1;0.785398rad)
  Radius = 1.5
FEATURE [Part::Cylinder] Cylinder1406  label="Válec1406"
  Angle = 360
  AttacherType = Attacher::AttachEngine3D
  Height = 12
  Radius = 52
FEATURE [Part::Cut] Cut500
  Base = -> Cylinder1406
  Tool = -> wormgear062
FEATURE [Part::Cylinder] Cylinder1407  label="Válec1407"
  Angle = 360
  AttacherType = Attacher::AttachEngine3D
  Height = 50
  Placement = pos=(0,-56,2) rot=(0,0,1;0rad)
  Radius = 1.5
FEATURE [Part::Cylinder] Cylinder1408  label="Válec1408"
  Angle = 360
  AttacherType = Attacher::AttachEngine3D
  Height = 50
  Placement = pos=(-1.2e-14,56,2) rot=(0,0,1;3.14159rad)
  Radius = 1.5
FEATURE [Part::Cylinder] Cylinder1409  label="Válec1409"
  Angle = 360
  AttacherType = Attacher::AttachEngine3D
  Height = 50
  Placement = pos=(39.598,39.598,2) rot=(0,0,1;2.35619rad)
  Radius = 1.5
FEATURE [Part::Cylinder] Cylinder1410  label="Válec1410"
  Angle = 360
  AttacherType = Attacher::AttachEngine3D
  Height = 12
  Radius = 60
FEATURE [Part::Cut] Cut503
  Base = -> Cylinder1410
  Placement = pos=(0,0,12) rot=(0,0,1;0.034907rad)
  Tool = -> wormgear063
FEATURE [Part::Compound] Compound882
  Links = -> [Cut503,Cut500]
FEATURE [Part::Cylinder] Cylinder1411  label="Válec1411"
  Angle = 360
  AttacherType = Attacher::AttachEngine3D
  Height = 50
  Placement = pos=(56,0,2) rot=(0,0,1;1.5708rad)
  Radius = 1.5
FEATURE [Part::Compound] Compound881
  Links = -> [Cylinder1407,Cylinder1394,Cylinder1411,Cylinder1409,Cylinder1408,Cylinder1402,Cylinder1400,Cylinder1405]
FEATURE [Part::Cut] Cut501
  Base = -> Compound882
  Tool = -> Compound881
FEATURE [Part::Cylinder] Cylinder1412  label="Válec1412"
  Angle = 360
  AttacherType = Attacher::AttachEngine3D
  Height = 20
  Placement = pos=(-39.6,-39.6,-10) rot=(0,0,-1;0.785398rad)
  Radius = 4
FEATURE [Part::Compound] Compound880
  Links = -> [Cylinder1412,Cylinder1398]
FEATURE [Part::Cut] Cut504
  Base = -> Cut501
  Tool = -> Compound880
FEATURE [Part::Cut] Cut502
  Base = -> Cut504
  Placement = pos=(0,0,-6) rot=(0,0,1;0rad)
  Tool = -> Compound883
FEATURE [Part::Cylinder] Cylinder1413  label="Válec1413"
  Angle = 360
  AttacherType = Attacher::AttachEngine3D
  Height = 40
  Placement = pos=(0,-17,13) rot=(1,0,0;1.5708rad)
  Radius = 59
FEATURE [Part::Common] Common004
  Base = -> Fillet020
  Tool = -> Cylinder1413
FEATURE [Part::Compound] Compound884  label="J-max-deep_monoblok_nohole"
  Links = -> [Fillet021,Cut489,Cut491,Fillet022,Cut502,Common004]
FEATURE [Part::FeaturePython] Tube044  label="ZKL-6017"  # WARN: FeaturePython — macro-defined, semantics opaque (R4)
  AttacherType = Attacher::AttachEngine3D
  Height = 22
  InnerRadius = 42.5
  OuterRadius = 65
  Placement = pos=(51,-79,13) rot=(1,0,0;1.5708rad)
FEATURE [Part::Box] Box104  label="Krychle104"
  AttacherType = Attacher::AttachEngine3D
  Height = 2
  Length = 10
  Placement = pos=(11,-3,6) rot=(0,0,1;0rad)
  Width = 6
FEATURE [Part::Box] Box105  label="Krychle105"
  AttacherType = Attacher::AttachEngine3D
  Height = 2
  Length = 10
  Placement = pos=(-11,3,6) rot=(0,0,1;3.14159rad)
  Width = 6
FEATURE [Part::Box] Box106  label="Krychle106"
  AttacherType = Attacher::AttachEngine3D
  Height = 2
  Length = 10
  Placement = pos=(3,11,6) rot=(0,0,1;1.5708rad)
  Width = 6
FEATURE [Part::Box] Box107  label="Krychle107"
  AttacherType = Attacher::AttachEngine3D
  Height = 2
  Length = 10
  Placement = pos=(-3,-11,6) rot=(0,0,-1;1.5708rad)
  Width = 6
FEATURE [Part::Cylinder] Cylinder272  label="Válec272"
  Angle = 360
  AttacherType = Attacher::AttachEngine3D
  Height = 16
  Placement = pos=(16,0,2) rot=(0,0,1;3.53429rad)
  Radius = 1.5
FEATURE [Part::Cylinder] Cylinder273  label="Válec273"
  Angle = 360
  AttacherType = Attacher::AttachEngine3D
  Height = 16
  Placement = pos=(-16,7e-15,2) rot=(0,0,1;0.392699rad)
  Radius = 1.5
FEATURE [Part::FeaturePython] Tube029  # WARN: FeaturePython — macro-defined, semantics opaque (R4)
  AttacherType = Attacher::AttachEngine3D
  Height = 5
  InnerRadius = 12
  OuterRadius = 52
  Placement = pos=(0,0,-100) rot=(0,0,1;0rad)
FEATURE [Part::FeaturePython] Tube030  # WARN: FeaturePython — macro-defined, semantics opaque (R4)
  AttacherType = Attacher::AttachEngine3D
  Height = 4
  InnerRadius = 12
  OuterRadius = 24.8
  Placement = pos=(0,0,-103) rot=(0,0,1;0rad)
FEATURE [Part::FeaturePython] Tube031  # WARN: FeaturePython — macro-defined, semantics opaque (R4)
  AttacherType = Attacher::AttachEngine3D
  Height = 11
  InnerRadius = 12
  OuterRadius = 20
  Placement = pos=(0,0,-111) rot=(0,0,1;0rad)
FEATURE [Part::Compound] Compound232
  Links = -> [Box104,Box106,Box105,Box107]
  Placement = pos=(0,0,-111) rot=(0,0,1;0rad)
FEATURE [Part::Cylinder] Cylinder274  label="Válec274"
  Angle = 360
  AttacherType = Attacher::AttachEngine3D
  Height = 16
  Placement = pos=(-1.2e-14,-16,2) rot=(0,0,1;1.9635rad)
  Radius = 1.5
FEATURE [Part::Cylinder] Cylinder275  label="Válec275"
  Angle = 360
  AttacherType = Attacher::AttachEngine3D
  Height = 16
  Placement = pos=(2e-15,16,2) rot=(0,0,-1;1.1781rad)
  Radius = 1.5
FEATURE [Part::Compound] Compound233
  Links = -> [Cylinder272,Cylinder275,Cylinder273,Cylinder274]
  Placement = pos=(0,0,-117) rot=(0,0,1;0rad)
FEATURE [Part::Cut] Cut124
  Base = -> Tube030
  Placement = pos=(0,0,-1) rot=(0,0,1;0rad)
  Tool = -> Compound233
FEATURE [Part::Cylinder] Cylinder276  label="Válec276"
  Angle = 360
  AttacherType = Attacher::AttachEngine3D
  Height = 16
  Placement = pos=(16,0,2) rot=(0,0,1;3.53429rad)
  Radius = 1.5
FEATURE [Part::Cylinder] Cylinder277  label="Válec277"
  Angle = 360
  AttacherType = Attacher::AttachEngine3D
  Height = 16
  Placement = pos=(-16,7e-15,2) rot=(0,0,1;0.392699rad)
  Radius = 1.5
FEATURE [Part::Cylinder] Cylinder278  label="Válec278"
  Angle = 360
  AttacherType = Attacher::AttachEngine3D
  Height = 16
  Placement = pos=(-1.2e-14,-16,2) rot=(0,0,1;1.9635rad)
  Radius = 1.5
FEATURE [Part::Cylinder] Cylinder279  label="Válec279"
  Angle = 360
  AttacherType = Attacher::AttachEngine3D
  Height = 16
  Placement = pos=(2e-15,16,2) rot=(0,0,-1;1.1781rad)
  Radius = 1.5
FEATURE [Part::Compound] Compound234
  Links = -> [Cylinder276,Cylinder279,Cylinder277,Cylinder278]
  Placement = pos=(0,0,-117) rot=(0,0,1;0rad)
FEATURE [Part::Cut] Cut123
  Base = -> Tube031
  Tool = -> Compound234
FEATURE [Part::Cylinder] Cylinder280  label="Válec280"
  Angle = 360
  AttacherType = Attacher::AttachEngine3D
  Height = 16
  Placement = pos=(2e-15,16,2) rot=(0,0,-1;1.1781rad)
  Radius = 1.5
FEATURE [Part::Cylinder] Cylinder281  label="Válec281"
  Angle = 360
  AttacherType = Attacher::AttachEngine3D
  Height = 16
  Placement = pos=(16,0,2) rot=(0,0,1;3.53429rad)
  Radius = 1.5
FEATURE [Part::Cylinder] Cylinder282  label="Válec282"
  Angle = 360
  AttacherType = Attacher::AttachEngine3D
  Height = 16
  Placement = pos=(-16,7e-15,2) rot=(0,0,1;0.392699rad)
  Radius = 1.5
FEATURE [Part::Cylinder] Cylinder283  label="Válec283"
  Angle = 360
  AttacherType = Attacher::AttachEngine3D
  Height = 16
  Placement = pos=(-1.2e-14,-16,2) rot=(0,0,1;1.9635rad)
  Radius = 1.5
FEATURE [Part::Compound] Compound235
  Links = -> [Cylinder281,Cylinder280,Cylinder282,Cylinder283]
  Placement = pos=(0,0,-117) rot=(0,0,1;0rad)
FEATURE [Part::Cylinder] Cylinder284  label="Válec284"
  Angle = 360
  AttacherType = Attacher::AttachEngine3D
  Height = 20
  Placement = pos=(-45,-6e-15,-18) rot=(0,0,1;1.5708rad)
  Radius = 1.5
FEATURE [Part::Cylinder] Cylinder285  label="Válec285"
  Angle = 360
  AttacherType = Attacher::AttachEngine3D
  Height = 20
  Placement = pos=(-31.8198,-31.8198,-18) rot=(0,0,1;2.35619rad)
  Radius = 1.5
FEATURE [Part::Cylinder] Cylinder286  label="Válec286"
  Angle = 360
  AttacherType = Attacher::AttachEngine3D
  Height = 20
  Placement = pos=(0,45,-18) rot=(0,0,1;0rad)
  Radius = 1.5
FEATURE [Part::Cylinder] Cylinder287  label="Válec287"
  Angle = 360
  AttacherType = Attacher::AttachEngine3D
  Height = 20
  Placement = pos=(45,1.9e-14,-18) rot=(0,0,-1;1.5708rad)
  Radius = 1.5
FEATURE [Part::Cylinder] Cylinder288  label="Válec288"
  Angle = 360
  AttacherType = Attacher::AttachEngine3D
  Height = 20
  Placement = pos=(-31.8198,31.8198,-18) rot=(0,0,1;0.785398rad)
  Radius = 1.5
FEATURE [Part::Cylinder] Cylinder289  label="Válec289"
  Angle = 360
  AttacherType = Attacher::AttachEngine3D
  Height = 20
  Placement = pos=(31.8198,-31.8198,-18) rot=(0,0,1;3.92699rad)
  Radius = 1.5
FEATURE [Part::Cylinder] Cylinder290  label="Válec290"
  Angle = 360
  AttacherType = Attacher::AttachEngine3D
  Height = 20
  Placement = pos=(31.8198,31.8198,-18) rot=(0,0,-1;0.785398rad)
  Radius = 1.5
FEATURE [Part::Cylinder] Cylinder291  label="Válec291"
  Angle = 360
  AttacherType = Attacher::AttachEngine3D
  Height = 20
  Placement = pos=(1.4e-14,-45,-18) rot=(0,0,1;3.14159rad)
  Radius = 1.5
FEATURE [Part::Cylinder] Cylinder292  label="Válec292"
  Angle = 360
  AttacherType = Attacher::AttachEngine3D
  Height = 3
  Placement = pos=(31.8198,-31.8198,-18) rot=(0,0,1;3.92699rad)
  Radius = 3
FEATURE [Part::Cylinder] Cylinder293  label="Válec293"
  Angle = 360
  AttacherType = Attacher::AttachEngine3D
  Height = 3
  Placement = pos=(-31.8198,-31.8198,-18) rot=(0,0,1;2.35619rad)
  Radius = 3
FEATURE [Part::Cylinder] Cylinder294  label="Válec294"
  Angle = 360
  AttacherType = Attacher::AttachEngine3D
  Height = 3
  Placement = pos=(0,45,-18) rot=(0,0,1;0rad)
  Radius = 3
FEATURE [Part::Cylinder] Cylinder295  label="Válec295"
  Angle = 360
  AttacherType = Attacher::AttachEngine3D
  Height = 3
  Placement = pos=(45,1.9e-14,-18) rot=(0,0,-1;1.5708rad)
  Radius = 3
FEATURE [Part::Cylinder] Cylinder296  label="Válec296"
  Angle = 360
  AttacherType = Attacher::AttachEngine3D
  Height = 3
  Placement = pos=(-45,-6e-15,-18) rot=(0,0,1;1.5708rad)
  Radius = 3
FEATURE [Part::Cylinder] Cylinder297  label="Válec297"
  Angle = 360
  AttacherType = Attacher::AttachEngine3D
  Height = 3
  Placement = pos=(-31.8198,31.8198,-18) rot=(0,0,1;0.785398rad)
  Radius = 3
FEATURE [Part::Cylinder] Cylinder298  label="Válec298"
  Angle = 360
  AttacherType = Attacher::AttachEngine3D
  Height = 3
  Placement = pos=(1.4e-14,-45,-18) rot=(0,0,1;3.14159rad)
  Radius = 3
FEATURE [Part::Cylinder] Cylinder299  label="Válec299"
  Angle = 360
  AttacherType = Attacher::AttachEngine3D
  Height = 3
  Placement = pos=(31.8198,31.8198,-18) rot=(0,0,-1;0.785398rad)
  Radius = 3
FEATURE [Part::Cut] Cut125
  Base = -> Tube029
  Tool = -> Compound235
FEATURE [Part::Cut] Cut126
  Base = -> Cut123
  Tool = -> Compound232
FEATURE [Part::Compound] Compound236
  Links = -> [Cylinder286,Cylinder288,Cylinder284,Cylinder285,Cylinder291,Cylinder289,Cylinder287,Cylinder290]
  Placement = pos=(0,0,-87) rot=(0,0,1;0.392699rad)
FEATURE [Part::Cut] Cut127
  Base = -> Cut125
  Tool = -> Compound236
FEATURE [Part::Compound] Compound237
  Links = -> [Cylinder294,Cylinder297,Cylinder296,Cylinder293,Cylinder298,Cylinder292,Cylinder295,Cylinder299]
  Placement = pos=(0,0,-82) rot=(0,0,1;0.392699rad)
FEATURE [Part::Cut] Cut128
  Base = -> Cut127
  Tool = -> Compound237
FEATURE [Part::Chamfer] Chamfer003
  Base = -> Cut128
  Edges = 1 edges r=1: [Edge3]
FEATURE [Part::Chamfer] Chamfer004
  Base = -> Cut126
  Edges = 1 edges r=1: [Edge6]
  Placement = pos=(0,0,-1) rot=(0,0,1;0rad)
FEATURE [Part::Compound] Compound238  label="J-max_undermotor-cover"
  Links = -> [Cut124,Chamfer003,Chamfer004]
  Placement = pos=(0,0,-12) rot=(0,0,1;0rad)
FEATURE [Part::Cylinder] Cylinder623  label="Válec623"
  Angle = 360
  AttacherType = Attacher::AttachEngine3D
  Height = 20
  Placement = pos=(-31.8198,31.8198,-18) rot=(0,0,1;0.785398rad)
  Radius = 1.5
FEATURE [Part::Cylinder] Cylinder625  label="Válec625"
  Angle = 360
  AttacherType = Attacher::AttachEngine3D
  Height = 16
  Placement = pos=(2e-15,16,2) rot=(0,0,-1;1.1781rad)
  Radius = 1.5
FEATURE [Part::Cylinder] Cylinder626  label="Válec626"
  Angle = 360
  AttacherType = Attacher::AttachEngine3D
  Height = 16
  Placement = pos=(-16,7e-15,2) rot=(0,0,1;0.392699rad)
  Radius = 1.5
FEATURE [Part::Cylinder] Cylinder627  label="Válec627"
  Angle = 360
  AttacherType = Attacher::AttachEngine3D
  Height = 16
  Placement = pos=(-1.2e-14,-16,2) rot=(0,0,1;1.9635rad)
  Radius = 1.5
FEATURE [Part::Cylinder] Cylinder628  label="Válec628"
  Angle = 360
  AttacherType = Attacher::AttachEngine3D
  Height = 20
  Placement = pos=(0,45,-18) rot=(0,0,1;0rad)
  Radius = 1.5
FEATURE [Part::Cylinder] Cylinder629  label="Válec629"
  Angle = 360
  AttacherType = Attacher::AttachEngine3D
  Height = 20
  Placement = pos=(-31.8198,-31.8198,-18) rot=(0,0,1;2.35619rad)
  Radius = 1.5
FEATURE [Part::Cylinder] Cylinder630  label="Válec630"
  Angle = 360
  AttacherType = Attacher::AttachEngine3D
  Height = 16
  Placement = pos=(16,0,2) rot=(0,0,1;3.53429rad)
  Radius = 1.5
FEATURE [Part::Cylinder] Cylinder631  label="Válec631"
  Angle = 360
  AttacherType = Attacher::AttachEngine3D
  Height = 20
  Placement = pos=(45,1.9e-14,-18) rot=(0,0,-1;1.5708rad)
  Radius = 1.5
FEATURE [Part::Cylinder] Cylinder632  label="Válec632"
  Angle = 360
  AttacherType = Attacher::AttachEngine3D
  Height = 20
  Placement = pos=(-45,-6e-15,-18) rot=(0,0,1;1.5708rad)
  Radius = 1.5
FEATURE [Part::Cylinder] Cylinder633  label="Válec633"
  Angle = 360
  AttacherType = Attacher::AttachEngine3D
  Height = 20
  Placement = pos=(31.8198,31.8198,-18) rot=(0,0,-1;0.785398rad)
  Radius = 1.5
FEATURE [Part::Cylinder] Cylinder638  label="Válec638"
  Angle = 360
  AttacherType = Attacher::AttachEngine3D
  Height = 20
  Placement = pos=(31.8198,-31.8198,-18) rot=(0,0,1;3.92699rad)
  Radius = 1.5
FEATURE [Part::Cylinder] Cylinder639  label="Válec639"
  Angle = 360
  AttacherType = Attacher::AttachEngine3D
  Height = 20
  Placement = pos=(1.4e-14,-45,-18) rot=(0,0,1;3.14159rad)
  Radius = 1.5
FEATURE [Part::FeaturePython] Tube038  # WARN: FeaturePython — macro-defined, semantics opaque (R4)
  AttacherType = Attacher::AttachEngine3D
  Height = 2
  InnerRadius = 12
  OuterRadius = 52
  Placement = pos=(0,0,-100) rot=(0,0,1;0rad)
FEATURE [Part::Compound] Compound885
  Links = -> [Cylinder630,Cylinder625,Cylinder626,Cylinder627]
  Placement = pos=(0,0,-111) rot=(0,0,1;0rad)
FEATURE [Part::Compound] Compound886
  Links = -> [Cylinder628,Cylinder623,Cylinder632,Cylinder629,Cylinder639,Cylinder638,Cylinder631,Cylinder633]
  Placement = pos=(0,0,-87) rot=(0,0,1;0.392699rad)
FEATURE [Part::Cut] Cut505
  Base = -> Tube038
  Tool = -> Compound885
FEATURE [Part::Cut] Cut506
  Base = -> Cut505
  Tool = -> Compound886
FEATURE [Part::FeaturePython] Tube060  # WARN: FeaturePython — macro-defined, semantics opaque (R4)
  AttacherType = Attacher::AttachEngine3D
  Height = 9
  InnerRadius = 31
  OuterRadius = 36
  Placement = pos=(0,0,-99) rot=(0,0,1;0rad)
FEATURE [Part::Chamfer] Chamfer019
  Base = -> Tube060
  Edges = 1 edges r=1: [Edge4]
FEATURE [Part::FeaturePython] Tube061  # WARN: FeaturePython — macro-defined, semantics opaque (R4)
  AttacherType = Attacher::AttachEngine3D
  Height = 1
  InnerRadius = 26
  OuterRadius = 36
  Placement = pos=(0,0,-98) rot=(0,0,1;0rad)
FEATURE [Part::Compound] Compound663  label="J-max_undermotor-undercover"
  Links = -> [Chamfer019,Tube061,Cut506]
FEATURE [Part::FeaturePython] Tube040  # WARN: FeaturePython — macro-defined, semantics opaque (R4)
  AttacherType = Attacher::AttachEngine3D
  Height = 3
  InnerRadius = 42
  OuterRadius = 52
  Placement = pos=(0,0,-11) rot=(0,0,1;0rad)
FEATURE [Part::Cylinder] Cylinder652  label="Válec652"
  Angle = 360
  AttacherType = Attacher::AttachEngine3D
  Height = 20
  Placement = pos=(-31.8198,-31.8198,-18) rot=(0,0,1;2.35619rad)
  Radius = 1.5
FEATURE [Part::Cylinder] Cylinder653  label="Válec653"
  Angle = 360
  AttacherType = Attacher::AttachEngine3D
  Height = 20
  Placement = pos=(0,45,-18) rot=(0,0,1;0rad)
  Radius = 1.5
FEATURE [Part::Cylinder] Cylinder654  label="Válec654"
  Angle = 360
  AttacherType = Attacher::AttachEngine3D
  Height = 20
  Placement = pos=(45,1.9e-14,-18) rot=(0,0,-1;1.5708rad)
  Radius = 1.5
FEATURE [Part::Cylinder] Cylinder655  label="Válec655"
  Angle = 360
  AttacherType = Attacher::AttachEngine3D
  Height = 20
  Placement = pos=(1.4e-14,-45,-18) rot=(0,0,1;3.14159rad)
  Radius = 1.5
FEATURE [Part::Cylinder] Cylinder656  label="Válec656"
  Angle = 360
  AttacherType = Attacher::AttachEngine3D
  Height = 20
  Placement = pos=(31.8198,31.8198,-18) rot=(0,0,-1;0.785398rad)
  Radius = 1.5
FEATURE [Part::Cylinder] Cylinder657  label="Válec657"
  Angle = 360
  AttacherType = Attacher::AttachEngine3D
  Height = 20
  Placement = pos=(31.8198,-31.8198,-18) rot=(0,0,1;3.92699rad)
  Radius = 1.5
FEATURE [Part::Cylinder] Cylinder658  label="Válec658"
  Angle = 360
  AttacherType = Attacher::AttachEngine3D
  Height = 20
  Placement = pos=(-31.8198,31.8198,-18) rot=(0,0,1;0.785398rad)
  Radius = 1.5
FEATURE [Part::Cylinder] Cylinder659  label="Válec659"
  Angle = 360
  AttacherType = Attacher::AttachEngine3D
  Height = 20
  Placement = pos=(-45,-6e-15,-18) rot=(0,0,1;1.5708rad)
  Radius = 1.5
FEATURE [Part::Compound] Compound660
  Links = -> [Cylinder653,Cylinder658,Cylinder659,Cylinder652,Cylinder655,Cylinder657,Cylinder654,Cylinder656]
  Placement = pos=(0,0,0) rot=(0,0,1;0.392699rad)
FEATURE [Part::Cut] Cut507  label="J-max_motor-high-washer_A1"
  Base = -> Tube040
  Placement = pos=(0,0,-4) rot=(0,0,1;0rad)
  Tool = -> Compound660
FEATURE [Part::Chamfer] Chamfer018  label="J-max_encoder-belt-ring-A"
  Base = -> Cut507
  Edges = 1 edges r=1: [Edge3]
  Placement = pos=(0,0,-2) rot=(0,0,1;0rad)
FEATURE [Part::Box] Box306  label="Krychle306"
  AttacherType = Attacher::AttachEngine3D
  Height = 7
  Length = 60
  Placement = pos=(-59.9909,-1.04714,-22) rot=(0,0,1;0.017453rad)
  Width = 60
FEATURE [Part::Box] Box305  label="Krychle305"
  AttacherType = Attacher::AttachEngine3D
  Height = 7
  Length = 60
  Placement = pos=(0,0,-22) rot=(0,0,-1;0.034907rad)
  Width = 60
FEATURE [Part::Box] Box304  label="Krychle304"
  AttacherType = Attacher::AttachEngine3D
  Height = 7
  Length = 120
  Placement = pos=(-60,-60,-22) rot=(0,0,-1;0rad)
  Width = 60
FEATURE [Part::Cylinder] Cylinder697  label="Válec697"
  Angle = 360
  AttacherType = Attacher::AttachEngine3D
  Height = 20
  Placement = pos=(0,45,-18) rot=(0,0,1;0rad)
  Radius = 1.5
FEATURE [Part::Cylinder] Cylinder696  label="Válec696"
  Angle = 360
  AttacherType = Attacher::AttachEngine3D
  Height = 20
  Placement = pos=(31.8198,-31.8198,-18) rot=(0,0,1;3.92699rad)
  Radius = 1.5
FEATURE [Part::Cylinder] Cylinder695  label="Válec695"
  Angle = 360
  AttacherType = Attacher::AttachEngine3D
  Height = 20
  Placement = pos=(31.8198,31.8198,-18) rot=(0,0,-1;0.785398rad)
  Radius = 1.5
FEATURE [Part::Cylinder] Cylinder694  label="Válec694"
  Angle = 360
  AttacherType = Attacher::AttachEngine3D
  Height = 20
  Placement = pos=(-31.8198,31.8198,-18) rot=(0,0,1;0.785398rad)
  Radius = 1.5
FEATURE [Part::Cylinder] Cylinder698  label="Válec698"
  Angle = 360
  AttacherType = Attacher::AttachEngine3D
  Height = 7
  Placement = pos=(0,0,-22) rot=(0,0,1;0rad)
  Radius = 44
FEATURE [Part::Box] Box307  label="Krychle307"
  AttacherType = Attacher::AttachEngine3D
  Height = 7
  Length = 1.4
  Placement = pos=(0,0,-22) rot=(0,0,1;0.34383rad)
  Width = 60
FEATURE [Part::Cylinder] Cylinder693  label="Válec693"
  Angle = 360
  AttacherType = Attacher::AttachEngine3D
  Height = 20
  Placement = pos=(45,1.9e-14,-18) rot=(0,0,-1;1.5708rad)
  Radius = 1.5
FEATURE [Part::Cylinder] Cylinder692  label="Válec692"
  Angle = 360
  AttacherType = Attacher::AttachEngine3D
  Height = 20
  Placement = pos=(1.4e-14,-45,-18) rot=(0,0,1;3.14159rad)
  Radius = 1.5
FEATURE [Part::Cylinder] Cylinder691  label="Válec691"
  Angle = 360
  AttacherType = Attacher::AttachEngine3D
  Height = 20
  Placement = pos=(-45,-6e-15,-18) rot=(0,0,1;1.5708rad)
  Radius = 1.5
FEATURE [Part::Cylinder] Cylinder690  label="Válec690"
  Angle = 360
  AttacherType = Attacher::AttachEngine3D
  Height = 20
  Placement = pos=(-31.8198,-31.8198,-18) rot=(0,0,1;2.35619rad)
  Radius = 1.5
FEATURE [Part::Cylinder] Cylinder689  label="Válec689"
  Angle = 360
  AttacherType = Attacher::AttachEngine3D
  Height = 7
  Placement = pos=(0,0,-22) rot=(0,0,1;0rad)
  Radius = 44
FEATURE [Part::Box] Box302  label="Krychle302"
  AttacherType = Attacher::AttachEngine3D
  Height = 7
  Length = 1.4
  Placement = pos=(0,0,-22) rot=(0,0,1;0.047124rad)
  Width = 60
FEATURE [Part::Box] Box301  label="Krychle301"
  AttacherType = Attacher::AttachEngine3D
  Height = 7
  Length = 1.4
  Placement = pos=(0,0,-22) rot=(0,0,-1;0.034907rad)
  Width = 60
FEATURE [Part::Box] Box300  label="Krychle300"
  AttacherType = Attacher::AttachEngine3D
  Height = 7
  Length = 120
  Placement = pos=(-60,-60,-22) rot=(0,0,-1;0rad)
  Width = 60
FEATURE [Part::Box] Box298  label="Krychle298"
  AttacherType = Attacher::AttachEngine3D
  Height = 7
  Length = 60
  Placement = pos=(0,0,-22) rot=(0,0,-1;0.349066rad)
  Width = 60
FEATURE [Part::Box] Box299  label="Krychle299"
  AttacherType = Attacher::AttachEngine3D
  Height = 7
  Length = 60
  Placement = pos=(-56.3816,-20.5212,-22) rot=(0,0,1;0.349066rad)
  Width = 60
FEATURE [Part::Box] Box308  label="Krychle308"
  AttacherType = Attacher::AttachEngine3D
  Height = 7
  Length = 1.4
  Placement = pos=(0,0,-22) rot=(0,0,-1;0.314159rad)
  Width = 60
FEATURE [Part::Cylinder] Cylinder699  label="Válec699"
  Angle = 360
  AttacherType = Attacher::AttachEngine3D
  Height = 7
  Placement = pos=(0,0,-29) rot=(0,0,1;0rad)
  Radius = 48
FEATURE [Part::FeaturePython] Tube071  # WARN: FeaturePython — macro-defined, semantics opaque (R4)
  AttacherType = Attacher::AttachEngine3D
  Height = 7
  InnerRadius = 44
  OuterRadius = 45.4
  Placement = pos=(0,0,-22) rot=(0,0,1;0rad)
FEATURE [Part::FeaturePython] Tube072  # WARN: FeaturePython — macro-defined, semantics opaque (R4)
  AttacherType = Attacher::AttachEngine3D
  Height = 3
  InnerRadius = 49
  OuterRadius = 52
  Placement = pos=(0,0,-22) rot=(0,0,1;0rad)
FEATURE [Part::FeaturePython] Tube073  # WARN: FeaturePython — macro-defined, semantics opaque (R4)
  AttacherType = Attacher::AttachEngine3D
  Height = 10
  InnerRadius = 42
  OuterRadius = 49
  Placement = pos=(0,0,-22) rot=(0,0,1;0rad)
FEATURE [Part::FeaturePython] Tube074  # WARN: FeaturePython — macro-defined, semantics opaque (R4)
  AttacherType = Attacher::AttachEngine3D
  Height = 7
  InnerRadius = 44
  OuterRadius = 45.4
  Placement = pos=(0,0,-22) rot=(0,0,1;0rad)
FEATURE [Part::Compound] Compound694
  Links = -> [Box305,Box306]
FEATURE [Part::Chamfer] Chamfer022
  Base = -> Tube072
  Edges = 1 edges r=1: [Edge1]
  Placement = pos=(0,0,-10) rot=(0,0,1;0rad)
FEATURE [Part::Compound] Compound692
  Links = -> [Cylinder697,Cylinder694,Cylinder691,Cylinder690,Cylinder692,Cylinder696,Cylinder693,Cylinder695]
  Placement = pos=(0,0,-8) rot=(0,0,1;0.392699rad)
FEATURE [Part::Compound] Compound691
  Links = -> [Box301,Box302]
FEATURE [Part::Compound] Compound690
  Links = -> [Box298,Box299]
FEATURE [Part::Cut] Cut310
  Base = -> Compound691
  Placement = pos=(0,0,-7) rot=(0,0,1;0rad)
  Tool = -> Cylinder689
FEATURE [Part::Cut] Cut308
  Base = -> Tube071
  Tool = -> Box300
FEATURE [Part::Cut] Cut309
  Base = -> Cut308
  Placement = pos=(0,0,-7) rot=(0,0,1;0rad)
  Tool = -> Compound690
FEATURE [Part::Cut] Cut311
  Base = -> Tube073
  Placement = pos=(0,0,-10) rot=(0,0,1;0rad)
  Tool = -> Compound692
FEATURE [Part::Compound] Compound693  label="J-max_motor-high-washer_B001"
  Links = -> [Cut311,Chamfer022]
FEATURE [Part::Cut] Cut312
  Base = -> Tube074
  Tool = -> Box304
FEATURE [Part::Cut] Cut313
  Base = -> Cut312
  Placement = pos=(0,0,-7) rot=(0,0,1;0rad)
  Tool = -> Compound694
FEATURE [Part::Cut] Cut314
  Base = -> Cut309
  Tool = -> Cut313
FEATURE [Part::Cut] Cut315
  Base = -> Compound693
  Tool = -> Cut314
FEATURE [Part::Cut] Cut316  label="J-max_encoder-belt-ring-B-part"
  Base = -> Cut315
  Tool = -> Cut310
FEATURE [Part::Compound] Compound695
  Links = -> [Box308,Box307]
FEATURE [Part::Cut] Cut317
  Base = -> Compound695
  Placement = pos=(0,0,-7) rot=(0,0,1;0rad)
  Tool = -> Cylinder698
FEATURE [Part::Common] Common005
  Base = -> Cut317
  Tool = -> Cylinder699
FEATURE [Part::Cut] Cut508  label="J-max_encoder-belt-ring-B"
  Base = -> Cut316
  Tool = -> Common005
FEATURE [Part::FeaturePython] Tube067  # WARN: FeaturePython — macro-defined, semantics opaque (R4)
  AttacherType = Attacher::AttachEngine3D
  Height = 1
  InnerRadius = 7
  OuterRadius = 8
  Placement = pos=(12.5,-21.6506,2) rot=(0,0,1;2.0944rad)
FEATURE [Part::FeaturePython] Tube068  # WARN: FeaturePython — macro-defined, semantics opaque (R4)
  AttacherType = Attacher::AttachEngine3D
  Height = 1
  InnerRadius = 7
  OuterRadius = 8
  Placement = pos=(12.5,21.6506,2) rot=(0,0,1;4.18879rad)
FEATURE [Part::FeaturePython] Tube069  # WARN: FeaturePython — macro-defined, semantics opaque (R4)
  AttacherType = Attacher::AttachEngine3D
  Height = 1
  InnerRadius = 7
  OuterRadius = 8
  Placement = pos=(-25,0,2) rot=(0,0,1;0rad)
FEATURE [Part::FeaturePython] Tube070  # WARN: FeaturePython — macro-defined, semantics opaque (R4)
  AttacherType = Attacher::AttachEngine3D
  Height = 1
  InnerRadius = 7
  OuterRadius = 8
  Placement = pos=(0,0,2) rot=(0,0,1;4.18879rad)
FEATURE [Part::Compound] Compound685
  Links = -> [Tube069,Tube067,Tube068,Tube070]
FEATURE [Part::Cylinder] Cylinder679  label="Válec679"
  Angle = 360
  AttacherType = Attacher::AttachEngine3D
  Height = 6
  Placement = pos=(12.5,-21.65,2) rot=(0,0,1;2.0944rad)
  Radius = 8
FEATURE [Part::Cylinder] Cylinder680  label="Válec680"
  Angle = 360
  AttacherType = Attacher::AttachEngine3D
  Height = 20
  Placement = pos=(0,0,-100) rot=(0,0,1;0rad)
  Radius = 15
FEATURE [Part::Cylinder] Cylinder681  label="Válec681"
  Angle = 360
  AttacherType = Attacher::AttachEngine3D
  Height = 8
  Radius = 40
FEATURE [Part::Cylinder] Cylinder682  label="Válec682"
  Angle = 360
  AttacherType = Attacher::AttachEngine3D
  Height = 6
  Placement = pos=(-25,0,2) rot=(0,0,1;0rad)
  Radius = 8
FEATURE [Part::Cylinder] Cylinder683  label="Válec683"
  Angle = 360
  AttacherType = Attacher::AttachEngine3D
  Height = 60
  Placement = pos=(29,5,-6) rot=(0,0,1;0rad)
  Radius = 1.5
FEATURE [Part::Cylinder] Cylinder684  label="Válec684"
  Angle = 360
  AttacherType = Attacher::AttachEngine3D
  Height = 3
  Placement = pos=(29,-5,-6) rot=(0,0,1;0rad)
  Radius = 3
FEATURE [Part::Cylinder] Cylinder685  label="Válec685"
  Angle = 360
  AttacherType = Attacher::AttachEngine3D
  Height = 6
  Placement = pos=(12.5,21.65,2) rot=(0,0,1;4.18879rad)
  Radius = 8
FEATURE [Part::Compound] Compound678
  Links = -> [Cylinder682,Cylinder679,Cylinder685]
FEATURE [Part::Cylinder] Cylinder686  label="Válec686"
  Angle = 360
  AttacherType = Attacher::AttachEngine3D
  Height = 3
  Placement = pos=(29,5,-6) rot=(0,0,1;0rad)
  Radius = 3
FEATURE [Part::Compound] Compound679
  Links = -> [Cylinder686,Cylinder684]
  Placement = pos=(0,0,6) rot=(0,0,1;0rad)
FEATURE [Part::Compound] Compound681
  Links = -> [Cylinder686,Cylinder684]
  Placement = pos=(0,0,6) rot=(0,0,1;2.0944rad)
FEATURE [Part::Compound] Compound682
  Links = -> [Cylinder686,Cylinder684]
  Placement = pos=(0,0,6) rot=(0,0,1;4.18879rad)
FEATURE [Part::Cylinder] Cylinder687  label="Válec687"
  Angle = 360
  AttacherType = Attacher::AttachEngine3D
  Height = 6
  Placement = pos=(0,0,2) rot=(0,0,1;4.18879rad)
  Radius = 8
FEATURE [Part::Cylinder] Cylinder688  label="Válec688"
  Angle = 360
  AttacherType = Attacher::AttachEngine3D
  Height = 60
  Placement = pos=(29,-5,-6) rot=(0,0,1;0rad)
  Radius = 1.5
FEATURE [Part::Compound] Compound680
  Links = -> [Cylinder683,Cylinder688]
  Placement = pos=(0,0,0) rot=(0,0,1;2.0944rad)
FEATURE [Part::Compound] Compound684
  Links = -> [Cylinder683,Cylinder688]
FEATURE [Part::Cylinder] Cylinder642  label="Válec642"
  Angle = 360
  AttacherType = Attacher::AttachEngine3D
  Height = 8
  Placement = pos=(0,0,-9) rot=(0,0,1;0rad)
  Radius = 7.5
FEATURE [Part::Cylinder] Cylinder641  label="Válec641"
  Angle = 360
  AttacherType = Attacher::AttachEngine3D
  Height = 1
  Placement = pos=(0,0,-1) rot=(0,0,1;0rad)
  Radius = 10
FEATURE [Part::Cut] Cut305
  Base = -> Cylinder681
  Tool = -> Compound678
FEATURE [Part::Cut] Cut303
  Base = -> Cut305
  Tool = -> Cylinder680
FEATURE [Part::Compound] Compound687
  Links = -> [Compound681,Compound682,Compound679]
FEATURE [Part::Compound] Compound688
  Links = -> [Cylinder683,Cylinder688]
  Placement = pos=(0,0,0) rot=(0,0,1;4.18879rad)
FEATURE [Part::Compound] Compound686
  Links = -> [Compound680,Compound688,Compound684]
FEATURE [Part::Cut] Cut307
  Base = -> Cut303
  Tool = -> Compound686
FEATURE [Part::Cut] Cut306
  Base = -> Cut307
  Tool = -> Compound687
FEATURE [Part::Cut] Cut304
  Base = -> Cut306
  Tool = -> Cylinder687
FEATURE [Part::Compound] Compound683  label="J-max_quikovina001"
  Links = -> [Compound685,Cut304]
FEATURE [Part::Chamfer] Chamfer021
  Base = -> Cylinder642
  Edges = 1 edges r=1: [Edge3]
FEATURE [Part::Compound] Compound689  label="J-max_quikovina-fixo"
  Links = -> [Cylinder641,Chamfer021,Compound683]
  Placement = pos=(0,0,59) rot=(0,0,1;0rad)
FEATURE [Part::Box] Box294  label="Krychle294"
  AttacherType = Attacher::AttachEngine3D
  Height = 51
  Length = 50
  Placement = pos=(0,0,8) rot=(0,0,1;2.61799rad)
  Width = 100
FEATURE [Part::Cylinder] Cylinder669  label="Válec669"
  Angle = 360
  AttacherType = Attacher::AttachEngine3D
  Height = 6
  Placement = pos=(12.5,21.65,2) rot=(0,0,1;4.18879rad)
  Radius = 8
FEATURE [Part::Cylinder] Cylinder668  label="Válec668"
  Angle = 360
  AttacherType = Attacher::AttachEngine3D
  Height = 6
  Placement = pos=(12.5,-21.65,2) rot=(0,0,1;2.0944rad)
  Radius = 8
FEATURE [Part::Cylinder] Cylinder670  label="Válec670"
  Angle = 360
  AttacherType = Attacher::AttachEngine3D
  Height = 8
  Radius = 40
FEATURE [Part::Box] Box295  label="Krychle295"
  AttacherType = Attacher::AttachEngine3D
  Height = 51
  Length = 50
  Placement = pos=(0,0,8) rot=(0,0,1;4.18879rad)
  Width = 100
FEATURE [Part::Cylinder] Cylinder671  label="Válec671"
  Angle = 360
  AttacherType = Attacher::AttachEngine3D
  Height = 100
  Placement = pos=(29,5,-20) rot=(0,0,1;0rad)
  Radius = 1.48
FEATURE [Part::Cylinder] Cylinder672  label="Válec672"
  Angle = 360
  AttacherType = Attacher::AttachEngine3D
  Height = 100
  Placement = pos=(29,-5,-6) rot=(0,0,1;0rad)
  Radius = 1.45
FEATURE [Part::Cylinder] Cylinder673  label="Válec673"
  Angle = 360
  AttacherType = Attacher::AttachEngine3D
  Height = 6
  Placement = pos=(-25,0,2) rot=(0,0,1;0rad)
  Radius = 8
FEATURE [Part::Compound] Compound673
  Links = -> [Cylinder673,Cylinder668,Cylinder669]
FEATURE [Part::Box] Box296  label="Krychle296"
  AttacherType = Attacher::AttachEngine3D
  Height = 51
  Length = 50
  Placement = pos=(0,0,8) rot=(0,0,-1;0.872665rad)
  Width = 50
FEATURE [Part::Cylinder] Cylinder674  label="Válec674"
  Angle = 360
  AttacherType = Attacher::AttachEngine3D
  Height = 3
  Placement = pos=(29,5,-6) rot=(0,0,1;0rad)
  Radius = 3
FEATURE [Part::Cylinder] Cylinder675  label="Válec675"
  Angle = 360
  AttacherType = Attacher::AttachEngine3D
  Height = 3
  Placement = pos=(29,-5,-6) rot=(0,0,1;0rad)
  Radius = 3
FEATURE [Part::Compound] Compound667
  Links = -> [Cylinder674,Cylinder675]
  Placement = pos=(0,0,6) rot=(0,0,1;2.0944rad)
FEATURE [Part::Compound] Compound670
  Links = -> [Cylinder674,Cylinder675]
  Placement = pos=(0,0,6) rot=(0,0,1;0rad)
FEATURE [Part::Compound] Compound672
  Links = -> [Cylinder674,Cylinder675]
  Placement = pos=(0,0,6) rot=(0,0,1;4.18879rad)
FEATURE [Part::Compound] Compound669
  Links = -> [Compound667,Compound672,Compound670]
FEATURE [Part::Cylinder] Cylinder676  label="Válec676"
  Angle = 360
  AttacherType = Attacher::AttachEngine3D
  Height = 100
  Placement = pos=(29,5,-6) rot=(0,0,1;0rad)
  Radius = 1.45
FEATURE [Part::Compound] Compound671
  Links = -> [Cylinder676,Cylinder672]
  Placement = pos=(0,0,0) rot=(0,0,1;1.0472rad)
FEATURE [Part::Box] Box297  label="Krychle297"
  AttacherType = Attacher::AttachEngine3D
  Height = 51
  Length = 50
  Placement = pos=(0,0,8) rot=(0,0,1;1.39626rad)
  Width = 50
FEATURE [Part::Cylinder] Cylinder677  label="Válec677"
  Angle = 360
  AttacherType = Attacher::AttachEngine3D
  Height = 20
  Placement = pos=(0,0,-4) rot=(0,0,1;0rad)
  Radius = 15
FEATURE [Part::Cylinder] Cylinder678  label="Válec678"
  Angle = 360
  AttacherType = Attacher::AttachEngine3D
  Height = 100
  Placement = pos=(29,-5,-20) rot=(0,0,1;0rad)
  Radius = 1.48
FEATURE [Part::Compound] Compound666
  Links = -> [Cylinder671,Cylinder678]
FEATURE [Part::Compound] Compound674
  Links = -> [Cylinder671,Cylinder678]
  Placement = pos=(0,0,0) rot=(0,0,1;4.18879rad)
FEATURE [Part::Compound] Compound675
  Links = -> [Cylinder671,Cylinder678]
  Placement = pos=(0,0,0) rot=(0,0,1;2.0944rad)
FEATURE [Part::Compound] Compound668
  Links = -> [Compound675,Compound674,Compound666]
FEATURE [Part::FeaturePython] Tube062  # WARN: FeaturePython — macro-defined, semantics opaque (R4)
  AttacherType = Attacher::AttachEngine3D
  Height = 1
  InnerRadius = 7
  OuterRadius = 8
  Placement = pos=(-25,0,2) rot=(0,0,1;0rad)
FEATURE [Part::FeaturePython] Tube063  # WARN: FeaturePython — macro-defined, semantics opaque (R4)
  AttacherType = Attacher::AttachEngine3D
  Height = 1
  InnerRadius = 7
  OuterRadius = 8
  Placement = pos=(12.5,-21.6506,2) rot=(0,0,1;2.0944rad)
FEATURE [Part::FeaturePython] Tube064  # WARN: FeaturePython — macro-defined, semantics opaque (R4)
  AttacherType = Attacher::AttachEngine3D
  Height = 1
  InnerRadius = 7
  OuterRadius = 8
  Placement = pos=(12.5,21.6506,2) rot=(0,0,1;4.18879rad)
FEATURE [Part::Compound] Compound665
  Links = -> [Tube062,Tube063,Tube064]
FEATURE [Part::FeaturePython] Tube065  # WARN: FeaturePython — macro-defined, semantics opaque (R4)
  AttacherType = Attacher::AttachEngine3D
  Height = 51
  InnerRadius = 21
  OuterRadius = 35
  Placement = pos=(0,0,8) rot=(0,0,1;0rad)
FEATURE [Part::FeaturePython] Tube066  # WARN: FeaturePython — macro-defined, semantics opaque (R4)
  AttacherType = Attacher::AttachEngine3D
  Height = 8
  InnerRadius = 15
  OuterRadius = 17.55
  Placement = pos=(0,0,-9) rot=(0,0,1;0rad)
FEATURE [Part::FeaturePython] Tube049  # WARN: FeaturePython — macro-defined, semantics opaque (R4)
  AttacherType = Attacher::AttachEngine3D
  Height = 1
  InnerRadius = 15
  OuterRadius = 22
  Placement = pos=(0,0,-1) rot=(0,0,1;0rad)
FEATURE [Part::Compound] Compound676
  Links = -> [Tube066,Tube049]
  Placement = pos=(0,0,-50) rot=(0,0,1;0rad)
FEATURE [Part::Chamfer] Chamfer020
  Base = -> Compound676
  Edges = 1 edges r=1: [Edge3]
FEATURE [Part::Cut] Cut509
  Base = -> Cylinder670
  Tool = -> Compound673
FEATURE [Part::Cut] Cut510
  Base = -> Tube065
  Tool = -> Box295
FEATURE [Part::Cut] Cut511
  Base = -> Cut510
  Tool = -> Box294
FEATURE [Part::Cut] Cut295
  Base = -> Cut509
  Tool = -> Cylinder677
FEATURE [Part::Cut] Cut296
  Base = -> Cut511
  Tool = -> Box296
FEATURE [Part::Cut] Cut300
  Base = -> Cut295
  Tool = -> Compound668
FEATURE [Part::Cut] Cut299
  Base = -> Cut300
  Tool = -> Compound669
FEATURE [Part::Cut] Cut301
  Base = -> Cut296
  Tool = -> Box297
FEATURE [Part::Cut] Cut297
  Base = -> Cut301
  Placement = pos=(0,0,0) rot=(0,0,1;3.14159rad)
  Tool = -> Compound671
FEATURE [Part::Cut] Cut298
  Base = -> Cut301
  Placement = pos=(0,0,0) rot=(0,0,1;1.0472rad)
  Tool = -> Compound671
FEATURE [Part::Cut] Cut302
  Base = -> Cut301
  Placement = pos=(0,0,0) rot=(0,0,-1;1.0472rad)
  Tool = -> Compound671
FEATURE [Part::Compound] Compound664  label="J-max_pikovina-fixo1"
  Links = -> [Compound665,Cut299,Cut298,Cut297,Cut302]
  Placement = pos=(0,0,-50) rot=(0,0,1;0rad)
FEATURE [Part::Compound] Compound677  label="J-max-deep_pikovina-fixo"
  Links = -> [Chamfer020,Compound664]
FEATURE [Part::Box] Box394  label="Krychle394"
  AttacherType = Attacher::AttachEngine3D
  Height = 2
  Length = 6
  Placement = pos=(-22.6712,-46.8937,33) rot=(0,0,-1;0.392699rad)
  Width = 8
FEATURE [Part::Cylinder] Cylinder830  label="Válec830"
  Angle = 360
  AttacherType = Attacher::AttachEngine3D
  Height = 20
  Placement = pos=(-52.3,0,34) rot=(0,0,1;0rad)
  Radius = 3.5
FEATURE [Part::Cylinder] Cylinder831  label="Válec831"
  Angle = 360
  AttacherType = Attacher::AttachEngine3D
  Height = 32
  Placement = pos=(44.3462,-18.3688,35.5) rot=(0,0,1;1.1781rad)
  Radius = 1.5
FEATURE [Part::Cylinder] Cylinder832  label="Válec832"
  Angle = 360
  AttacherType = Attacher::AttachEngine3D
  Height = 32
  Placement = pos=(44.3462,18.3688,35.5) rot=(0,0,1;1.96349rad)
  Radius = 1.5
FEATURE [Part::Cylinder] Cylinder833  label="Válec833"
  Angle = 360
  AttacherType = Attacher::AttachEngine3D
  Height = 32
  Placement = pos=(18.3688,-44.3462,35.5) rot=(0,0,1;0.392699rad)
  Radius = 1.5
FEATURE [Part::Cylinder] Cylinder834  label="Válec834"
  Angle = 360
  AttacherType = Attacher::AttachEngine3D
  Height = 12
  Radius = 42
FEATURE [Part::Cylinder] Cylinder835  label="Válec835"
  Angle = 360
  AttacherType = Attacher::AttachEngine3D
  Height = 12
  Radius = 42
FEATURE [Part::Cylinder] Cylinder836  label="Válec836"
  Angle = 360
  AttacherType = Attacher::AttachEngine3D
  Height = 32
  Placement = pos=(-44.3462,-18.3688,35.5) rot=(0,0,-1;1.1781rad)
  Radius = 1.5
FEATURE [Part::Box] Box390  label="Krychle390"
  AttacherType = Attacher::AttachEngine3D
  Height = 2
  Length = 6
  Placement = pos=(-17.1279,49.1898,33) rot=(0,0,1;3.53429rad)
  Width = 8
FEATURE [Part::Box] Box391  label="Krychle391"
  AttacherType = Attacher::AttachEngine3D
  Height = 2
  Length = 6
  Placement = pos=(22.6712,46.8937,33) rot=(0,0,1;2.74889rad)
  Width = 8
FEATURE [Part::Box] Box392  label="Krychle392"
  AttacherType = Attacher::AttachEngine3D
  Height = 2
  Length = 6
  Placement = pos=(46.8937,-22.6712,33) rot=(0,0,1;1.1781rad)
  Width = 8
FEATURE [Part::Cylinder] Cylinder837  label="Válec837"
  Angle = 360
  AttacherType = Attacher::AttachEngine3D
  Height = 32
  Placement = pos=(-18.3688,-44.3462,35.5) rot=(0,0,-1;0.392699rad)
  Radius = 1.5
FEATURE [Part::Box] Box393  label="Krychle393"
  AttacherType = Attacher::AttachEngine3D
  Height = 2
  Length = 6
  Placement = pos=(17.1279,-49.1898,33) rot=(0,0,1;0.392699rad)
  Width = 8
FEATURE [Part::Cylinder] Cylinder838  label="Válec838"
  Angle = 360
  AttacherType = Attacher::AttachEngine3D
  Height = 20
  Placement = pos=(-52.3,0,34) rot=(0,0,1;0rad)
  Radius = 3.5
FEATURE [Part::Cylinder] Cylinder839  label="Válec839"
  Angle = 360
  AttacherType = Attacher::AttachEngine3D
  Height = 32
  Placement = pos=(-44.3462,18.3688,35.5) rot=(0,0,-1;1.9635rad)
  Radius = 1.5
FEATURE [Part::Cylinder] Cylinder840  label="Válec840"
  Angle = 360
  AttacherType = Attacher::AttachEngine3D
  Height = 32
  Placement = pos=(-44.3462,18.3688,35.5) rot=(0,0,-1;1.9635rad)
  Radius = 1.5
FEATURE [Part::Cylinder] Cylinder841  label="Válec841"
  Angle = 360
  AttacherType = Attacher::AttachEngine3D
  Height = 32
  Placement = pos=(18.3688,44.3462,35.5) rot=(0,0,1;2.74889rad)
  Radius = 1.5
FEATURE [Part::Cylinder] Cylinder842  label="Válec842"
  Angle = 360
  AttacherType = Attacher::AttachEngine3D
  Height = 32
  Placement = pos=(18.3688,44.3462,35.5) rot=(0,0,1;2.74889rad)
  Radius = 1.5
FEATURE [Part::Cylinder] Cylinder843  label="Válec843"
  Angle = 360
  AttacherType = Attacher::AttachEngine3D
  Height = 32
  Placement = pos=(-18.3688,44.3462,35.5) rot=(0,0,1;3.53429rad)
  Radius = 1.5
FEATURE [Part::Compound] Compound752
  Links = -> [Cylinder833,Cylinder831,Cylinder832,Cylinder842,Cylinder843,Cylinder840,Cylinder836,Cylinder837]
  Placement = pos=(0,0,2) rot=(0,0,1;0rad)
FEATURE [Part::Box] Box395  label="Krychle395"
  AttacherType = Attacher::AttachEngine3D
  Height = 2
  Length = 6
  Placement = pos=(49.1898,17.1279,33) rot=(0,0,1;1.96349rad)
  Width = 8
FEATURE [Part::Cylinder] Cylinder844  label="Válec844"
  Angle = 360
  AttacherType = Attacher::AttachEngine3D
  Height = 32
  Placement = pos=(44.3462,-18.3688,35.5) rot=(0,0,1;1.1781rad)
  Radius = 1.5
FEATURE [Part::Cylinder] Cylinder845  label="Válec845"
  Angle = 360
  AttacherType = Attacher::AttachEngine3D
  Height = 32
  Placement = pos=(44.3462,18.3688,35.5) rot=(0,0,1;1.96349rad)
  Radius = 1.5
FEATURE [Part::Box] Box396  label="Krychle396"
  AttacherType = Attacher::AttachEngine3D
  Height = 2
  Length = 6
  Placement = pos=(-49.1898,-17.1279,33) rot=(0,0,-1;1.1781rad)
  Width = 8
FEATURE [Part::Box] Box397  label="Krychle397"
  AttacherType = Attacher::AttachEngine3D
  Height = 2
  Length = 6
  Placement = pos=(-46.8937,22.6712,33) rot=(0,0,-1;1.9635rad)
  Width = 8
FEATURE [Part::Compound] Compound751
  Links = -> [Box393,Box395,Box391,Box390,Box397,Box396,Box394,Box392]
  Placement = pos=(0,0,7) rot=(0,0,1;0rad)
FEATURE [Part::Cylinder] Cylinder846  label="Válec846"
  Angle = 360
  AttacherType = Attacher::AttachEngine3D
  Height = 32
  Placement = pos=(18.3688,-44.3462,35.5) rot=(0,0,1;0.392699rad)
  Radius = 1.5
FEATURE [Part::Cylinder] Cylinder847  label="Válec847"
  Angle = 360
  AttacherType = Attacher::AttachEngine3D
  Height = 32
  Placement = pos=(-18.3688,44.3462,35.5) rot=(0,0,1;3.53429rad)
  Radius = 1.5
FEATURE [Part::Cylinder] Cylinder848  label="Válec848"
  Angle = 360
  AttacherType = Attacher::AttachEngine3D
  Height = 32
  Placement = pos=(-18.3688,-44.3462,35.5) rot=(0,0,-1;0.392699rad)
  Radius = 1.5
FEATURE [Part::Cylinder] Cylinder849  label="Válec849"
  Angle = 360
  AttacherType = Attacher::AttachEngine3D
  Height = 32
  Placement = pos=(-44.3462,-18.3688,35.5) rot=(0,0,-1;1.1781rad)
  Radius = 1.5
FEATURE [Part::Compound] Compound753
  Links = -> [Cylinder846,Cylinder844,Cylinder845,Cylinder841,Cylinder847,Cylinder839,Cylinder849,Cylinder848]
FEATURE [Part::FeaturePython] wormgear042  # WARN: FeaturePython — macro-defined, semantics opaque (R4)
  AttacherType = Attacher::AttachEngine3D
  Placement = pos=(0,0,0) rot=(0,0,1;0.10472rad)
  beta = 39.6569
  clearance = 0.25
  diameter = 76
  head = 0
  height = 14
  module = 1.5
  pressure_angle = 20
  reverse_pitch = true
  teeth = 42
  version = 0.0.3
FEATURE [Part::FeaturePython] Tube079  # WARN: FeaturePython — macro-defined, semantics opaque (R4)
  AttacherType = Attacher::AttachEngine3D
  Height = 24
  InnerRadius = 40
  OuterRadius = 52
  Placement = pos=(0,0,21) rot=(0,0,1;0rad)
FEATURE [Part::FeaturePython] wormgear043  # WARN: FeaturePython — macro-defined, semantics opaque (R4)
  AttacherType = Attacher::AttachEngine3D
  Placement = pos=(0,0,0) rot=(0,0,-1;0.179769rad)
  beta = 39.6569
  clearance = 0.25
  diameter = 76
  head = 0
  height = 14
  module = 1.5
  pressure_angle = 20
  reverse_pitch = false
  teeth = 42
  version = 0.0.3
FEATURE [Part::FeaturePython] Tube080  # WARN: FeaturePython — macro-defined, semantics opaque (R4)
  AttacherType = Attacher::AttachEngine3D
  Height = 1
  InnerRadius = 42
  OuterRadius = 52
  Placement = pos=(0,0,37) rot=(0,0,1;0rad)
FEATURE [Part::Cut] Cut379
  Base = -> Cylinder835
  Placement = pos=(0,0,21) rot=(0,0,1;0.191986rad)
  Tool = -> wormgear043
FEATURE [Part::Torus] Torus007  label="Anuloid007"
  Angle1 = -180
  Angle2 = 180
  Angle3 = 360
  AttacherType = Attacher::AttachEngine3D
  Placement = pos=(0,0,34) rot=(0,0,1;0rad)
  Radius1 = 52
  Radius2 = 3.1
FEATURE [Part::Cut] Cut380
  Base = -> Tube079
  Tool = -> Torus007
FEATURE [Part::Cut] Cut382
  Base = -> Cut380
  Tool = -> Cylinder830
FEATURE [Part::Cut] Cut381
  Base = -> Cut382
  Tool = -> Compound752
FEATURE [Part::Cut] Cut383  label="J-max_rybovina007"
  Base = -> Cut381
  Tool = -> Compound751
FEATURE [Part::Cut] Cut384
  Base = -> Cylinder834
  Placement = pos=(0,0,33) rot=(0,0,1;0.287979rad)
  Tool = -> wormgear042
FEATURE [Part::Cut] Cut385
  Base = -> Tube080
  Tool = -> Compound753
FEATURE [Part::Cut] Cut386
  Base = -> Cut385
  Placement = pos=(0,0,8) rot=(0,0,1;0rad)
  Tool = -> Cylinder838
FEATURE [Part::Compound] Compound750  label="J-max_rybovina006"
  Links = -> [Cut379,Cut384,Cut383]
FEATURE [Part::Compound] Compound754  label="J-max-deep_actuator-ring-m1.5"
  Links = -> [Compound750,Cut386]
  Placement = pos=(0,0,-2) rot=(0,0,1;0rad)
FEATURE [Mesh::Feature] Mesh006  label="J-max_encoder-belt-ring-A (Meshed)"
FEATURE [Mesh::Feature] Mesh007  label="J-max_encoder-belt-ring-B (Meshed)"
FEATURE [Mesh::Feature] Mesh008  label="J-max_undermotor-undercover (Meshed)"
FEATURE [Mesh::Feature] Mesh009  label="J-max_undermotor-cover (Meshed)"
FEATURE [Mesh::Feature] Mesh012  label="J-max-deep_pikovina-fixo (Meshed)"
FEATURE [Mesh::Feature] Mesh013  label="J-max_quikovina-fixo (Meshed)"
FEATURE [Part::Cylinder] Cylinder972  label="Válec972"
  Angle = 360
  AttacherType = Attacher::AttachEngine3D
  Height = 20
  Placement = pos=(-4.5,-4.5,-88) rot=(0,0,1;0rad)
  Radius = 1
FEATURE [Part::Cylinder] Cylinder971  label="Válec971"
  Angle = 360
  AttacherType = Attacher::AttachEngine3D
  Height = 20
  Placement = pos=(4.5,4.5,-88) rot=(0,0,1;3.14159rad)
  Radius = 1
FEATURE [Part::Cylinder] Cylinder965  label="Válec965"
  Angle = 360
  AttacherType = Attacher::AttachEngine3D
  Height = 20
  Placement = pos=(-4.5,4.5,-88) rot=(0,0,-1;1.5708rad)
  Radius = 1
FEATURE [Part::Cylinder] Cylinder969  label="Válec969"
  Angle = 360
  AttacherType = Attacher::AttachEngine3D
  Height = 2
  Placement = pos=(-4.5,4.5,-88) rot=(0,0,-1;1.5708rad)
  Radius = 2
FEATURE [Part::Cylinder] Cylinder975  label="Válec975"
  Angle = 360
  AttacherType = Attacher::AttachEngine3D
  Height = 2
  Placement = pos=(4.5,-4.5,-88) rot=(0,0,1;1.5708rad)
  Radius = 2
FEATURE [Part::Cylinder] Cylinder970  label="Válec970"
  Angle = 360
  AttacherType = Attacher::AttachEngine3D
  Height = 20
  Placement = pos=(4.5,-4.5,-88) rot=(0,0,1;1.5708rad)
  Radius = 1
FEATURE [Part::Compound] Compound808
  Links = -> [Cylinder972,Cylinder970,Cylinder971,Cylinder965]
  Placement = pos=(0,0,91) rot=(0,0,1;0rad)
FEATURE [Part::Cylinder] Cylinder974  label="Válec974"
  Angle = 360
  AttacherType = Attacher::AttachEngine3D
  Height = 2
  Placement = pos=(4.5,4.5,-88) rot=(0,0,1;3.14159rad)
  Radius = 2
FEATURE [Part::Cylinder] Cylinder977  label="Válec977"
  Angle = 360
  AttacherType = Attacher::AttachEngine3D
  Height = 20
  Placement = pos=(4.5,4.5,-88) rot=(0,0,1;3.14159rad)
  Radius = 1
FEATURE [Part::Cylinder] Cylinder973  label="Válec973"
  Angle = 360
  AttacherType = Attacher::AttachEngine3D
  Height = 2
  Placement = pos=(-4.5,-4.5,-88) rot=(0,0,1;0rad)
  Radius = 2
FEATURE [Part::Compound] Compound798
  Links = -> [Cylinder973,Cylinder975,Cylinder974,Cylinder969]
  Placement = pos=(0,0,91) rot=(0,0,1;0rad)
FEATURE [Part::Cylinder] Cylinder978  label="Válec978"
  Angle = 360
  AttacherType = Attacher::AttachEngine3D
  Height = 4
  Placement = pos=(0,0,15) rot=(0,0,1;0rad)
  Radius = 9
FEATURE [Part::Cylinder] Cylinder979  label="Válec979"
  Angle = 360
  AttacherType = Attacher::AttachEngine3D
  Height = 20
  Placement = pos=(-4.5,-4.5,-88) rot=(0,0,1;0rad)
  Radius = 1
FEATURE [Part::Cylinder] Cylinder976  label="Válec976"
  Angle = 360
  AttacherType = Attacher::AttachEngine3D
  Height = 20
  Placement = pos=(-4.5,4.5,-88) rot=(0,0,-1;1.5708rad)
  Radius = 1
FEATURE [Part::Cylinder] Cylinder980  label="Válec980"
  Angle = 360
  AttacherType = Attacher::AttachEngine3D
  Height = 20
  Placement = pos=(4.5,-4.5,-88) rot=(0,0,1;1.5708rad)
  Radius = 1
FEATURE [Part::Compound] Compound809
  Links = -> [Cylinder979,Cylinder980,Cylinder977,Cylinder976]
  Placement = pos=(0,0,91) rot=(0,0,1;0rad)
FEATURE [Part::Cylinder] Cylinder981  label="Válec981"
  Angle = 360
  AttacherType = Attacher::AttachEngine3D
  Height = 50
  Placement = pos=(0,0,-4) rot=(0,0,1;0rad)
  Radius = 2.8
FEATURE [Part::Cylinder] Cylinder983  label="Válec983"
  Angle = 360
  AttacherType = Attacher::AttachEngine3D
  Height = 20
  Placement = pos=(4.5,-4.5,-88) rot=(0,0,1;1.5708rad)
  Radius = 1
FEATURE [Part::Cylinder] Cylinder984  label="Válec984"
  Angle = 360
  AttacherType = Attacher::AttachEngine3D
  Height = 20
  Placement = pos=(4.5,4.5,-88) rot=(0,0,1;3.14159rad)
  Radius = 1
FEATURE [Part::Cylinder] Cylinder985  label="Válec985"
  Angle = 360
  AttacherType = Attacher::AttachEngine3D
  Height = 20
  Placement = pos=(-4.5,-4.5,-88) rot=(0,0,1;0rad)
  Radius = 1
FEATURE [Part::Cylinder] Cylinder982  label="Válec982"
  Angle = 360
  AttacherType = Attacher::AttachEngine3D
  Height = 20
  Placement = pos=(-4.5,4.5,-88) rot=(0,0,-1;1.5708rad)
  Radius = 1
FEATURE [Part::Compound] Compound810
  Links = -> [Cylinder985,Cylinder983,Cylinder984,Cylinder982]
  Placement = pos=(0,0,91) rot=(0,0,1;0rad)
FEATURE [Part::FeaturePython] Tube092  # WARN: FeaturePython — macro-defined, semantics opaque (R4)
  AttacherType = Attacher::AttachEngine3D
  Height = 10
  InnerRadius = 2.8
  OuterRadius = 9
  Placement = pos=(0,0,19) rot=(0,0,1;0rad)
FEATURE [Part::FeaturePython] Tube093  # WARN: FeaturePython — macro-defined, semantics opaque (R4)
  AttacherType = Attacher::AttachEngine3D
  Height = 12
  InnerRadius = 4.1
  OuterRadius = 9
  Placement = pos=(0,0,12) rot=(0,0,1;0rad)
FEATURE [Part::FeaturePython] wormgear047  # WARN: FeaturePython — macro-defined, semantics opaque (R4)
  AttacherType = Attacher::AttachEngine3D
  Placement = pos=(0,0,29) rot=(0,0,1;0.994838rad)
  beta = 44.3704
  clearance = 0.25
  diameter = 23
  head = 0.5
  height = 12
  module = 1.5
  pressure_angle = 20
  reverse_pitch = false
  teeth = 15
  version = 0.0.3
FEATURE [Part::Cut] Cut409
  Base = -> wormgear047
  Tool = -> Cylinder981
FEATURE [Part::Wedge] Wedge009  label="Klín009"
  AttacherType = Attacher::AttachEngine3D
  Placement = pos=(0,0,12) rot=(0,0,1;3.14159rad)
  X2max = 0
  X2min = 0
  Xmax = 10
  Xmin = -10
  Ymax = 0
  Ymin = -32
  Z2max = 12
  Z2min = 0
  Zmax = 12
  Zmin = 0
FEATURE [Part::Wedge] Wedge010  label="Klín010"
  AttacherType = Attacher::AttachEngine3D
  Placement = pos=(0,0,12) rot=(0,0,-1;1.5708rad)
  X2max = 0
  X2min = 0
  Xmax = 10
  Xmin = -10
  Ymax = 0
  Ymin = -32
  Z2max = 12
  Z2min = 0
  Zmax = 12
  Zmin = 0
FEATURE [Part::Wedge] Wedge011  label="Klín011"
  AttacherType = Attacher::AttachEngine3D
  Placement = pos=(0,0,12) rot=(0,0,1;0rad)
  X2max = 0
  X2min = 0
  Xmax = 10
  Xmin = -10
  Ymax = 0
  Ymin = -32
  Z2max = 12
  Z2min = 0
  Zmax = 12
  Zmin = 0
FEATURE [Part::Wedge] Wedge008  label="Klín008"
  AttacherType = Attacher::AttachEngine3D
  Placement = pos=(0,0,12) rot=(0,0,1;1.5708rad)
  X2max = 0
  X2min = 0
  Xmax = 10
  Xmin = -10
  Ymax = 0
  Ymin = -32
  Z2max = 12
  Z2min = 0
  Zmax = 12
  Zmin = 0
FEATURE [Part::Compound] Compound811
  Links = -> [Wedge011,Wedge008,Wedge009,Wedge010]
FEATURE [Part::Cut] Cut408
  Base = -> Tube093
  Placement = pos=(0,0,-9) rot=(0,0,1;0rad)
  Tool = -> Compound811
FEATURE [Part::Chamfer] Chamfer024
  Base = -> Cut408
  Edges = 8 edges r=1: [Edge7,Edge8,Edge21,Edge22,Edge31,Edge32,Edge45,Edge46]
FEATURE [Part::Cut] Cut410
  Base = -> Chamfer024
  Tool = -> Compound798
FEATURE [Part::Cut] Cut411
  Base = -> Cut410
  Tool = -> Compound810
FEATURE [Part::Cut] Cut412
  Base = -> Cylinder978
  Tool = -> Compound808
FEATURE [Part::Cut] Cut413
  Base = -> Tube092
  Tool = -> Compound809
FEATURE [Part::Compound] Compound781  label="J-max-deep_inner-planeo-reinforced-m1.5"
  Links = -> [Cut409,Cut411,Cut412,Cut413]
FEATURE [Mesh::Feature] Mesh014  label="J-max-deep_rybovina-m1.5_podlozena (Meshed)"
FEATURE [Part::Cylinder] Cylinder1414  label="Válec1414"
  Angle = 360
  AttacherType = Attacher::AttachEngine3D
  Height = 100
  Placement = pos=(0,0,-10) rot=(0,0,1;0rad)
  Radius = 2.75
FEATURE [Part::Cylinder] Cylinder1415  label="Válec1415"
  Angle = 360
  AttacherType = Attacher::AttachEngine3D
  Height = 100
  Placement = pos=(0,0,-10) rot=(0,0,1;0rad)
  Radius = 2.75
FEATURE [Part::Cylinder] Cylinder1416  label="Válec1416"
  Angle = 360
  AttacherType = Attacher::AttachEngine3D
  Height = 100
  Placement = pos=(0,0,-10) rot=(0,0,1;0rad)
  Radius = 2.75
FEATURE [Part::Cylinder] Cylinder1417  label="Válec1417"
  Angle = 360
  AttacherType = Attacher::AttachEngine3D
  Height = 50
  Placement = pos=(0,0,-10) rot=(0,0,1;0rad)
  Radius = 2.75
FEATURE [Part::FeaturePython] wormgear064  # WARN: FeaturePython — macro-defined, semantics opaque (R4)
  AttacherType = Attacher::AttachEngine3D
  Placement = pos=(0,0,24) rot=(0,0,1;0.261799rad)
  beta = 43.6678
  clearance = 0.25
  diameter = 22
  head = 0
  height = 13
  module = 1.5
  pressure_angle = 20
  reverse_pitch = false
  teeth = 14
  version = 0.0.3
FEATURE [Part::FeaturePython] wormgear065  # WARN: FeaturePython — macro-defined, semantics opaque (R4)
  AttacherType = Attacher::AttachEngine3D
  Placement = pos=(0,0,12) rot=(0,0,1;0.551524rad)
  beta = 42.7094
  clearance = 0.2
  diameter = 26
  head = 0
  height = 12
  module = 1.5
  pressure_angle = 25
  reverse_pitch = true
  teeth = 16
  version = 0.0.3
FEATURE [Part::FeaturePython] wormgear066  # WARN: FeaturePython — macro-defined, semantics opaque (R4)
  AttacherType = Attacher::AttachEngine3D
  Placement = pos=(0,0,0) rot=(0,0,1;0.336849rad)
  beta = 42.7094
  clearance = 0.2
  diameter = 26
  head = 0
  height = 12
  module = 1.5
  pressure_angle = 25
  reverse_pitch = false
  teeth = 16
  version = 0.0.3
FEATURE [Part::FeaturePython] wormgear067  # WARN: FeaturePython — macro-defined, semantics opaque (R4)
  AttacherType = Attacher::AttachEngine3D
  Placement = pos=(0,0,37) rot=(0,0,1;0.604757rad)
  beta = 43.6678
  clearance = 0.25
  diameter = 22
  head = 0
  height = 12
  module = 1.5
  pressure_angle = 20
  reverse_pitch = true
  teeth = 14
  version = 0.0.3
FEATURE [Part::Cut] Cut512
  Base = -> wormgear066
  Tool = -> Cylinder1414
FEATURE [Part::Cut] Cut513
  Base = -> wormgear065
  Tool = -> Cylinder1415
FEATURE [Part::Cut] Cut514
  Base = -> wormgear064
  Tool = -> Cylinder1417
FEATURE [Part::Cut] Cut515
  Base = -> wormgear067
  Tool = -> Cylinder1416
FEATURE [Part::Compound] Compound887  label="J-max-deep_outer-planeo_thin-version"
  Links = -> [Cut512,Cut515,Cut513,Cut514]
  Placement = pos=(0,-25,-6) rot=(0,0,1;0.122173rad)
FEATURE [Mesh::Feature] Mesh015  label="J-max-deep_outer-planeo_thin-version (Meshed)"
FEATURE [Part::FeaturePython] wormgear068  # WARN: FeaturePython — macro-defined, semantics opaque (R4)
  AttacherType = Attacher::AttachEngine3D
  Placement = pos=(0,0,24) rot=(0,0,1;0.261799rad)
  beta = 43.6678
  clearance = 0.25
  diameter = 22
  head = 0
  height = 13
  module = 1.5
  pressure_angle = 20
  reverse_pitch = false
  teeth = 14
  version = 0.0.3
FEATURE [Part::FeaturePython] wormgear069  # WARN: FeaturePython — macro-defined, semantics opaque (R4)
  AttacherType = Attacher::AttachEngine3D
  Placement = pos=(0,0,37) rot=(0,0,1;0.604757rad)
  beta = 43.6678
  clearance = 0.25
  diameter = 22
  head = 0
  height = 12
  module = 1.5
  pressure_angle = 20
  reverse_pitch = true
  teeth = 14
  version = 0.0.3
FEATURE [Part::FeaturePython] wormgear070  # WARN: FeaturePython — macro-defined, semantics opaque (R4)
  AttacherType = Attacher::AttachEngine3D
  Placement = pos=(0,0,12) rot=(0,0,1;0.551524rad)
  beta = 42.4906
  clearance = 0.2
  diameter = 26.2
  head = 0
  height = 12
  module = 1.5
  pressure_angle = 25
  reverse_pitch = true
  teeth = 16
  version = 0.0.3
FEATURE [Part::FeaturePython] wormgear071  # WARN: FeaturePython — macro-defined, semantics opaque (R4)
  AttacherType = Attacher::AttachEngine3D
  Placement = pos=(0,0,0) rot=(0,0,1;0.336849rad)
  beta = 42.4906
  clearance = 0.2
  diameter = 26.2
  head = 0
  height = 12
  module = 1.5
  pressure_angle = 25
  reverse_pitch = false
  teeth = 16
  version = 0.0.3
FEATURE [Part::Cylinder] Cylinder1418  label="Válec1418"
  Angle = 360
  AttacherType = Attacher::AttachEngine3D
  Height = 100
  Placement = pos=(0,0,-10) rot=(0,0,1;0rad)
  Radius = 2.65
FEATURE [Part::Cut] Cut519
  Base = -> wormgear070
  Tool = -> Cylinder1418
FEATURE [Part::Cylinder] Cylinder1419  label="Válec1419"
  Angle = 360
  AttacherType = Attacher::AttachEngine3D
  Height = 100
  Placement = pos=(0,0,-10) rot=(0,0,1;0rad)
  Radius = 2.65
FEATURE [Part::Cut] Cut516
  Base = -> wormgear069
  Tool = -> Cylinder1419
FEATURE [Part::Cylinder] Cylinder1420  label="Válec1420"
  Angle = 360
  AttacherType = Attacher::AttachEngine3D
  Height = 50
  Placement = pos=(0,0,-10) rot=(0,0,1;0rad)
  Radius = 2.65
FEATURE [Part::Cut] Cut518
  Base = -> wormgear068
  Tool = -> Cylinder1420
FEATURE [Part::Cylinder] Cylinder1421  label="Válec1421"
  Angle = 360
  AttacherType = Attacher::AttachEngine3D
  Height = 100
  Placement = pos=(0,0,-10) rot=(0,0,1;0rad)
  Radius = 2.65
FEATURE [Part::Cut] Cut517
  Base = -> wormgear071
  Tool = -> Cylinder1421
FEATURE [Part::Compound] Compound888  label="J-max-deep_outer-planeo_semi-version"
  Links = -> [Cut517,Cut516,Cut519,Cut518]
  Placement = pos=(0,-25,-6) rot=(0,0,1;0.122173rad)
FEATURE [Part::FeaturePython] wormgear075  # WARN: FeaturePython — macro-defined, semantics opaque (R4)
  AttacherType = Attacher::AttachEngine3D
  Placement = pos=(0,0,24) rot=(0,0,1;0.261799rad)
  beta = 43.6678
  clearance = 0.25
  diameter = 22
  head = 0
  height = 13
  module = 1.5
  pressure_angle = 20
  reverse_pitch = false
  teeth = 14
  version = 0.0.3
FEATURE [Part::FeaturePython] wormgear074  # WARN: FeaturePython — macro-defined, semantics opaque (R4)
  AttacherType = Attacher::AttachEngine3D
  Placement = pos=(0,0,12) rot=(0,0,1;0.551524rad)
  beta = 42.4906
  clearance = 0.2
  diameter = 26.2
  head = 0
  height = 12
  module = 1.5
  pressure_angle = 25
  reverse_pitch = true
  teeth = 16
  version = 0.0.3
FEATURE [Part::FeaturePython] wormgear072  # WARN: FeaturePython — macro-defined, semantics opaque (R4)
  AttacherType = Attacher::AttachEngine3D
  Placement = pos=(0,0,0) rot=(0,0,1;0.336849rad)
  beta = 42.4906
  clearance = 0.2
  diameter = 26.2
  head = 0
  height = 12
  module = 1.5
  pressure_angle = 25
  reverse_pitch = false
  teeth = 16
  version = 0.0.3
FEATURE [Part::FeaturePython] wormgear073  # WARN: FeaturePython — macro-defined, semantics opaque (R4)
  AttacherType = Attacher::AttachEngine3D
  Placement = pos=(0,0,37) rot=(0,0,1;0.604757rad)
  beta = 43.6678
  clearance = 0.25
  diameter = 22
  head = 0
  height = 12
  module = 1.5
  pressure_angle = 20
  reverse_pitch = true
  teeth = 14
  version = 0.0.3
FEATURE [Part::Compound] Compound889
  Links = -> [wormgear072,wormgear073,wormgear074,wormgear075]
FEATURE [Part::Cylinder] Cylinder1422  label="Válec1422"
  Angle = 360
  AttacherType = Attacher::AttachEngine3D
  Height = 80
  Placement = pos=(0,0,-10) rot=(0,0,1;0rad)
  Radius = 2.7
FEATURE [Part::Cut] Cut520  label="J-max-deep_outer-planeo_prago-version"
  Base = -> Compound889
  Tool = -> Cylinder1422
FEATURE [Part::Cylinder] Cylinder1423  label="Válec1423"
  Angle = 360
  AttacherType = Attacher::AttachEngine3D
  Height = 80
  Placement = pos=(0,0,-10) rot=(0,0,1;0rad)
  Radius = 2.65
FEATURE [Part::FeaturePython] wormgear076  # WARN: FeaturePython — macro-defined, semantics opaque (R4)
  AttacherType = Attacher::AttachEngine3D
  Placement = pos=(0,0,12) rot=(0,0,1;0.551524rad)
  beta = 41.6335
  clearance = 0.2
  diameter = 27
  head = 0
  height = 12
  module = 1.5
  pressure_angle = 25
  reverse_pitch = true
  teeth = 16
  version = 0.0.3
FEATURE [Part::FeaturePython] wormgear077  # WARN: FeaturePython — macro-defined, semantics opaque (R4)
  AttacherType = Attacher::AttachEngine3D
  Placement = pos=(0,0,37) rot=(0,0,1;0.604757rad)
  beta = 41.1859
  clearance = 0.25
  diameter = 24
  head = 0
  height = 12
  module = 1.5
  pressure_angle = 20
  reverse_pitch = true
  teeth = 14
  version = 0.0.3
FEATURE [Part::FeaturePython] wormgear078  # WARN: FeaturePython — macro-defined, semantics opaque (R4)
  AttacherType = Attacher::AttachEngine3D
  Placement = pos=(0,0,24) rot=(0,0,1;0.261799rad)
  beta = 41.1859
  clearance = 0.25
  diameter = 24
  head = 0
  height = 13
  module = 1.5
  pressure_angle = 20
  reverse_pitch = false
  teeth = 14
  version = 0.0.3
FEATURE [Part::FeaturePython] wormgear079  # WARN: FeaturePython — macro-defined, semantics opaque (R4)
  AttacherType = Attacher::AttachEngine3D
  Placement = pos=(0,0,0) rot=(0,0,1;0.336849rad)
  beta = 41.6335
  clearance = 0.2
  diameter = 27
  head = 0
  height = 12
  module = 1.5
  pressure_angle = 25
  reverse_pitch = false
  teeth = 16
  version = 0.0.3
FEATURE [Part::Compound] Compound890
  Links = -> [wormgear079,wormgear077,wormgear076,wormgear078]
FEATURE [Part::Cut] Cut521  label="J-max-deep_outer-planeo_m1.5-fino-version"
  Base = -> Compound890
  Tool = -> Cylinder1423
FEATURE [Part::Cylinder] Cylinder1424  label="Válec1424"
  Angle = 360
  AttacherType = Attacher::AttachEngine3D
  Height = 80
  Placement = pos=(0,0,-10) rot=(0,0,1;0rad)
  Radius = 2.65
FEATURE [Part::FeaturePython] wormgear080  # WARN: FeaturePython — macro-defined, semantics opaque (R4)
  AttacherType = Attacher::AttachEngine3D
  Placement = pos=(0,0,12) rot=(0,0,1;0.551524rad)
  beta = 41.6335
  clearance = 0.2
  diameter = 27
  head = 0
  height = 12
  module = 1.5
  pressure_angle = 25
  reverse_pitch = true
  teeth = 16
  version = 0.0.3
FEATURE [Part::FeaturePython] wormgear081  # WARN: FeaturePython — macro-defined, semantics opaque (R4)
  AttacherType = Attacher::AttachEngine3D
  Placement = pos=(0,0,37) rot=(0,0,1;0.604757rad)
  beta = 41.1859
  clearance = 0.25
  diameter = 24
  head = 0
  height = 12
  module = 1.5
  pressure_angle = 20
  reverse_pitch = true
  teeth = 14
  version = 0.0.3
FEATURE [Part::FeaturePython] wormgear082  # WARN: FeaturePython — macro-defined, semantics opaque (R4)
  AttacherType = Attacher::AttachEngine3D
  Placement = pos=(0,0,24) rot=(0,0,1;0.261799rad)
  beta = 41.1859
  clearance = 0.25
  diameter = 24
  head = 0
  height = 13
  module = 1.5
  pressure_angle = 20
  reverse_pitch = false
  teeth = 14
  version = 0.0.3
FEATURE [Part::FeaturePython] wormgear083  # WARN: FeaturePython — macro-defined, semantics opaque (R4)
  AttacherType = Attacher::AttachEngine3D
  Placement = pos=(0,0,0) rot=(0,0,1;0.336849rad)
  beta = 41.6335
  clearance = 0.2
  diameter = 27
  head = 0
  height = 12
  module = 1.5
  pressure_angle = 25
  reverse_pitch = false
  teeth = 16
  version = 0.0.3
FEATURE [Part::Compound] Compound891
  Links = -> [wormgear083,wormgear081,wormgear080,wormgear082]
FEATURE [Part::Cut] Cut522  label="J-max-deep_outer-planeo_m1.5"
  Base = -> Compound891
  Tool = -> Cylinder1424
FEATURE [Sketcher::SketchObject] Sketch004
  FullyConstrained = false
  sketch-geometry (1):
    g0: Circle CenterX=-186.411 CenterY=73.9277 CenterZ=0 NormalX=0 NormalY=0 NormalZ=1 AngleXU=0 Radius=59
FEATURE [Part::Cylinder] Cylinder1425  label="Válec1425"
  Angle = 360
  AttacherType = Attacher::AttachEngine3D
  Height = 100
  Placement = pos=(103,-12,-60) rot=(0,0,1;0rad)
  Radius = 1.5
FEATURE [Part::Cylinder] Cylinder1426  label="Válec1426"
  Angle = 360
  AttacherType = Attacher::AttachEngine3D
  Height = 100
  Placement = pos=(103,6,-60) rot=(0,0,1;0rad)
  Radius = 1.5
FEATURE [Part::Cylinder] Cylinder1427  label="Válec1427"
  Angle = 360
  AttacherType = Attacher::AttachEngine3D
  Height = 100
  Placement = pos=(76,18,-60) rot=(0,0,1;0rad)
  Radius = 1.5
FEATURE [Part::Cylinder] Cylinder1428  label="Válec1428"
  Angle = 360
  AttacherType = Attacher::AttachEngine3D
  Height = 100
  Placement = pos=(91,-21,-60) rot=(0,0,1;0rad)
  Radius = 1.5
FEATURE [Part::Cylinder] Cylinder1429  label="Válec1429"
  Angle = 360
  AttacherType = Attacher::AttachEngine3D
  Height = 100
  Placement = pos=(13,-21,-60) rot=(0,0,1;0rad)
  Radius = 1.5
FEATURE [Part::Cylinder] Cylinder1430  label="Válec1430"
  Angle = 360
  AttacherType = Attacher::AttachEngine3D
  Height = 100
  Placement = pos=(28,18,-60) rot=(0,0,1;0rad)
  Radius = 1.5
FEATURE [Part::Cylinder] Cylinder1431  label="Válec1431"
  Angle = 360
  AttacherType = Attacher::AttachEngine3D
  Height = 100
  Placement = pos=(1,-12,-60) rot=(0,0,1;0rad)
  Radius = 1.5
FEATURE [Part::Cylinder] Cylinder1432  label="Válec1432"
  Angle = 360
  AttacherType = Attacher::AttachEngine3D
  Height = 100
  Placement = pos=(1,6,-60) rot=(0,0,1;0rad)
  Radius = 1.5
FEATURE [Part::Compound] Compound892  label="srouby_monoblok002"
  Links = -> [Cylinder1425,Cylinder1426,Cylinder1427,Cylinder1428,Cylinder1429,Cylinder1430,Cylinder1431,Cylinder1432]
FEATURE [Part::Cylinder] Cylinder1433  label="Válec1433"
  Angle = 360
  AttacherType = Attacher::AttachEngine3D
  Height = 100
  Placement = pos=(-50,0,-60) rot=(0,0,1;0rad)
  Radius = 1.5
FEATURE [Part::Cylinder] Cylinder1434  label="Válec1434"
  Angle = 360
  AttacherType = Attacher::AttachEngine3D
  Height = 100
  Placement = pos=(-36,34,-60) rot=(0,0,1;0rad)
  Radius = 1.5
FEATURE [Part::Cylinder] Cylinder1435  label="Válec1435"
  Angle = 360
  AttacherType = Attacher::AttachEngine3D
  Height = 100
  Placement = pos=(-36,-34,-60) rot=(0,0,1;0rad)
  Radius = 1.5
FEATURE [Part::Extrusion] Extrude002
  Base = -> Sketch004
  Dir = (52,0,32)
  DirMode = 0
  FaceMakerClass = Part::FaceMakerBullseye
  LengthFwd = 61
  LengthRev = 0
  Placement = pos=(-134,74,-22) rot=(0,0,1;3.14159rad)
  Solid = true
  Symmetric = false
FEATURE [Part::Cut] Cut524
  Base = -> Extrude002
  Tool = -> Compound892
FEATURE [Part::Cylinder] Cylinder1436  label="Válec1436"
  Angle = 360
  AttacherType = Attacher::AttachEngine3D
  Height = 100
  Placement = pos=(50,0,-60) rot=(0,0,1;0rad)
  Radius = 1.5
FEATURE [Part::Cylinder] Cylinder1437  label="Válec1437"
  Angle = 360
  AttacherType = Attacher::AttachEngine3D
  Height = 100
  Placement = pos=(36,34,-60) rot=(0,0,1;0rad)
  Radius = 1.5
FEATURE [Part::Cylinder] Cylinder1438  label="Válec1438"
  Angle = 360
  AttacherType = Attacher::AttachEngine3D
  Height = 100
  Placement = pos=(36,-34,-60) rot=(0,0,1;0rad)
  Radius = 1.5
FEATURE [Part::Compound] Compound893  label="sbouby_baze002"
  Links = -> [Cylinder1433,Cylinder1434,Cylinder1435,Cylinder1436,Cylinder1437,Cylinder1438]
FEATURE [Part::Cylinder] Cylinder1439  label="Válec1439"
  Angle = 360
  AttacherType = Attacher::AttachEngine3D
  Height = 16
  Placement = pos=(0,0,2) rot=(0,0,1;0rad)
  Radius = 59
FEATURE [Part::Cylinder] Cylinder1440  label="Válec1440"
  Angle = 360
  AttacherType = Attacher::AttachEngine3D
  Height = 4
  Placement = pos=(52,0,-26) rot=(0,0,1;0rad)
  Radius = 59
FEATURE [Part::Cylinder] Cylinder1441  label="Válec1441"
  Angle = 360
  AttacherType = Attacher::AttachEngine3D
  Height = 100
  Placement = pos=(103,-12,-60) rot=(0,0,1;0rad)
  Radius = 1.5
FEATURE [Part::Cylinder] Cylinder1442  label="Válec1442"
  Angle = 360
  AttacherType = Attacher::AttachEngine3D
  Height = 100
  Placement = pos=(103,6,-60) rot=(0,0,1;0rad)
  Radius = 1.5
FEATURE [Part::Cylinder] Cylinder1443  label="Válec1443"
  Angle = 360
  AttacherType = Attacher::AttachEngine3D
  Height = 100
  Placement = pos=(76,18,-60) rot=(0,0,1;0rad)
  Radius = 1.5
FEATURE [Part::Cylinder] Cylinder1444  label="Válec1444"
  Angle = 360
  AttacherType = Attacher::AttachEngine3D
  Height = 100
  Placement = pos=(91,-21,-60) rot=(0,0,1;0rad)
  Radius = 1.5
FEATURE [Part::Cylinder] Cylinder1445  label="Válec1445"
  Angle = 360
  AttacherType = Attacher::AttachEngine3D
  Height = 100
  Placement = pos=(13,-21,-60) rot=(0,0,1;0rad)
  Radius = 1.5
FEATURE [Part::Cylinder] Cylinder1446  label="Válec1446"
  Angle = 360
  AttacherType = Attacher::AttachEngine3D
  Height = 100
  Placement = pos=(28,18,-60) rot=(0,0,1;0rad)
  Radius = 1.5
FEATURE [Part::Cylinder] Cylinder1447  label="Válec1447"
  Angle = 360
  AttacherType = Attacher::AttachEngine3D
  Height = 100
  Placement = pos=(1,-12,-60) rot=(0,0,1;0rad)
  Radius = 1.5
FEATURE [Part::Cylinder] Cylinder1448  label="Válec1448"
  Angle = 360
  AttacherType = Attacher::AttachEngine3D
  Height = 100
  Placement = pos=(1,6,-60) rot=(0,0,1;0rad)
  Radius = 1.5
FEATURE [Part::Compound] Compound894  label="srouby_monoblok003"
  Links = -> [Cylinder1441,Cylinder1442,Cylinder1443,Cylinder1444,Cylinder1445,Cylinder1446,Cylinder1447,Cylinder1448]
FEATURE [Part::Cut] Cut526
  Base = -> Cylinder1440
  Tool = -> Compound894
FEATURE [Part::Cylinder] Cylinder1449  label="Válec1449"
  Angle = 360
  AttacherType = Attacher::AttachEngine3D
  Height = 20
  Placement = pos=(103,-12,-20) rot=(0,0,1;0rad)
  Radius = 4
FEATURE [Part::Cylinder] Cylinder1450  label="Válec1450"
  Angle = 360
  AttacherType = Attacher::AttachEngine3D
  Height = 20
  Placement = pos=(103,6,-20) rot=(0,0,1;0rad)
  Radius = 4
FEATURE [Part::Cylinder] Cylinder1451  label="Válec1451"
  Angle = 360
  AttacherType = Attacher::AttachEngine3D
  Height = 20
  Placement = pos=(76,18,-18) rot=(0,0,1;0rad)
  Radius = 4
FEATURE [Part::Cylinder] Cylinder1452  label="Válec1452"
  Angle = 360
  AttacherType = Attacher::AttachEngine3D
  Height = 20
  Placement = pos=(91,-21,-18) rot=(0,0,1;0rad)
  Radius = 4
FEATURE [Part::Cylinder] Cylinder1453  label="Válec1453"
  Angle = 360
  AttacherType = Attacher::AttachEngine3D
  Height = 40
  Placement = pos=(13,-21,-18) rot=(0,0,1;0rad)
  Radius = 4
FEATURE [Part::Cylinder] Cylinder1454  label="Válec1454"
  Angle = 360
  AttacherType = Attacher::AttachEngine3D
  Height = 40
  Placement = pos=(28,18,-18) rot=(0,0,1;0rad)
  Radius = 4
FEATURE [Part::Cylinder] Cylinder1455  label="Válec1455"
  Angle = 360
  AttacherType = Attacher::AttachEngine3D
  Height = 40
  Placement = pos=(1,-12,-18) rot=(0,0,1;0rad)
  Radius = 4
FEATURE [Part::Cylinder] Cylinder1456  label="Válec1456"
  Angle = 360
  AttacherType = Attacher::AttachEngine3D
  Height = 40
  Placement = pos=(1,6,-18) rot=(0,0,1;0rad)
  Radius = 4
FEATURE [Part::Compound] Compound895  label="srouby_monoblok_silne003"
  Links = -> [Cylinder1449,Cylinder1450,Cylinder1451,Cylinder1452,Cylinder1453,Cylinder1454,Cylinder1455,Cylinder1456]
FEATURE [Part::Cut] Cut523
  Base = -> Cut524
  Tool = -> Compound895
FEATURE [Part::Cylinder] Cylinder1457  label="Válec1457"
  Angle = 360
  AttacherType = Attacher::AttachEngine3D
  Height = 20
  Placement = pos=(103,-12,-20) rot=(0,0,1;0rad)
  Radius = 4
FEATURE [Part::Cylinder] Cylinder1458  label="Válec1458"
  Angle = 360
  AttacherType = Attacher::AttachEngine3D
  Height = 20
  Placement = pos=(103,6,-20) rot=(0,0,1;0rad)
  Radius = 4
FEATURE [Part::Cylinder] Cylinder1459  label="Válec1459"
  Angle = 360
  AttacherType = Attacher::AttachEngine3D
  Height = 20
  Placement = pos=(76,18,-18) rot=(0,0,1;0rad)
  Radius = 4
FEATURE [Part::Cylinder] Cylinder1460  label="Válec1460"
  Angle = 360
  AttacherType = Attacher::AttachEngine3D
  Height = 20
  Placement = pos=(91,-21,-18) rot=(0,0,1;0rad)
  Radius = 4
FEATURE [Part::Cylinder] Cylinder1461  label="Válec1461"
  Angle = 360
  AttacherType = Attacher::AttachEngine3D
  Height = 40
  Placement = pos=(13,-21,-18) rot=(0,0,1;0rad)
  Radius = 4
FEATURE [Part::Cylinder] Cylinder1462  label="Válec1462"
  Angle = 360
  AttacherType = Attacher::AttachEngine3D
  Height = 40
  Placement = pos=(28,18,-18) rot=(0,0,1;0rad)
  Radius = 4
FEATURE [Part::Cylinder] Cylinder1463  label="Válec1463"
  Angle = 360
  AttacherType = Attacher::AttachEngine3D
  Height = 40
  Placement = pos=(1,-12,-18) rot=(0,0,1;0rad)
  Radius = 4
FEATURE [Part::Cylinder] Cylinder1464  label="Válec1464"
  Angle = 360
  AttacherType = Attacher::AttachEngine3D
  Height = 40
  Placement = pos=(1,6,-18) rot=(0,0,1;0rad)
  Radius = 4
FEATURE [Part::Compound] Compound896  label="srouby_monoblok_silne004"
  Links = -> [Cylinder1457,Cylinder1458,Cylinder1459,Cylinder1460,Cylinder1461,Cylinder1462,Cylinder1463,Cylinder1464]
FEATURE [Part::Cut] Cut525
  Base = -> Cylinder1439
  Tool = -> Compound896
FEATURE [Part::Cylinder] Cylinder1465  label="Válec1465"
  Angle = 360
  AttacherType = Attacher::AttachEngine3D
  Height = 100
  Placement = pos=(36,34,-90) rot=(0,0,1;0rad)
  Radius = 4
FEATURE [Part::Cylinder] Cylinder1466  label="Válec1466"
  Angle = 360
  AttacherType = Attacher::AttachEngine3D
  Height = 100
  Placement = pos=(-50,0,-90) rot=(0,0,1;0rad)
  Radius = 4
FEATURE [Part::Cylinder] Cylinder1467  label="Válec1467"
  Angle = 360
  AttacherType = Attacher::AttachEngine3D
  Height = 100
  Placement = pos=(-36,34,-90) rot=(0,0,1;0rad)
  Radius = 4
FEATURE [Part::Cylinder] Cylinder1468  label="Válec1468"
  Angle = 360
  AttacherType = Attacher::AttachEngine3D
  Height = 100
  Placement = pos=(-36,-34,-90) rot=(0,0,1;0rad)
  Radius = 4
FEATURE [Part::Cylinder] Cylinder1469  label="Válec1469"
  Angle = 360
  AttacherType = Attacher::AttachEngine3D
  Height = 100
  Placement = pos=(50,0,-90) rot=(0,0,1;0rad)
  Radius = 4
FEATURE [Part::Cylinder] Cylinder1470  label="Válec1470"
  Angle = 360
  AttacherType = Attacher::AttachEngine3D
  Height = 100
  Placement = pos=(36,-34,-90) rot=(0,0,1;0rad)
  Radius = 4
FEATURE [Part::Compound] Compound897  label="sbouby_baze_silne003"
  Links = -> [Cylinder1466,Cylinder1467,Cylinder1468,Cylinder1469,Cylinder1465,Cylinder1470]
FEATURE [Part::Cut] Cut527
  Base = -> Cut526
  Tool = -> Compound897
FEATURE [Part::Cylinder] Cylinder1471  label="Válec1471"
  Angle = 360
  AttacherType = Attacher::AttachEngine3D
  Height = 100
  Placement = pos=(36,34,-90) rot=(0,0,1;0rad)
  Radius = 4
FEATURE [Part::Cylinder] Cylinder1472  label="Válec1472"
  Angle = 360
  AttacherType = Attacher::AttachEngine3D
  Height = 100
  Placement = pos=(-50,0,-90) rot=(0,0,1;0rad)
  Radius = 4
FEATURE [Part::Cylinder] Cylinder1473  label="Válec1473"
  Angle = 360
  AttacherType = Attacher::AttachEngine3D
  Height = 100
  Placement = pos=(-36,34,-90) rot=(0,0,1;0rad)
  Radius = 4
FEATURE [Part::Cylinder] Cylinder1474  label="Válec1474"
  Angle = 360
  AttacherType = Attacher::AttachEngine3D
  Height = 100
  Placement = pos=(-36,-34,-90) rot=(0,0,1;0rad)
  Radius = 4
FEATURE [Part::Cylinder] Cylinder1475  label="Válec1475"
  Angle = 360
  AttacherType = Attacher::AttachEngine3D
  Height = 100
  Placement = pos=(50,0,-90) rot=(0,0,1;0rad)
  Radius = 4
FEATURE [Part::Cylinder] Cylinder1476  label="Válec1476"
  Angle = 360
  AttacherType = Attacher::AttachEngine3D
  Height = 100
  Placement = pos=(36,-34,-90) rot=(0,0,1;0rad)
  Radius = 4
FEATURE [Part::Compound] Compound898  label="sbouby_baze_silne004"
  Links = -> [Cylinder1472,Cylinder1473,Cylinder1474,Cylinder1475,Cylinder1471,Cylinder1476]
FEATURE [Part::Cut] Cut529
  Base = -> Cut525
  Tool = -> Compound898
FEATURE [Part::Cut] Cut531
  Base = -> Cut529
  Tool = -> Compound893
FEATURE [Part::Chamfer] Chamfer037
  Base = -> Cut531
  Edges = 1 edges r=4: [Edge3]
FEATURE [Part::Cylinder] Cylinder1477  label="Válec1477"
  Angle = 360
  AttacherType = Attacher::AttachEngine3D
  Height = 100
  Placement = pos=(36,34,-90) rot=(0,0,1;0rad)
  Radius = 4
FEATURE [Part::Cylinder] Cylinder1478  label="Válec1478"
  Angle = 360
  AttacherType = Attacher::AttachEngine3D
  Height = 100
  Placement = pos=(-50,0,-90) rot=(0,0,1;0rad)
  Radius = 4
FEATURE [Part::Cylinder] Cylinder1479  label="Válec1479"
  Angle = 360
  AttacherType = Attacher::AttachEngine3D
  Height = 100
  Placement = pos=(-36,34,-90) rot=(0,0,1;0rad)
  Radius = 4
FEATURE [Part::Cylinder] Cylinder1480  label="Válec1480"
  Angle = 360
  AttacherType = Attacher::AttachEngine3D
  Height = 100
  Placement = pos=(-36,-34,-90) rot=(0,0,1;0rad)
  Radius = 4
FEATURE [Part::Cylinder] Cylinder1481  label="Válec1481"
  Angle = 360
  AttacherType = Attacher::AttachEngine3D
  Height = 100
  Placement = pos=(50,0,-90) rot=(0,0,1;0rad)
  Radius = 4
FEATURE [Part::Cylinder] Cylinder1482  label="Válec1482"
  Angle = 360
  AttacherType = Attacher::AttachEngine3D
  Height = 100
  Placement = pos=(36,-34,-90) rot=(0,0,1;0rad)
  Radius = 4
FEATURE [Part::Compound] Compound899  label="sbouby_baze_silne005"
  Links = -> [Cylinder1478,Cylinder1479,Cylinder1480,Cylinder1481,Cylinder1477,Cylinder1482]
FEATURE [Part::Cut] Cut528
  Base = -> Cut523
  Tool = -> Compound899
FEATURE [Part::Cylinder] Cylinder1483  label="Válec1483"
  Angle = 360
  AttacherType = Attacher::AttachEngine3D
  Height = 100
  Placement = pos=(36,34,-60) rot=(0,0,1;0rad)
  Radius = 1.5
FEATURE [Part::Cylinder] Cylinder1484  label="Válec1484"
  Angle = 360
  AttacherType = Attacher::AttachEngine3D
  Height = 100
  Placement = pos=(-50,0,-60) rot=(0,0,1;0rad)
  Radius = 1.5
FEATURE [Part::Cylinder] Cylinder1485  label="Válec1485"
  Angle = 360
  AttacherType = Attacher::AttachEngine3D
  Height = 100
  Placement = pos=(-36,34,-60) rot=(0,0,1;0rad)
  Radius = 1.5
FEATURE [Part::Cylinder] Cylinder1486  label="Válec1486"
  Angle = 360
  AttacherType = Attacher::AttachEngine3D
  Height = 100
  Placement = pos=(-36,-34,-60) rot=(0,0,1;0rad)
  Radius = 1.5
FEATURE [Part::Cylinder] Cylinder1487  label="Válec1487"
  Angle = 360
  AttacherType = Attacher::AttachEngine3D
  Height = 100
  Placement = pos=(50,0,-60) rot=(0,0,1;0rad)
  Radius = 1.5
FEATURE [Part::Cylinder] Cylinder1488  label="Válec1488"
  Angle = 360
  AttacherType = Attacher::AttachEngine3D
  Height = 100
  Placement = pos=(36,-34,-60) rot=(0,0,1;0rad)
  Radius = 1.5
FEATURE [Part::Compound] Compound900  label="sbouby_baze003"
  Links = -> [Cylinder1484,Cylinder1485,Cylinder1486,Cylinder1487,Cylinder1483,Cylinder1488]
FEATURE [Part::Cut] Cut530
  Base = -> Cut528
  Tool = -> Compound900
FEATURE [Part::Box] Box515  label="Krychle515"
  AttacherType = Attacher::AttachEngine3D
  Height = 100
  Length = 200
  Placement = pos=(-60,-130,-90) rot=(0,0,1;0rad)
  Width = 100
FEATURE [Part::Cut] Cut532
  Base = -> Cut530
  Tool = -> Box515
FEATURE [Part::Box] Box516  label="Krychle516"
  AttacherType = Attacher::AttachEngine3D
  Height = 100
  Length = 200
  Placement = pos=(-60,-124,-90) rot=(0,0,1;0rad)
  Width = 100
FEATURE [Part::Box] Box517  label="Krychle517"
  AttacherType = Attacher::AttachEngine3D
  Height = 100
  Length = 200
  Placement = pos=(-60,44,-90) rot=(0,0,1;0rad)
  Width = 100
FEATURE [Part::Cut] Cut533
  Base = -> Cut527
  Tool = -> Box516
FEATURE [Part::Cut] Cut534
  Base = -> Cut532
  Tool = -> Box517
FEATURE [Part::Box] Box518  label="Krychle518"
  AttacherType = Attacher::AttachEngine3D
  Height = 100
  Length = 200
  Placement = pos=(-60,44,-90) rot=(0,0,1;0rad)
  Width = 100
FEATURE [Part::Cut] Cut535
  Base = -> Cut533
  Tool = -> Box518
FEATURE [Part::Cylinder] Cylinder1489  label="Válec1489"
  Angle = 360
  AttacherType = Attacher::AttachEngine3D
  Height = 100
  Placement = pos=(90,0,-60) rot=(0,0,1;0rad)
  Radius = 1.5
FEATURE [Part::Cylinder] Cylinder1490  label="Válec1490"
  Angle = 360
  AttacherType = Attacher::AttachEngine3D
  Height = 100
  Placement = pos=(14,0,-60) rot=(0,0,1;0rad)
  Radius = 1.5
FEATURE [Part::Cylinder] Cylinder1491  label="Válec1491"
  Angle = 360
  AttacherType = Attacher::AttachEngine3D
  Height = 100
  Placement = pos=(90,0,-18) rot=(0,0,1;0rad)
  Radius = 4
FEATURE [Part::Compound] Compound905  label="srouby_troj006"
  Links = -> [Cylinder1489,Cylinder1490]
FEATURE [Part::Cylinder] Cylinder1492  label="Válec1492"
  Angle = 360
  AttacherType = Attacher::AttachEngine3D
  Height = 100
  Placement = pos=(14,0,-18) rot=(0,0,1;0rad)
  Radius = 4
FEATURE [Part::Compound] Compound904  label="srouby_troj_silne002"
  Links = -> [Cylinder1491,Cylinder1492]
FEATURE [Part::Box] Box519  label="Krychle519"
  AttacherType = Attacher::AttachEngine3D
  Height = 2
  Length = 6
  Placement = pos=(75,38,-22) rot=(0,0,1;0rad)
  Width = 6
FEATURE [Part::Box] Box520  label="Krychle520"
  AttacherType = Attacher::AttachEngine3D
  Height = 2
  Length = 6
  Placement = pos=(23,38,-22) rot=(0,0,1;0rad)
  Width = 6
FEATURE [Part::Compound] Compound901
  Links = -> [Box519,Box520]
FEATURE [Part::Cut] Cut537
  Base = -> Cut534
  Tool = -> Compound901
FEATURE [Part::Cylinder] Cylinder1493  label="Válec1493"
  Angle = 360
  AttacherType = Attacher::AttachEngine3D
  Height = 32
  Placement = pos=(26,41,-42) rot=(0,0,1;0rad)
  Radius = 1.5
FEATURE [Part::Cylinder] Cylinder1494  label="Válec1494"
  Angle = 360
  AttacherType = Attacher::AttachEngine3D
  Height = 32
  Placement = pos=(78,41,-42) rot=(0,0,1;0rad)
  Radius = 1.5
FEATURE [Part::Compound] Compound902
  Links = -> [Cylinder1493,Cylinder1494]
FEATURE [Part::Cut] Cut536
  Base = -> Cut535
  Tool = -> Compound902
FEATURE [Part::Cylinder] Cylinder1495  label="Válec1495"
  Angle = 360
  AttacherType = Attacher::AttachEngine3D
  Height = 32
  Placement = pos=(26,41,-46) rot=(0,0,1;0rad)
  Radius = 1.5
FEATURE [Part::Cylinder] Cylinder1496  label="Válec1496"
  Angle = 360
  AttacherType = Attacher::AttachEngine3D
  Height = 32
  Placement = pos=(78,41,-46) rot=(0,0,1;0rad)
  Radius = 1.5
FEATURE [Part::Compound] Compound903
  Links = -> [Cylinder1495,Cylinder1496]
FEATURE [Part::Cut] Cut538
  Base = -> Cut537
  Tool = -> Compound903
FEATURE [Part::Cut] Cut540
  Base = -> Cut538
  Tool = -> Compound905
FEATURE [Part::Cut] Cut541
  Base = -> Cut540
  Tool = -> Compound904
FEATURE [Part::Chamfer] Chamfer038
  Base = -> Cut541
  Edges = 2 edges r=6: [Edge40,Edge42]
FEATURE [Part::Cylinder] Cylinder1497  label="Válec1497"
  Angle = 360
  AttacherType = Attacher::AttachEngine3D
  Height = 100
  Placement = pos=(90,0,-18) rot=(0,0,1;0rad)
  Radius = 4
FEATURE [Part::Cylinder] Cylinder1498  label="Válec1498"
  Angle = 360
  AttacherType = Attacher::AttachEngine3D
  Height = 100
  Placement = pos=(14,0,-18) rot=(0,0,1;0rad)
  Radius = 4
FEATURE [Part::Compound] Compound906  label="srouby_troj_silne003"
  Links = -> [Cylinder1497,Cylinder1498]
FEATURE [Part::Cut] Cut542
  Base = -> Chamfer037
  Placement = pos=(0,0,4) rot=(0,0,1;0rad)
  Tool = -> Compound906
FEATURE [Part::Cylinder] Cylinder1499  label="Válec1499"
  Angle = 360
  AttacherType = Attacher::AttachEngine3D
  Height = 100
  Placement = pos=(90,0,-60) rot=(0,0,1;0rad)
  Radius = 1.5
FEATURE [Part::Cylinder] Cylinder1500  label="Válec1500"
  Angle = 360
  AttacherType = Attacher::AttachEngine3D
  Height = 100
  Placement = pos=(14,0,-60) rot=(0,0,1;0rad)
  Radius = 1.5
FEATURE [Part::Compound] Compound907  label="srouby_troj007"
  Links = -> [Cylinder1499,Cylinder1500]
FEATURE [Part::Cut] Cut539
  Base = -> Cut536
  Tool = -> Compound907
FEATURE [Part::Compound] Compound662  label="Base_neck-foreshift"
  Links = -> [Cut539,Cut542,Chamfer038]
  Placement = pos=(52,-79,13) rot=(0,0.707107,-0.707107;3.14159rad)
FEATURE [Part::Cylinder] Cylinder1501  label="Válec1501"
  Angle = 360
  AttacherType = Attacher::AttachEngine3D
  Height = 50
  Placement = pos=(-56,-1.3e-14,2) rot=(0,0,-1;1.5708rad)
  Radius = 1.5
FEATURE [Part::Cylinder] Cylinder1502  label="Válec1502"
  Angle = 360
  AttacherType = Attacher::AttachEngine3D
  Height = 20
  Placement = pos=(-51,-40,7) rot=(1,0,0;1.5708rad)
  Radius = 1.5
FEATURE [Part::Cylinder] Cylinder1503  label="Válec1503"
  Angle = 360
  AttacherType = Attacher::AttachEngine3D
  Height = 50
  Placement = pos=(39.598,39.598,2) rot=(0,0,1;2.35619rad)
  Radius = 1.5
FEATURE [Part::Cylinder] Cylinder1504  label="Válec1504"
  Angle = 360
  AttacherType = Attacher::AttachEngine3D
  Height = 50
  Placement = pos=(0,-56,2) rot=(0,0,1;0rad)
  Radius = 1.5
FEATURE [Part::Cylinder] Cylinder1505  label="Válec1505"
  Angle = 360
  AttacherType = Attacher::AttachEngine3D
  Height = 50
  Placement = pos=(-39.598,-39.598,2) rot=(0,0,-1;0.785398rad)
  Radius = 1.5
FEATURE [Part::Cylinder] Cylinder1506  label="Válec1506"
  Angle = 360
  AttacherType = Attacher::AttachEngine3D
  Height = 50
  Placement = pos=(-39.598,-39.598,2) rot=(0,0,-1;0.785398rad)
  Radius = 1.5
FEATURE [Part::Box] Box521  label="Krychle521"
  AttacherType = Attacher::AttachEngine3D
  Height = 6
  Length = 6
  Placement = pos=(48,-45,4) rot=(0,0,1;0rad)
  Width = 2
FEATURE [Part::Cylinder] Cylinder1507  label="Válec1507"
  Angle = 360
  AttacherType = Attacher::AttachEngine3D
  Height = 20
  Placement = pos=(-51,-40,7) rot=(1,0,0;1.5708rad)
  Radius = 1.5
FEATURE [Part::Box] Box522  label="Krychle522"
  AttacherType = Attacher::AttachEngine3D
  Height = 2
  Length = 6
  Placement = pos=(41,3,-4) rot=(0,0,-1;1.5708rad)
  Width = 8
FEATURE [Part::Cylinder] Cylinder1508  label="Válec1508"
  Angle = 360
  AttacherType = Attacher::AttachEngine3D
  Height = 50
  Placement = pos=(39.598,39.598,2) rot=(0,0,1;2.35619rad)
  Radius = 1.5
FEATURE [Part::Cylinder] Cylinder1509  label="Válec1509"
  Angle = 360
  AttacherType = Attacher::AttachEngine3D
  Height = 50
  Placement = pos=(-1.2e-14,56,2) rot=(0,0,1;3.14159rad)
  Radius = 1.5
FEATURE [Part::Cylinder] Cylinder1510  label="Válec1510"
  Angle = 360
  AttacherType = Attacher::AttachEngine3D
  Height = 40
  Placement = pos=(-59,-17,0) rot=(0,0,1;0rad)
  Radius = 10
FEATURE [Part::Box] Box523  label="Krychle523"
  AttacherType = Attacher::AttachEngine3D
  Height = 12
  Length = 10
  Placement = pos=(-60,-43,10) rot=(0,0,1;0rad)
  Width = 43
FEATURE [Part::Cylinder] Cylinder1511  label="Válec1511"
  Angle = 360
  AttacherType = Attacher::AttachEngine3D
  Height = 50
  Placement = pos=(-1.2e-14,56,2) rot=(0,0,1;3.14159rad)
  Radius = 1.5
FEATURE [Part::Cylinder] Cylinder1512  label="Válec1512"
  Angle = 360
  AttacherType = Attacher::AttachEngine3D
  Height = 20
  Placement = pos=(39.6,-39.6,-10) rot=(0,0,1;0.785398rad)
  Radius = 4
FEATURE [Part::Cylinder] Cylinder1513  label="Válec1513"
  Angle = 360
  AttacherType = Attacher::AttachEngine3D
  Height = 50
  Placement = pos=(56,0,2) rot=(0,0,1;1.5708rad)
  Radius = 1.5
FEATURE [Part::Cylinder] Cylinder1514  label="Válec1514"
  Angle = 360
  AttacherType = Attacher::AttachEngine3D
  Height = 50
  Placement = pos=(-56,-1.3e-14,2) rot=(0,0,-1;1.5708rad)
  Radius = 1.5
FEATURE [Part::Cylinder] Cylinder1515  label="Válec1515"
  Angle = 360
  AttacherType = Attacher::AttachEngine3D
  Height = 20
  Placement = pos=(51,-40,7) rot=(1,0,0;1.5708rad)
  Radius = 1.5
FEATURE [Part::Box] Box524  label="Krychle524"
  AttacherType = Attacher::AttachEngine3D
  Height = 12
  Length = 108
  Placement = pos=(-54,-53,20) rot=(0,0,1;0rad)
  Width = 36
FEATURE [Part::Cylinder] Cylinder1516  label="Válec1516"
  Angle = 360
  AttacherType = Attacher::AttachEngine3D
  Height = 16
  Placement = pos=(0,0,20) rot=(0,0,1;0rad)
  Radius = 52
FEATURE [Part::Box] Box525  label="Krychle525"
  AttacherType = Attacher::AttachEngine3D
  Height = 2
  Length = 6
  Placement = pos=(-41,-3,-4) rot=(0,0,1;1.5708rad)
  Width = 8
FEATURE [Part::Box] Box526  label="Krychle526"
  AttacherType = Attacher::AttachEngine3D
  Height = 2
  Length = 6
  Placement = pos=(3,-41,-4) rot=(0,0,1;3.14159rad)
  Width = 8
FEATURE [Part::Cylinder] Cylinder1517  label="Válec1517"
  Angle = 360
  AttacherType = Attacher::AttachEngine3D
  Height = 20
  Placement = pos=(24,-40,-5) rot=(1,0,0;1.5708rad)
  Radius = 1.5
FEATURE [Part::Cylinder] Cylinder1518  label="Válec1518"
  Angle = 360
  AttacherType = Attacher::AttachEngine3D
  Height = 20
  Placement = pos=(-24,-40,-5) rot=(1,0,0;1.5708rad)
  Radius = 1.5
FEATURE [Part::Cylinder] Cylinder1519  label="Válec1519"
  Angle = 360
  AttacherType = Attacher::AttachEngine3D
  Height = 50
  Placement = pos=(0,-56,2) rot=(0,0,1;0rad)
  Radius = 1.5
FEATURE [Part::Box] Box527  label="Krychle527"
  AttacherType = Attacher::AttachEngine3D
  Height = 6
  Length = 6
  Placement = pos=(-27,-47,-8) rot=(0,0,1;0rad)
  Width = 2
FEATURE [Part::Cylinder] Cylinder1520  label="Válec1520"
  Angle = 360
  AttacherType = Attacher::AttachEngine3D
  Height = 20
  Placement = pos=(-45,-6e-15,-18) rot=(0,0,1;1.5708rad)
  Radius = 1.5
FEATURE [Part::Cylinder] Cylinder1521  label="Válec1521"
  Angle = 360
  AttacherType = Attacher::AttachEngine3D
  Height = 50
  Placement = pos=(-39.598,39.598,2) rot=(0,0,1;3.92699rad)
  Radius = 1.5
FEATURE [Part::Cylinder] Cylinder1522  label="Válec1522"
  Angle = 360
  AttacherType = Attacher::AttachEngine3D
  Height = 20
  Placement = pos=(0,45,-18) rot=(0,0,1;0rad)
  Radius = 1.5
FEATURE [Part::Cylinder] Cylinder1523  label="Válec1523"
  Angle = 360
  AttacherType = Attacher::AttachEngine3D
  Height = 20
  Placement = pos=(1.4e-14,-45,-18) rot=(0,0,1;3.14159rad)
  Radius = 1.5
FEATURE [Part::Box] Box528  label="Krychle528"
  AttacherType = Attacher::AttachEngine3D
  Height = 2
  Length = 6
  Placement = pos=(-3,41,-4) rot=(0,0,1;0rad)
  Width = 8
FEATURE [Part::Box] Box529  label="Krychle529"
  AttacherType = Attacher::AttachEngine3D
  Height = 2
  Length = 6
  Placement = pos=(-31.1127,26.8701,-4) rot=(0,0,1;0.785398rad)
  Width = 8
FEATURE [Part::Cylinder] Cylinder1524  label="Válec1524"
  Angle = 360
  AttacherType = Attacher::AttachEngine3D
  Height = 20
  Placement = pos=(-31.8198,-31.8198,-18) rot=(0,0,1;2.35619rad)
  Radius = 1.5
FEATURE [Part::Box] Box530  label="Krychle530"
  AttacherType = Attacher::AttachEngine3D
  Height = 6
  Length = 6
  Placement = pos=(-54,-45,4) rot=(0,0,1;0rad)
  Width = 2
FEATURE [Part::Cylinder] Cylinder1525  label="Válec1525"
  Angle = 360
  AttacherType = Attacher::AttachEngine3D
  Height = 50
  Placement = pos=(39.598,-39.598,2) rot=(0,0,1;0.785398rad)
  Radius = 1.5
FEATURE [Part::Cylinder] Cylinder1526  label="Válec1526"
  Angle = 360
  AttacherType = Attacher::AttachEngine3D
  Height = 20
  Placement = pos=(31.8198,31.8198,-18) rot=(0,0,-1;0.785398rad)
  Radius = 1.5
FEATURE [Part::Cylinder] Cylinder1527  label="Válec1527"
  Angle = 360
  AttacherType = Attacher::AttachEngine3D
  Height = 20
  Placement = pos=(-31.8198,31.8198,-18) rot=(0,0,1;0.785398rad)
  Radius = 1.5
FEATURE [Part::Box] Box531  label="Krychle531"
  AttacherType = Attacher::AttachEngine3D
  Height = 2
  Length = 6
  Placement = pos=(31.1127,-26.8701,-4) rot=(0,0,1;3.92699rad)
  Width = 8
FEATURE [Part::Cylinder] Cylinder1528  label="Válec1528"
  Angle = 360
  AttacherType = Attacher::AttachEngine3D
  Height = 20
  Placement = pos=(45,1.9e-14,-18) rot=(0,0,-1;1.5708rad)
  Radius = 1.5
FEATURE [Part::Box] Box532  label="Krychle532"
  AttacherType = Attacher::AttachEngine3D
  Height = 2
  Length = 6
  Placement = pos=(-26.8701,-31.1127,-4) rot=(0,0,1;2.35619rad)
  Width = 8
FEATURE [Part::Cylinder] Cylinder1529  label="Válec1529"
  Angle = 360
  AttacherType = Attacher::AttachEngine3D
  Height = 50
  Placement = pos=(31.8198,31.8198,-18) rot=(0,0,-1;0.785398rad)
  Radius = 1.5
FEATURE [Part::Cylinder] Cylinder1530  label="Válec1530"
  Angle = 360
  AttacherType = Attacher::AttachEngine3D
  Height = 50
  Placement = pos=(31.8198,-31.8198,-18) rot=(0,0,1;3.92699rad)
  Radius = 1.5
FEATURE [Part::Cylinder] Cylinder1531  label="Válec1531"
  Angle = 360
  AttacherType = Attacher::AttachEngine3D
  Height = 50
  Placement = pos=(39.598,-39.598,2) rot=(0,0,1;0.785398rad)
  Radius = 1.5
FEATURE [Part::Box] Box533  label="Krychle533"
  AttacherType = Attacher::AttachEngine3D
  Height = 2
  Length = 6
  Placement = pos=(26.8701,31.1127,-4) rot=(0,0,-1;0.785398rad)
  Width = 8
FEATURE [Part::Box] Box534  label="Krychle534"
  AttacherType = Attacher::AttachEngine3D
  Height = 6
  Length = 6
  Placement = pos=(21,-47,-8) rot=(0,0,1;0rad)
  Width = 2
FEATURE [Part::Cylinder] Cylinder1532  label="Válec1532"
  Angle = 360
  AttacherType = Attacher::AttachEngine3D
  Height = 20
  Placement = pos=(31.8198,-31.8198,-18) rot=(0,0,1;3.92699rad)
  Radius = 1.5
FEATURE [Part::Cylinder] Cylinder1533  label="Válec1533"
  Angle = 360
  AttacherType = Attacher::AttachEngine3D
  Height = 50
  Placement = pos=(0,45,-18) rot=(0,0,1;0rad)
  Radius = 1.5
FEATURE [Part::Cylinder] Cylinder1534  label="Válec1534"
  Angle = 360
  AttacherType = Attacher::AttachEngine3D
  Height = 50
  Placement = pos=(1.4e-14,-45,-18) rot=(0,0,1;3.14159rad)
  Radius = 1.5
FEATURE [Part::Cylinder] Cylinder1535  label="Válec1535"
  Angle = 360
  AttacherType = Attacher::AttachEngine3D
  Height = 50
  Placement = pos=(-39.598,-39.598,2) rot=(0,0,-1;0.785398rad)
  Radius = 1.5
FEATURE [Part::Cylinder] Cylinder1536  label="Válec1536"
  Angle = 360
  AttacherType = Attacher::AttachEngine3D
  Height = 50
  Placement = pos=(-56,-1.3e-14,2) rot=(0,0,-1;1.5708rad)
  Radius = 1.5
FEATURE [Part::Box] Box535  label="Krychle535"
  AttacherType = Attacher::AttachEngine3D
  Height = 6
  Length = 6
  Placement = pos=(-54,-45,4) rot=(0,0,1;0rad)
  Width = 2
FEATURE [Part::Cylinder] Cylinder1537  label="Válec1537"
  Angle = 360
  AttacherType = Attacher::AttachEngine3D
  Height = 8
  Placement = pos=(0,0,20) rot=(0,0,1;0rad)
  Radius = 52
FEATURE [Part::Cylinder] Cylinder1538  label="Válec1538"
  Angle = 360
  AttacherType = Attacher::AttachEngine3D
  Height = 20
  Placement = pos=(51,-40,7) rot=(1,0,0;1.5708rad)
  Radius = 1.5
FEATURE [Part::Box] Box536  label="Krychle536"
  AttacherType = Attacher::AttachEngine3D
  Height = 6
  Length = 6
  Placement = pos=(48,-45,4) rot=(0,0,1;0rad)
  Width = 2
FEATURE [Part::Cylinder] Cylinder1539  label="Válec1539"
  Angle = 360
  AttacherType = Attacher::AttachEngine3D
  Height = 20
  Placement = pos=(-39.6,-39.6,-10) rot=(0,0,-1;0.785398rad)
  Radius = 4
FEATURE [Part::Cylinder] Cylinder1540  label="Válec1540"
  Angle = 360
  AttacherType = Attacher::AttachEngine3D
  Height = 20
  Placement = pos=(-24,-40,-5) rot=(1,0,0;1.5708rad)
  Radius = 1.5
FEATURE [Part::Cylinder] Cylinder1541  label="Válec1541"
  Angle = 360
  AttacherType = Attacher::AttachEngine3D
  Height = 40
  Placement = pos=(59,-17,0) rot=(0,0,1;0rad)
  Radius = 10
FEATURE [Part::Cylinder] Cylinder1542  label="Válec1542"
  Angle = 360
  AttacherType = Attacher::AttachEngine3D
  Height = 16
  Placement = pos=(60,-43,10) rot=(0,0,1;0rad)
  Radius = 6
FEATURE [Part::Cylinder] Cylinder1543  label="Válec1543"
  Angle = 360
  AttacherType = Attacher::AttachEngine3D
  Height = 50
  Placement = pos=(39.598,-39.598,2) rot=(0,0,1;0.785398rad)
  Radius = 1.5
FEATURE [Part::Box] Box537  label="Krychle537"
  AttacherType = Attacher::AttachEngine3D
  Height = 8
  Length = 108
  Placement = pos=(-54,-53,20) rot=(0,0,1;0rad)
  Width = 36
FEATURE [Part::Box] Box538  label="Krychle538"
  AttacherType = Attacher::AttachEngine3D
  Height = 12
  Length = 10
  Placement = pos=(50,-43,10) rot=(0,0,1;0rad)
  Width = 43
FEATURE [Part::Box] Box539  label="Krychle539"
  AttacherType = Attacher::AttachEngine3D
  Height = 6
  Length = 6
  Placement = pos=(-27,-47,-8) rot=(0,0,1;0rad)
  Width = 2
FEATURE [Part::Cylinder] Cylinder1544  label="Válec1544"
  Angle = 360
  AttacherType = Attacher::AttachEngine3D
  Height = 50
  Placement = pos=(-39.598,39.598,2) rot=(0,0,1;3.92699rad)
  Radius = 1.5
FEATURE [Part::Cylinder] Cylinder1545  label="Válec1545"
  Angle = 360
  AttacherType = Attacher::AttachEngine3D
  Height = 16
  Placement = pos=(-60,-43,10) rot=(0,0,1;0rad)
  Radius = 6
FEATURE [Part::Box] Box540  label="Krychle540"
  AttacherType = Attacher::AttachEngine3D
  Height = 6
  Length = 6
  Placement = pos=(21,-47,-8) rot=(0,0,1;0rad)
  Width = 2
FEATURE [Part::Cylinder] Cylinder1546  label="Válec1546"
  Angle = 360
  AttacherType = Attacher::AttachEngine3D
  Height = 20
  Placement = pos=(24,-40,-5) rot=(1,0,0;1.5708rad)
  Radius = 1.5
FEATURE [Part::Compound] Compound908
  Links = -> [Cylinder1519,Cylinder1525,Cylinder1508,Cylinder1511,Cylinder1521,Cylinder1514,Cylinder1505]
FEATURE [Part::Compound] Compound909
  Links = -> [Cylinder1542,Cylinder1545]
FEATURE [Part::Compound] Compound910
  Links = -> [Cylinder1504,Cylinder1543,Cylinder1513,Cylinder1503,Cylinder1509,Cylinder1544,Cylinder1501,Cylinder1506]
FEATURE [Part::Compound] Compound911
  Links = -> [Cylinder1522,Cylinder1527,Cylinder1520,Cylinder1524,Cylinder1523,Cylinder1532,Cylinder1528,Cylinder1526]
  Placement = pos=(0,0,0) rot=(0,0,1;0.392699rad)
FEATURE [Part::Compound] Compound912
  Links = -> [Cylinder1540,Cylinder1546,Cylinder1538,Cylinder1502]
FEATURE [Part::Compound] Compound913
  Links = -> [Cylinder1518,Cylinder1517,Cylinder1515,Cylinder1507]
FEATURE [Part::Compound] Compound916
  Links = -> [Box539,Box540,Box536,Box535]
FEATURE [Part::Compound] Compound918
  Links = -> [Box523,Box538]
FEATURE [Part::Compound] Compound919
  Links = -> [Cylinder1541,Cylinder1510]
FEATURE [Part::Compound] Compound921
  Links = -> [Cylinder1539,Cylinder1512]
FEATURE [Part::Compound] Compound922
  Links = -> [Box527,Box534,Box521,Box530]
FEATURE [Part::Compound] Compound923
  Links = -> [Box528,Box529,Box525,Box532,Box526,Box531,Box522,Box533]
  Placement = pos=(0,0,0) rot=(0,0,1;0.392699rad)
FEATURE [Part::FeaturePython] wormgear084  # WARN: FeaturePython — macro-defined, semantics opaque (R4)
  AttacherType = Attacher::AttachEngine3D
  Placement = pos=(0,0,0) rot=(0,0,1;0.083427rad)
  beta = 40.5833
  clearance = 0.25
  diameter = 78.8
  head = 0
  height = 20
  module = 1.5
  pressure_angle = 20
  reverse_pitch = false
  teeth = 45
  version = 0.0.3
FEATURE [Part::FeaturePython] wormgear085  # WARN: FeaturePython — macro-defined, semantics opaque (R4)
  AttacherType = Attacher::AttachEngine3D
  Placement = pos=(0,0,0) rot=(0,0,1;0.124791rad)
  beta = 40.5833
  clearance = 0.25
  diameter = 78.8
  head = 0
  height = 20
  module = 1.5
  pressure_angle = 20
  reverse_pitch = true
  teeth = 45
  version = 0.0.3
FEATURE [Part::FeaturePython] Tube094  # WARN: FeaturePython — macro-defined, semantics opaque (R4)
  AttacherType = Attacher::AttachEngine3D
  Height = 8
  InnerRadius = 42
  OuterRadius = 52
  Placement = pos=(0,0,-8) rot=(0,0,1;0rad)
FEATURE [Part::Cut] Cut548
  Base = -> Box537
  Placement = pos=(0,0,-20) rot=(0,0,1;0rad)
  Tool = -> Cylinder1537
FEATURE [Part::Cut] Cut544
  Base = -> Cut548
  Placement = pos=(0,0,-8) rot=(0,0,1;0rad)
  Tool = -> Compound919
FEATURE [Part::Cut] Cut546
  Base = -> Cut544
  Tool = -> Compound921
FEATURE [Part::Cut] Cut547
  Base = -> Cut546
  Tool = -> Compound916
FEATURE [Part::Cut] Cut545
  Base = -> Cut547
  Tool = -> Compound912
FEATURE [Part::Fillet] Fillet024
  Base = -> Cut545
  Edges = 2 edges r=12: [Edge2,Edge38]
  Placement = pos=(0,0,-6) rot=(0,0,1;0rad)
FEATURE [Part::Cut] Cut549
  Base = -> Tube094
  Tool = -> Compound922
FEATURE [Part::Cut] Cut550
  Base = -> Box524
  Placement = pos=(0,0,-10) rot=(0,0,1;0rad)
  Tool = -> Cylinder1516
FEATURE [Part::Cut] Cut552
  Base = -> Compound918
  Tool = -> Compound910
FEATURE [Part::Cut] Cut555
  Base = -> Cut549
  Tool = -> Compound913
FEATURE [Part::Cut] Cut551
  Base = -> Cut555
  Tool = -> Compound923
FEATURE [Part::Cut] Cut554
  Base = -> Cut551
  Placement = pos=(0,0,-6) rot=(0,0,1;0rad)
  Tool = -> Compound911
FEATURE [Part::Cut] Cut557
  Base = -> Cut552
  Tool = -> Compound909
FEATURE [Part::Fillet] Fillet023
  Base = -> Cut557
  Edges = 2 edges r=8: [Edge4,Edge43]
  Placement = pos=(0,0,-4) rot=(0,0,1;0rad)
FEATURE [Part::Cut] Cut559
  Base = -> Cut550
  Placement = pos=(0,0,-4) rot=(0,0,1;0rad)
  Tool = -> Compound908
FEATURE [Part::Cylinder] Cylinder1547  label="Válec1547"
  Angle = 360
  AttacherType = Attacher::AttachEngine3D
  Height = 12
  Radius = 52
FEATURE [Part::Cut] Cut556
  Base = -> Cylinder1547
  Tool = -> wormgear084
FEATURE [Part::Cylinder] Cylinder1548  label="Válec1548"
  Angle = 360
  AttacherType = Attacher::AttachEngine3D
  Height = 40
  Placement = pos=(0,-17,13) rot=(1,0,0;1.5708rad)
  Radius = 59
FEATURE [Part::Common] Common006
  Base = -> Fillet024
  Tool = -> Cylinder1548
FEATURE [Part::Cylinder] Cylinder1549  label="Válec1549"
  Angle = 360
  AttacherType = Attacher::AttachEngine3D
  Height = 50
  Placement = pos=(-31.8198,31.8198,-18) rot=(0,0,1;0.785398rad)
  Radius = 1.5
FEATURE [Part::Cylinder] Cylinder1550  label="Válec1550"
  Angle = 360
  AttacherType = Attacher::AttachEngine3D
  Height = 20
  Placement = pos=(39.6,-39.6,-10) rot=(0,0,1;0.785398rad)
  Radius = 4
FEATURE [Part::Cylinder] Cylinder1551  label="Válec1551"
  Angle = 360
  AttacherType = Attacher::AttachEngine3D
  Height = 20
  Placement = pos=(-39.6,-39.6,-10) rot=(0,0,-1;0.785398rad)
  Radius = 4
FEATURE [Part::Compound] Compound917
  Links = -> [Cylinder1551,Cylinder1550]
FEATURE [Part::Cylinder] Cylinder1552  label="Válec1552"
  Angle = 360
  AttacherType = Attacher::AttachEngine3D
  Height = 50
  Placement = pos=(-1.2e-14,56,2) rot=(0,0,1;3.14159rad)
  Radius = 1.5
FEATURE [Part::Cylinder] Cylinder1553  label="Válec1553"
  Angle = 360
  AttacherType = Attacher::AttachEngine3D
  Height = 12
  Radius = 60
FEATURE [Part::Cut] Cut558
  Base = -> Cylinder1553
  Placement = pos=(0,0,12) rot=(0,0,1;0.034907rad)
  Tool = -> wormgear085
FEATURE [Part::Compound] Compound920
  Links = -> [Cut558,Cut556]
FEATURE [Part::Cylinder] Cylinder1554  label="Válec1554"
  Angle = 360
  AttacherType = Attacher::AttachEngine3D
  Height = 50
  Placement = pos=(39.598,39.598,2) rot=(0,0,1;2.35619rad)
  Radius = 1.5
FEATURE [Part::Cylinder] Cylinder1555  label="Válec1555"
  Angle = 360
  AttacherType = Attacher::AttachEngine3D
  Height = 50
  Placement = pos=(56,0,2) rot=(0,0,1;1.5708rad)
  Radius = 1.5
FEATURE [Part::Cylinder] Cylinder1556  label="Válec1556"
  Angle = 360
  AttacherType = Attacher::AttachEngine3D
  Height = 50
  Placement = pos=(-31.8198,-31.8198,-18) rot=(0,0,1;2.35619rad)
  Radius = 1.5
FEATURE [Part::Cylinder] Cylinder1557  label="Válec1557"
  Angle = 360
  AttacherType = Attacher::AttachEngine3D
  Height = 50
  Placement = pos=(0,-56,2) rot=(0,0,1;0rad)
  Radius = 1.5
FEATURE [Part::Cylinder] Cylinder1558  label="Válec1558"
  Angle = 360
  AttacherType = Attacher::AttachEngine3D
  Height = 50
  Placement = pos=(-39.598,39.598,2) rot=(0,0,1;3.92699rad)
  Radius = 1.5
FEATURE [Part::Compound] Compound914
  Links = -> [Cylinder1557,Cylinder1531,Cylinder1555,Cylinder1554,Cylinder1552,Cylinder1558,Cylinder1536,Cylinder1535]
FEATURE [Part::Cut] Cut553
  Base = -> Compound920
  Tool = -> Compound914
FEATURE [Part::Cut] Cut560
  Base = -> Cut553
  Tool = -> Compound917
FEATURE [Part::Cylinder] Cylinder1559  label="Válec1559"
  Angle = 360
  AttacherType = Attacher::AttachEngine3D
  Height = 50
  Placement = pos=(45,1.9e-14,-18) rot=(0,0,-1;1.5708rad)
  Radius = 1.5
FEATURE [Part::Cylinder] Cylinder1560  label="Válec1560"
  Angle = 360
  AttacherType = Attacher::AttachEngine3D
  Height = 50
  Placement = pos=(-45,-6e-15,-18) rot=(0,0,1;1.5708rad)
  Radius = 1.5
FEATURE [Part::Compound] Compound915
  Links = -> [Cylinder1533,Cylinder1549,Cylinder1560,Cylinder1556,Cylinder1534,Cylinder1530,Cylinder1559,Cylinder1529]
  Placement = pos=(0,0,-20) rot=(0,0,1;0.392699rad)
FEATURE [Part::Cut] Cut543
  Base = -> Cut560
  Placement = pos=(0,0,-6) rot=(0,0,1;0rad)
  Tool = -> Compound915
FEATURE [Part::Box] Box541  label="Krychle541"
  AttacherType = Attacher::AttachEngine3D
  Height = 6
  Length = 6
  Placement = pos=(17,-47,-8) rot=(0,0,1;0rad)
  Width = 2
FEATURE [Part::Cylinder] Cylinder1561  label="Válec1561"
  Angle = 360
  AttacherType = Attacher::AttachEngine3D
  Height = 40
  Placement = pos=(-59,-17,0) rot=(0,0,1;0rad)
  Radius = 10
FEATURE [Part::Cylinder] Cylinder1562  label="Válec1562"
  Angle = 360
  AttacherType = Attacher::AttachEngine3D
  Height = 20
  Placement = pos=(-51,-40,7) rot=(1,0,0;1.5708rad)
  Radius = 1.5
FEATURE [Part::Cylinder] Cylinder1563  label="Válec1563"
  Angle = 360
  AttacherType = Attacher::AttachEngine3D
  Height = 40
  Placement = pos=(59,-17,0) rot=(0,0,1;0rad)
  Radius = 10
FEATURE [Part::Cylinder] Cylinder1564  label="Válec1564"
  Angle = 360
  AttacherType = Attacher::AttachEngine3D
  Height = 40
  Placement = pos=(39.6,-39.6,-10) rot=(0,0,1;0.785398rad)
  Radius = 4
FEATURE [Part::Cylinder] Cylinder1565  label="Válec1565"
  Angle = 360
  AttacherType = Attacher::AttachEngine3D
  Height = 20
  Placement = pos=(-20,-40,-5) rot=(1,0,0;1.5708rad)
  Radius = 1.5
FEATURE [Part::Box] Box542  label="Krychle542"
  AttacherType = Attacher::AttachEngine3D
  Height = 6
  Length = 6
  Placement = pos=(48,-45,4) rot=(0,0,1;0rad)
  Width = 2
FEATURE [Part::Cylinder] Cylinder1566  label="Válec1566"
  Angle = 360
  AttacherType = Attacher::AttachEngine3D
  Height = 20
  Placement = pos=(0,0,20) rot=(0,0,1;0rad)
  Radius = 52
FEATURE [Part::Box] Box543  label="Krychle543"
  AttacherType = Attacher::AttachEngine3D
  Height = 12
  Length = 108
  Placement = pos=(-54,-53,20) rot=(0,0,1;0rad)
  Width = 36
FEATURE [Part::Cut] Cut565
  Base = -> Box543
  Placement = pos=(0,0,-20) rot=(0,0,1;0rad)
  Tool = -> Cylinder1566
FEATURE [Part::Cylinder] Cylinder1567  label="Válec1567"
  Angle = 360
  AttacherType = Attacher::AttachEngine3D
  Height = 40
  Placement = pos=(-39.6,-39.6,-10) rot=(0,0,-1;0.785398rad)
  Radius = 4
FEATURE [Part::Box] Box544  label="Krychle544"
  AttacherType = Attacher::AttachEngine3D
  Height = 6
  Length = 6
  Placement = pos=(-23,-47,-8) rot=(0,0,1;0rad)
  Width = 2
FEATURE [Part::Box] Box545  label="Krychle545"
  AttacherType = Attacher::AttachEngine3D
  Height = 6
  Length = 6
  Placement = pos=(-54,-45,4) rot=(0,0,1;0rad)
  Width = 2
FEATURE [Part::Cylinder] Cylinder1568  label="Válec1568"
  Angle = 360
  AttacherType = Attacher::AttachEngine3D
  Height = 20
  Placement = pos=(51,-40,7) rot=(1,0,0;1.5708rad)
  Radius = 1.5
FEATURE [Part::Cylinder] Cylinder1569  label="Válec1569"
  Angle = 360
  AttacherType = Attacher::AttachEngine3D
  Height = 20
  Placement = pos=(20,-40,-5) rot=(1,0,0;1.5708rad)
  Radius = 1.5
FEATURE [Part::Compound] Compound924
  Links = -> [Cylinder1565,Cylinder1569,Cylinder1568,Cylinder1562]
FEATURE [Part::Compound] Compound925
  Links = -> [Box544,Box541,Box542,Box545]
FEATURE [Part::Compound] Compound926
  Links = -> [Cylinder1567,Cylinder1564]
  Placement = pos=(0,0,1) rot=(0,0,1;0rad)
FEATURE [Part::Compound] Compound927
  Links = -> [Cylinder1563,Cylinder1561]
FEATURE [Part::Cut] Cut564
  Base = -> Cut565
  Tool = -> Compound927
FEATURE [Part::Cut] Cut562
  Base = -> Cut564
  Tool = -> Compound926
FEATURE [Part::Cut] Cut561
  Base = -> Cut562
  Tool = -> Compound925
FEATURE [Part::Cut] Cut563
  Base = -> Cut561
  Tool = -> Compound924
FEATURE [Part::Fillet] Fillet025
  Base = -> Cut563
  Edges = 2 edges r=12: [Edge3,Edge38]
  Placement = pos=(0,0,-6) rot=(0,0,1;0rad)
FEATURE [Part::Compound] Compound928  label="J-max-deep_monoblok"
  Links = -> [Common006,Cut543,Cut554,Cut559,Fillet023,Fillet025]
FEATURE [Part::FeaturePython] Tube  label="ZKL-6818"  # WARN: FeaturePython — macro-defined, semantics opaque (R4)
  AttacherType = Attacher::AttachEngine3D
  Height = 13
  InnerRadius = 45
  OuterRadius = 57.5
  Placement = pos=(0,0,31) rot=(0,0,1;0rad)
